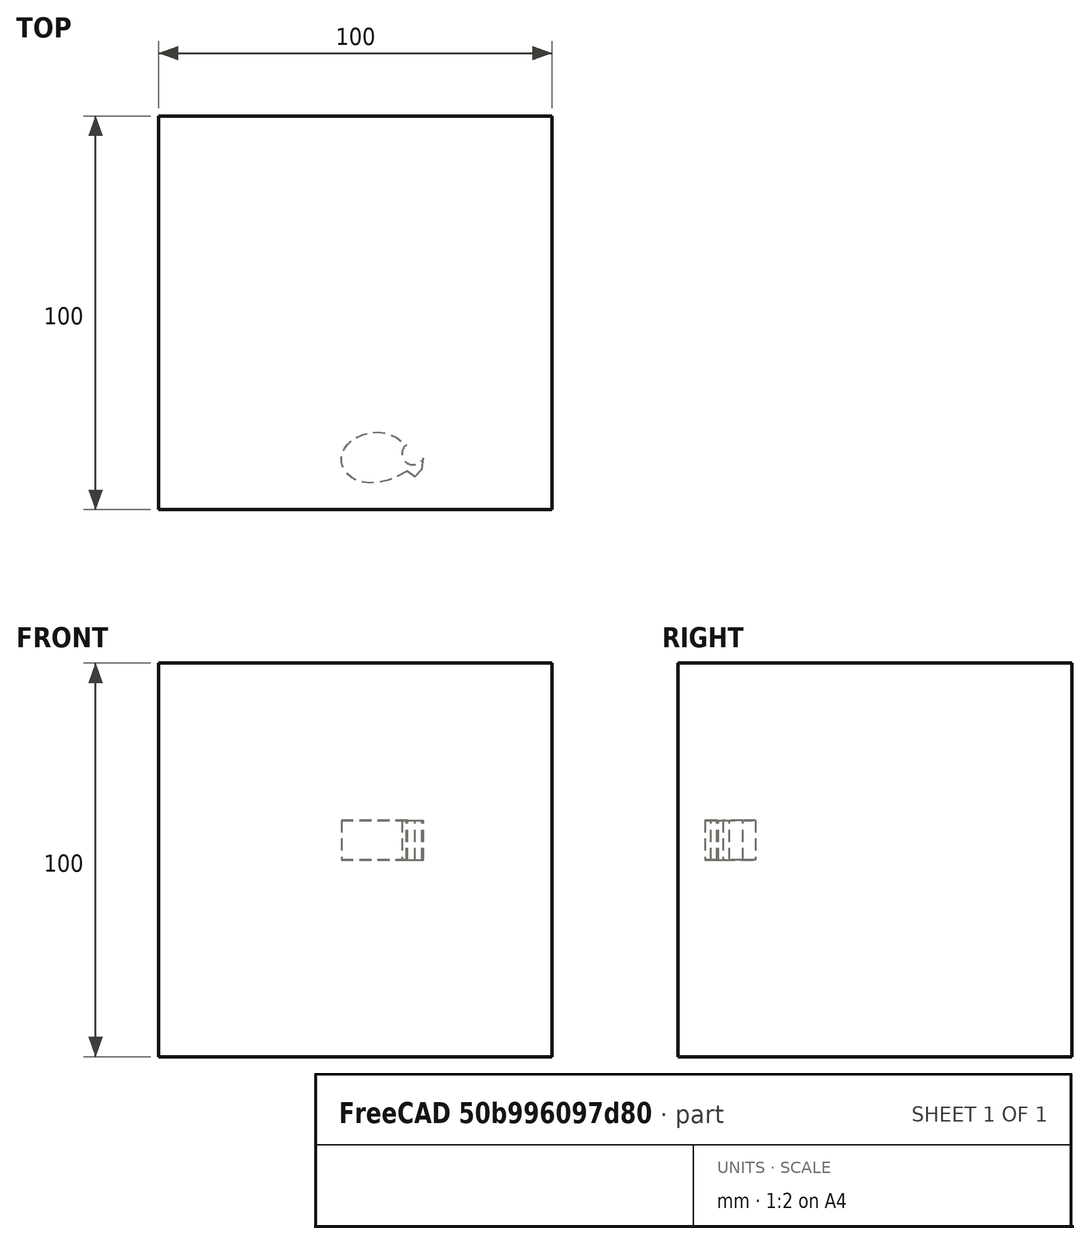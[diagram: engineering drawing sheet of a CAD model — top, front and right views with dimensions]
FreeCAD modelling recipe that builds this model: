
FCSTD DOCUMENT  (FreeCAD 1.0R39109 (Git))
Label: mirrorTest-3b
License: All rights reserved
LicenseURL: http://en.wikipedia.org/wiki/All_rights_reserved
objects: App::DocumentObjectGroupPython×1248, Part::Mirroring×2, App::Part×2, Part::FeaturePython×1, Sketcher::SketchObject×1, Part::Extrusion×1
note: 6 computed .brp shape members not serialized (recipe doc carries the construction recipe); baked Part::Feature solids carry a one-line shape summary decoded from their .brp

FEATURE [App::DocumentObjectGroupPython] HALFPI  # scripted group (container) (typed FeaturePython)
  name = HALFPI
  value = pi/2.
FEATURE [App::DocumentObjectGroupPython] PI  # scripted group (container) (typed FeaturePython)
  name = PI
  value = 1.*pi
FEATURE [App::DocumentObjectGroupPython] TWOPI  # scripted group (container) (typed FeaturePython)
  name = TWOPI
  value = 2.*pi
FEATURE [App::DocumentObjectGroupPython] Constants  # scripted group (container) (typed FeaturePython)
  Group = -> [HALFPI,PI,TWOPI]
FEATURE [App::DocumentObjectGroupPython] Variables  # scripted group (container) (typed FeaturePython)
FEATURE [App::DocumentObjectGroupPython] Quantities  # scripted group (container) (typed FeaturePython)
FEATURE [App::DocumentObjectGroupPython] Isotopes  # scripted group (container) (typed FeaturePython)
FEATURE [App::DocumentObjectGroupPython] Elements  # scripted group (container) (typed FeaturePython)
FEATURE [App::DocumentObjectGroupPython] G4Isotopes  # scripted group (container) (typed FeaturePython)
FEATURE [App::DocumentObjectGroupPython] H_element  # scripted group (container) (typed FeaturePython)
  Z = 1
  atom_value = 1.008
  formula = H
  name = H_element
FEATURE [App::DocumentObjectGroupPython] He_element  # scripted group (container) (typed FeaturePython)
  Z = 2
  atom_value = 4.0026
  formula = He
  name = He_element
FEATURE [App::DocumentObjectGroupPython] Li_element  # scripted group (container) (typed FeaturePython)
  Z = 3
  atom_value = 6.94
  formula = Li
  name = Li_element
FEATURE [App::DocumentObjectGroupPython] Be_element  # scripted group (container) (typed FeaturePython)
  Z = 4
  atom_value = 9.01218
  formula = Be
  name = Be_element
FEATURE [App::DocumentObjectGroupPython] B_element  # scripted group (container) (typed FeaturePython)
  Z = 5
  atom_value = 10.81
  formula = B
  name = B_element
FEATURE [App::DocumentObjectGroupPython] C_element  # scripted group (container) (typed FeaturePython)
  Z = 6
  atom_value = 12.011
  formula = C
  name = C_element
FEATURE [App::DocumentObjectGroupPython] N_element  # scripted group (container) (typed FeaturePython)
  Z = 7
  atom_value = 14.007
  formula = N
  name = N_element
FEATURE [App::DocumentObjectGroupPython] O_element  # scripted group (container) (typed FeaturePython)
  Z = 8
  atom_value = 15.999
  formula = O
  name = O_element
FEATURE [App::DocumentObjectGroupPython] F_element  # scripted group (container) (typed FeaturePython)
  Z = 9
  atom_value = 18.9984
  formula = F
  name = F_element
FEATURE [App::DocumentObjectGroupPython] Ne_element  # scripted group (container) (typed FeaturePython)
  Z = 10
  atom_value = 20.1797
  formula = Ne
  name = Ne_element
FEATURE [App::DocumentObjectGroupPython] Na_element  # scripted group (container) (typed FeaturePython)
  Z = 11
  atom_value = 22.9898
  formula = Na
  name = Na_element
FEATURE [App::DocumentObjectGroupPython] Mg_element  # scripted group (container) (typed FeaturePython)
  Z = 12
  atom_value = 24.305
  formula = Mg
  name = Mg_element
FEATURE [App::DocumentObjectGroupPython] Al_element  # scripted group (container) (typed FeaturePython)
  Z = 13
  atom_value = 26.9815
  formula = Al
  name = Al_element
FEATURE [App::DocumentObjectGroupPython] Si_element  # scripted group (container) (typed FeaturePython)
  Z = 14
  atom_value = 28.085
  formula = Si
  name = Si_element
FEATURE [App::DocumentObjectGroupPython] P_element  # scripted group (container) (typed FeaturePython)
  Z = 15
  atom_value = 30.9738
  formula = P
  name = P_element
FEATURE [App::DocumentObjectGroupPython] S_element  # scripted group (container) (typed FeaturePython)
  Z = 16
  atom_value = 32.06
  formula = S
  name = S_element
FEATURE [App::DocumentObjectGroupPython] Cl_element  # scripted group (container) (typed FeaturePython)
  Z = 17
  atom_value = 35.45
  formula = Cl
  name = Cl_element
FEATURE [App::DocumentObjectGroupPython] Ar_element  # scripted group (container) (typed FeaturePython)
  Z = 18
  atom_value = 39.95
  formula = Ar
  name = Ar_element
FEATURE [App::DocumentObjectGroupPython] K_element  # scripted group (container) (typed FeaturePython)
  Z = 19
  atom_value = 39.0983
  formula = K
  name = K_element
FEATURE [App::DocumentObjectGroupPython] Ca_element  # scripted group (container) (typed FeaturePython)
  Z = 20
  atom_value = 40.078
  formula = Ca
  name = Ca_element
FEATURE [App::DocumentObjectGroupPython] Sc_element  # scripted group (container) (typed FeaturePython)
  Z = 21
  atom_value = 44.9559
  formula = Sc
  name = Sc_element
FEATURE [App::DocumentObjectGroupPython] Ti_element  # scripted group (container) (typed FeaturePython)
  Z = 22
  atom_value = 47.867
  formula = Ti
  name = Ti_element
FEATURE [App::DocumentObjectGroupPython] V_element  # scripted group (container) (typed FeaturePython)
  Z = 23
  atom_value = 50.9415
  formula = V
  name = V_element
FEATURE [App::DocumentObjectGroupPython] Cr_element  # scripted group (container) (typed FeaturePython)
  Z = 24
  atom_value = 51.9961
  formula = Cr
  name = Cr_element
FEATURE [App::DocumentObjectGroupPython] Mn_element  # scripted group (container) (typed FeaturePython)
  Z = 25
  atom_value = 54.938
  formula = Mn
  name = Mn_element
FEATURE [App::DocumentObjectGroupPython] Fe_element  # scripted group (container) (typed FeaturePython)
  Z = 26
  atom_value = 55.845
  formula = Fe
  name = Fe_element
FEATURE [App::DocumentObjectGroupPython] Co_element  # scripted group (container) (typed FeaturePython)
  Z = 27
  atom_value = 58.9332
  formula = Co
  name = Co_element
FEATURE [App::DocumentObjectGroupPython] Ni_element  # scripted group (container) (typed FeaturePython)
  Z = 28
  atom_value = 58.6934
  formula = Ni
  name = Ni_element
FEATURE [App::DocumentObjectGroupPython] Cu_element  # scripted group (container) (typed FeaturePython)
  Z = 29
  atom_value = 63.546
  formula = Cu
  name = Cu_element
FEATURE [App::DocumentObjectGroupPython] Zn_element  # scripted group (container) (typed FeaturePython)
  Z = 30
  atom_value = 65.38
  formula = Zn
  name = Zn_element
FEATURE [App::DocumentObjectGroupPython] Ga_element  # scripted group (container) (typed FeaturePython)
  Z = 31
  atom_value = 69.723
  formula = Ga
  name = Ga_element
FEATURE [App::DocumentObjectGroupPython] Ge_element  # scripted group (container) (typed FeaturePython)
  Z = 32
  atom_value = 72.63
  formula = Ge
  name = Ge_element
FEATURE [App::DocumentObjectGroupPython] As_element  # scripted group (container) (typed FeaturePython)
  Z = 33
  atom_value = 74.9216
  formula = As
  name = As_element
FEATURE [App::DocumentObjectGroupPython] Se_element  # scripted group (container) (typed FeaturePython)
  Z = 34
  atom_value = 78.971
  formula = Se
  name = Se_element
FEATURE [App::DocumentObjectGroupPython] Br_element  # scripted group (container) (typed FeaturePython)
  Z = 35
  atom_value = 79.904
  formula = Br
  name = Br_element
FEATURE [App::DocumentObjectGroupPython] Kr_element  # scripted group (container) (typed FeaturePython)
  Z = 36
  atom_value = 83.798
  formula = Kr
  name = Kr_element
FEATURE [App::DocumentObjectGroupPython] Rb_element  # scripted group (container) (typed FeaturePython)
  Z = 37
  atom_value = 85.4678
  formula = Rb
  name = Rb_element
FEATURE [App::DocumentObjectGroupPython] Sr_element  # scripted group (container) (typed FeaturePython)
  Z = 38
  atom_value = 87.62
  formula = Sr
  name = Sr_element
FEATURE [App::DocumentObjectGroupPython] Y_element  # scripted group (container) (typed FeaturePython)
  Z = 39
  atom_value = 88.9058
  formula = Y
  name = Y_element
FEATURE [App::DocumentObjectGroupPython] Zr_element  # scripted group (container) (typed FeaturePython)
  Z = 40
  atom_value = 91.224
  formula = Zr
  name = Zr_element
FEATURE [App::DocumentObjectGroupPython] Nb_element  # scripted group (container) (typed FeaturePython)
  Z = 41
  atom_value = 92.9064
  formula = Nb
  name = Nb_element
FEATURE [App::DocumentObjectGroupPython] Mo_element  # scripted group (container) (typed FeaturePython)
  Z = 42
  atom_value = 95.95
  formula = Mo
  name = Mo_element
FEATURE [App::DocumentObjectGroupPython] Tc_element  # scripted group (container) (typed FeaturePython)
  Z = 43
  atom_value = 97
  formula = Tc
  name = Tc_element
FEATURE [App::DocumentObjectGroupPython] Ru_element  # scripted group (container) (typed FeaturePython)
  Z = 44
  atom_value = 101.07
  formula = Ru
  name = Ru_element
FEATURE [App::DocumentObjectGroupPython] Rh_element  # scripted group (container) (typed FeaturePython)
  Z = 45
  atom_value = 102.905
  formula = Rh
  name = Rh_element
FEATURE [App::DocumentObjectGroupPython] Pd_element  # scripted group (container) (typed FeaturePython)
  Z = 46
  atom_value = 106.42
  formula = Pd
  name = Pd_element
FEATURE [App::DocumentObjectGroupPython] Ag_element  # scripted group (container) (typed FeaturePython)
  Z = 47
  atom_value = 107.868
  formula = Ag
  name = Ag_element
FEATURE [App::DocumentObjectGroupPython] Cd_element  # scripted group (container) (typed FeaturePython)
  Z = 48
  atom_value = 112.414
  formula = Cd
  name = Cd_element
FEATURE [App::DocumentObjectGroupPython] In_element  # scripted group (container) (typed FeaturePython)
  Z = 49
  atom_value = 114.818
  formula = In
  name = In_element
FEATURE [App::DocumentObjectGroupPython] Sn_element  # scripted group (container) (typed FeaturePython)
  Z = 50
  atom_value = 118.71
  formula = Sn
  name = Sn_element
FEATURE [App::DocumentObjectGroupPython] Sb_element  # scripted group (container) (typed FeaturePython)
  Z = 51
  atom_value = 121.76
  formula = Sb
  name = Sb_element
FEATURE [App::DocumentObjectGroupPython] Te_element  # scripted group (container) (typed FeaturePython)
  Z = 52
  atom_value = 127.6
  formula = Te
  name = Te_element
FEATURE [App::DocumentObjectGroupPython] I_element  # scripted group (container) (typed FeaturePython)
  Z = 53
  atom_value = 126.904
  formula = I
  name = I_element
FEATURE [App::DocumentObjectGroupPython] Xe_element  # scripted group (container) (typed FeaturePython)
  Z = 54
  atom_value = 131.293
  formula = Xe
  name = Xe_element
FEATURE [App::DocumentObjectGroupPython] Cs_element  # scripted group (container) (typed FeaturePython)
  Z = 55
  atom_value = 132.905
  formula = Cs
  name = Cs_element
FEATURE [App::DocumentObjectGroupPython] Ba_element  # scripted group (container) (typed FeaturePython)
  Z = 56
  atom_value = 137.327
  formula = Ba
  name = Ba_element
FEATURE [App::DocumentObjectGroupPython] La_element  # scripted group (container) (typed FeaturePython)
  Z = 57
  atom_value = 138.905
  formula = La
  name = La_element
FEATURE [App::DocumentObjectGroupPython] Ce_element  # scripted group (container) (typed FeaturePython)
  Z = 58
  atom_value = 140.116
  formula = Ce
  name = Ce_element
FEATURE [App::DocumentObjectGroupPython] Pr_element  # scripted group (container) (typed FeaturePython)
  Z = 59
  atom_value = 140.908
  formula = Pr
  name = Pr_element
FEATURE [App::DocumentObjectGroupPython] Nd_element  # scripted group (container) (typed FeaturePython)
  Z = 60
  atom_value = 144.242
  formula = Nd
  name = Nd_element
FEATURE [App::DocumentObjectGroupPython] Pm_element  # scripted group (container) (typed FeaturePython)
  Z = 61
  atom_value = 145
  formula = Pm
  name = Pm_element
FEATURE [App::DocumentObjectGroupPython] Sm_element  # scripted group (container) (typed FeaturePython)
  Z = 62
  atom_value = 150.36
  formula = Sm
  name = Sm_element
FEATURE [App::DocumentObjectGroupPython] Eu_element  # scripted group (container) (typed FeaturePython)
  Z = 63
  atom_value = 151.964
  formula = Eu
  name = Eu_element
FEATURE [App::DocumentObjectGroupPython] Gd_element  # scripted group (container) (typed FeaturePython)
  Z = 64
  atom_value = 157.25
  formula = Gd
  name = Gd_element
FEATURE [App::DocumentObjectGroupPython] Tb_element  # scripted group (container) (typed FeaturePython)
  Z = 65
  atom_value = 158.925
  formula = Tb
  name = Tb_element
FEATURE [App::DocumentObjectGroupPython] Dy_element  # scripted group (container) (typed FeaturePython)
  Z = 66
  atom_value = 162.5
  formula = Dy
  name = Dy_element
FEATURE [App::DocumentObjectGroupPython] Ho_element  # scripted group (container) (typed FeaturePython)
  Z = 67
  atom_value = 164.93
  formula = Ho
  name = Ho_element
FEATURE [App::DocumentObjectGroupPython] Er_element  # scripted group (container) (typed FeaturePython)
  Z = 68
  atom_value = 167.259
  formula = Er
  name = Er_element
FEATURE [App::DocumentObjectGroupPython] Tm_element  # scripted group (container) (typed FeaturePython)
  Z = 69
  atom_value = 168.934
  formula = Tm
  name = Tm_element
FEATURE [App::DocumentObjectGroupPython] Yb_element  # scripted group (container) (typed FeaturePython)
  Z = 70
  atom_value = 173.045
  formula = Yb
  name = Yb_element
FEATURE [App::DocumentObjectGroupPython] Lu_element  # scripted group (container) (typed FeaturePython)
  Z = 71
  atom_value = 174.967
  formula = Lu
  name = Lu_element
FEATURE [App::DocumentObjectGroupPython] Hf_element  # scripted group (container) (typed FeaturePython)
  Z = 72
  atom_value = 178.49
  formula = Hf
  name = Hf_element
FEATURE [App::DocumentObjectGroupPython] Ta_element  # scripted group (container) (typed FeaturePython)
  Z = 73
  atom_value = 180.948
  formula = Ta
  name = Ta_element
FEATURE [App::DocumentObjectGroupPython] W_element  # scripted group (container) (typed FeaturePython)
  Z = 74
  atom_value = 183.84
  formula = W
  name = W_element
FEATURE [App::DocumentObjectGroupPython] Re_element  # scripted group (container) (typed FeaturePython)
  Z = 75
  atom_value = 186.207
  formula = Re
  name = Re_element
FEATURE [App::DocumentObjectGroupPython] Os_element  # scripted group (container) (typed FeaturePython)
  Z = 76
  atom_value = 190.23
  formula = Os
  name = Os_element
FEATURE [App::DocumentObjectGroupPython] Ir_element  # scripted group (container) (typed FeaturePython)
  Z = 77
  atom_value = 192.217
  formula = Ir
  name = Ir_element
FEATURE [App::DocumentObjectGroupPython] Pt_element  # scripted group (container) (typed FeaturePython)
  Z = 78
  atom_value = 195.084
  formula = Pt
  name = Pt_element
FEATURE [App::DocumentObjectGroupPython] Au_element  # scripted group (container) (typed FeaturePython)
  Z = 79
  atom_value = 196.967
  formula = Au
  name = Au_element
FEATURE [App::DocumentObjectGroupPython] Hg_element  # scripted group (container) (typed FeaturePython)
  Z = 80
  atom_value = 200.592
  formula = Hg
  name = Hg_element
FEATURE [App::DocumentObjectGroupPython] Tl_element  # scripted group (container) (typed FeaturePython)
  Z = 81
  atom_value = 204.38
  formula = Tl
  name = Tl_element
FEATURE [App::DocumentObjectGroupPython] Pb_element  # scripted group (container) (typed FeaturePython)
  Z = 82
  atom_value = 207.2
  formula = Pb
  name = Pb_element
FEATURE [App::DocumentObjectGroupPython] Bi_element  # scripted group (container) (typed FeaturePython)
  Z = 83
  atom_value = 208.98
  formula = Bi
  name = Bi_element
FEATURE [App::DocumentObjectGroupPython] Po_element  # scripted group (container) (typed FeaturePython)
  Z = 84
  atom_value = 209
  formula = Po
  name = Po_element
FEATURE [App::DocumentObjectGroupPython] At_element  # scripted group (container) (typed FeaturePython)
  Z = 85
  atom_value = 210
  formula = At
  name = At_element
FEATURE [App::DocumentObjectGroupPython] Rn_element  # scripted group (container) (typed FeaturePython)
  Z = 86
  atom_value = 222
  formula = Rn
  name = Rn_element
FEATURE [App::DocumentObjectGroupPython] Fr_element  # scripted group (container) (typed FeaturePython)
  Z = 87
  atom_value = 223
  formula = Fr
  name = Fr_element
FEATURE [App::DocumentObjectGroupPython] Ra_element  # scripted group (container) (typed FeaturePython)
  Z = 88
  atom_value = 226
  formula = Ra
  name = Ra_element
FEATURE [App::DocumentObjectGroupPython] Ac_element  # scripted group (container) (typed FeaturePython)
  Z = 89
  atom_value = 227
  formula = Ac
  name = Ac_element
FEATURE [App::DocumentObjectGroupPython] Th_element  # scripted group (container) (typed FeaturePython)
  Z = 90
  atom_value = 232.038
  formula = Th
  name = Th_element
FEATURE [App::DocumentObjectGroupPython] Pa_element  # scripted group (container) (typed FeaturePython)
  Z = 91
  atom_value = 231.036
  formula = Pa
  name = Pa_element
FEATURE [App::DocumentObjectGroupPython] U_element  # scripted group (container) (typed FeaturePython)
  Z = 92
  atom_value = 238.029
  formula = U
  name = U_element
FEATURE [App::DocumentObjectGroupPython] Np_element  # scripted group (container) (typed FeaturePython)
  Z = 93
  atom_value = 237
  formula = Np
  name = Np_element
FEATURE [App::DocumentObjectGroupPython] Pu_element  # scripted group (container) (typed FeaturePython)
  Z = 94
  atom_value = 244
  formula = Pu
  name = Pu_element
FEATURE [App::DocumentObjectGroupPython] Am_element  # scripted group (container) (typed FeaturePython)
  Z = 95
  atom_value = 243
  formula = Am
  name = Am_element
FEATURE [App::DocumentObjectGroupPython] Cm_element  # scripted group (container) (typed FeaturePython)
  Z = 96
  atom_value = 247
  formula = Cm
  name = Cm_element
FEATURE [App::DocumentObjectGroupPython] Bk_element  # scripted group (container) (typed FeaturePython)
  Z = 97
  atom_value = 247
  formula = Bk
  name = Bk_element
FEATURE [App::DocumentObjectGroupPython] Cf_element  # scripted group (container) (typed FeaturePython)
  Z = 98
  atom_value = 251
  formula = Cf
  name = Cf_element
FEATURE [App::DocumentObjectGroupPython] G4Elements  # scripted group (container) (typed FeaturePython)
  Group = -> [H_element,He_element,Li_element,Be_element,B_element,C_element,N_element,O_element,F_element,Ne_element,Na_element,Mg_element,Al_element,Si_element,P_element,S_element,Cl_element,Ar_element,K_element,Ca_element,Sc_element,Ti_element,V_element,Cr_element,Mn_element,Fe_element,Co_element,Ni_element,Cu_element,Zn_element,Ga_element,Ge_element,As_element,Se_element,Br_element,Kr_element,Rb_element,+61 more]
FEATURE [App::DocumentObjectGroupPython] H_element001  label="H_element : 0.101"  # scripted group (container) (typed FeaturePython)
  n = 0.101327
FEATURE [App::DocumentObjectGroupPython] C_element001  label="C_element : 0.775"  # scripted group (container) (typed FeaturePython)
  n = 0.7755
FEATURE [App::DocumentObjectGroupPython] N_element001  label="N_element : 0.035"  # scripted group (container) (typed FeaturePython)
  n = 0.035057
FEATURE [App::DocumentObjectGroupPython] O_element001  label="O_element : 0.052"  # scripted group (container) (typed FeaturePython)
  n = 0.0523159
FEATURE [App::DocumentObjectGroupPython] F_element001  label="F_element : 0.017"  # scripted group (container) (typed FeaturePython)
  n = 0.017422
FEATURE [App::DocumentObjectGroupPython] Ca_element001  label="Ca_element : 0.018"  # scripted group (container) (typed FeaturePython)
  n = 0.018378
FEATURE [App::DocumentObjectGroupPython] G4_A_150_TISSUE  label="G4_A-150_TISSUE"  # scripted group (container) (typed FeaturePython)
  Dunit = g/cm3
  Dvalue = 1.127
  Group = -> [H_element001,C_element001,N_element001,O_element001,F_element001,Ca_element001]
  conduct = 2
  density = 1
  expand = 3
  formula = G4_A-150_TISSUE
  name = G4_A-150_TISSUE
  specific = 4
FEATURE [App::DocumentObjectGroupPython] C_element002  label="C_element : 3"  # scripted group (container) (typed FeaturePython)
  n = 3
  ref = C_element
FEATURE [App::DocumentObjectGroupPython] H_element002  label="H_element : 6"  # scripted group (container) (typed FeaturePython)
  n = 6
  ref = H_element
FEATURE [App::DocumentObjectGroupPython] O_element002  label="O_element : 1"  # scripted group (container) (typed FeaturePython)
  n = 1
  ref = O_element
FEATURE [App::DocumentObjectGroupPython] G4_ACETONE  # scripted group (container) (typed FeaturePython)
  Dunit = g/cm3
  Dvalue = 0.7899
  Group = -> [C_element002,H_element002,O_element002]
  conduct = 2
  density = 1
  expand = 3
  formula = G4_ACETONE
  name = G4_ACETONE
  specific = 4
FEATURE [App::DocumentObjectGroupPython] C_element003  label="C_element : 2"  # scripted group (container) (typed FeaturePython)
  n = 2
  ref = C_element
FEATURE [App::DocumentObjectGroupPython] H_element003  label="H_element : 2"  # scripted group (container) (typed FeaturePython)
  n = 2
  ref = H_element
FEATURE [App::DocumentObjectGroupPython] G4_ACETYLENE  # scripted group (container) (typed FeaturePython)
  Dunit = g/cm3
  Dvalue = 0.0010967
  Group = -> [C_element003,H_element003]
  conduct = 2
  density = 1
  expand = 3
  formula = G4_ACETYLENE
  name = G4_ACETYLENE
  specific = 4
FEATURE [App::DocumentObjectGroupPython] C_element004  label="C_element : 5"  # scripted group (container) (typed FeaturePython)
  n = 5
  ref = C_element
FEATURE [App::DocumentObjectGroupPython] H_element004  label="H_element : 5"  # scripted group (container) (typed FeaturePython)
  n = 5
  ref = H_element
FEATURE [App::DocumentObjectGroupPython] N_element002  label="N_element : 5"  # scripted group (container) (typed FeaturePython)
  n = 5
  ref = N_element
FEATURE [App::DocumentObjectGroupPython] G4_ADENINE  # scripted group (container) (typed FeaturePython)
  Dunit = g/cm3
  Dvalue = 1.6
  Group = -> [C_element004,H_element004,N_element002]
  conduct = 2
  density = 1
  expand = 3
  formula = G4_ADENINE
  name = G4_ADENINE
  specific = 4
FEATURE [App::DocumentObjectGroupPython] H_element005  label="H_element : 0.114"  # scripted group (container) (typed FeaturePython)
  n = 0.114
FEATURE [App::DocumentObjectGroupPython] C_element005  label="C_element : 0.598"  # scripted group (container) (typed FeaturePython)
  n = 0.598
FEATURE [App::DocumentObjectGroupPython] N_element003  label="N_element : 0.007"  # scripted group (container) (typed FeaturePython)
  n = 0.007
FEATURE [App::DocumentObjectGroupPython] O_element003  label="O_element : 0.278"  # scripted group (container) (typed FeaturePython)
  n = 0.278
FEATURE [App::DocumentObjectGroupPython] Na_element001  label="Na_element : 0.001"  # scripted group (container) (typed FeaturePython)
  n = 0.001
FEATURE [App::DocumentObjectGroupPython] S_element001  label="S_element : 0.001"  # scripted group (container) (typed FeaturePython)
  n = 0.001
FEATURE [App::DocumentObjectGroupPython] Cl_element001  label="Cl_element : 0.001"  # scripted group (container) (typed FeaturePython)
  n = 0.001
FEATURE [App::DocumentObjectGroupPython] G4_ADIPOSE_TISSUE_ICRP  # scripted group (container) (typed FeaturePython)
  Dunit = g/cm3
  Dvalue = 0.95
  Group = -> [H_element005,C_element005,N_element003,O_element003,Na_element001,S_element001,Cl_element001]
  conduct = 2
  density = 1
  expand = 3
  formula = G4_ADIPOSE_TISSUE_ICRP
  name = G4_ADIPOSE_TISSUE_ICRP
  specific = 4
FEATURE [App::DocumentObjectGroupPython] C_element006  label="C_element : 0.000"  # scripted group (container) (typed FeaturePython)
  n = 0.000124
FEATURE [App::DocumentObjectGroupPython] N_element004  label="N_element : 0.755"  # scripted group (container) (typed FeaturePython)
  n = 0.755268
FEATURE [App::DocumentObjectGroupPython] O_element004  label="O_element : 0.232"  # scripted group (container) (typed FeaturePython)
  n = 0.231781
FEATURE [App::DocumentObjectGroupPython] Ar_element001  label="Ar_element : 0.013"  # scripted group (container) (typed FeaturePython)
  n = 0.012827
FEATURE [App::DocumentObjectGroupPython] G4_AIR  # scripted group (container) (typed FeaturePython)
  Dunit = g/cm3
  Dvalue = 0.00120479
  Group = -> [C_element006,N_element004,O_element004,Ar_element001]
  conduct = 2
  density = 1
  expand = 3
  formula = G4_AIR
  name = G4_AIR
  specific = 4
FEATURE [App::DocumentObjectGroupPython] C_element007  label="C_element : 006"  # scripted group (container) (typed FeaturePython)
  n = 3
  ref = C_element
FEATURE [App::DocumentObjectGroupPython] H_element006  label="H_element : 7"  # scripted group (container) (typed FeaturePython)
  n = 7
  ref = H_element
FEATURE [App::DocumentObjectGroupPython] N_element005  label="N_element : 1"  # scripted group (container) (typed FeaturePython)
  n = 1
  ref = N_element
FEATURE [App::DocumentObjectGroupPython] O_element005  label="O_element : 2"  # scripted group (container) (typed FeaturePython)
  n = 2
  ref = O_element
FEATURE [App::DocumentObjectGroupPython] G4_ALANINE  # scripted group (container) (typed FeaturePython)
  Dunit = g/cm3
  Dvalue = 1.42
  Group = -> [C_element007,H_element006,N_element005,O_element005]
  conduct = 2
  density = 1
  expand = 3
  formula = G4_ALANINE
  name = G4_ALANINE
  specific = 4
FEATURE [App::DocumentObjectGroupPython] Al_element001  label="Al_element : 2"  # scripted group (container) (typed FeaturePython)
  n = 2
  ref = Al_element
FEATURE [App::DocumentObjectGroupPython] O_element006  label="O_element : 3"  # scripted group (container) (typed FeaturePython)
  n = 3
  ref = O_element
FEATURE [App::DocumentObjectGroupPython] G4_ALUMINUM_OXIDE  # scripted group (container) (typed FeaturePython)
  Dunit = g/cm3
  Dvalue = 3.97
  Group = -> [Al_element001,O_element006]
  conduct = 2
  density = 1
  expand = 3
  formula = G4_ALUMINUM_OXIDE
  name = G4_ALUMINUM_OXIDE
  specific = 4
FEATURE [App::DocumentObjectGroupPython] H_element007  label="H_element : 0.106"  # scripted group (container) (typed FeaturePython)
  n = 0.10593
FEATURE [App::DocumentObjectGroupPython] C_element008  label="C_element : 0.789"  # scripted group (container) (typed FeaturePython)
  n = 0.788974
FEATURE [App::DocumentObjectGroupPython] O_element007  label="O_element : 0.105"  # scripted group (container) (typed FeaturePython)
  n = 0.105096
FEATURE [App::DocumentObjectGroupPython] G4_AMBER  # scripted group (container) (typed FeaturePython)
  Dunit = g/cm3
  Dvalue = 1.1
  Group = -> [H_element007,C_element008,O_element007]
  conduct = 2
  density = 1
  expand = 3
  formula = G4_AMBER
  name = G4_AMBER
  specific = 4
FEATURE [App::DocumentObjectGroupPython] N_element006  label="N_element : 006"  # scripted group (container) (typed FeaturePython)
  n = 1
  ref = N_element
FEATURE [App::DocumentObjectGroupPython] H_element008  label="H_element : 3"  # scripted group (container) (typed FeaturePython)
  n = 3
  ref = H_element
FEATURE [App::DocumentObjectGroupPython] G4_AMMONIA  # scripted group (container) (typed FeaturePython)
  Dunit = g/cm3
  Dvalue = 0.000826019
  Group = -> [N_element006,H_element008]
  conduct = 2
  density = 1
  expand = 3
  formula = G4_AMMONIA
  name = G4_AMMONIA
  specific = 4
FEATURE [App::DocumentObjectGroupPython] C_element009  label="C_element : 6"  # scripted group (container) (typed FeaturePython)
  n = 6
  ref = C_element
FEATURE [App::DocumentObjectGroupPython] H_element009  label="H_element : 008"  # scripted group (container) (typed FeaturePython)
  n = 7
  ref = H_element
FEATURE [App::DocumentObjectGroupPython] N_element007  label="N_element : 007"  # scripted group (container) (typed FeaturePython)
  n = 1
  ref = N_element
FEATURE [App::DocumentObjectGroupPython] G4_ANILINE  # scripted group (container) (typed FeaturePython)
  Dunit = g/cm3
  Dvalue = 1.0235
  Group = -> [C_element009,H_element009,N_element007]
  conduct = 2
  density = 1
  expand = 3
  formula = G4_ANILINE
  name = G4_ANILINE
  specific = 4
FEATURE [App::DocumentObjectGroupPython] C_element010  label="C_element : 14"  # scripted group (container) (typed FeaturePython)
  n = 14
  ref = C_element
FEATURE [App::DocumentObjectGroupPython] H_element010  label="H_element : 10"  # scripted group (container) (typed FeaturePython)
  n = 10
  ref = H_element
FEATURE [App::DocumentObjectGroupPython] G4_ANTHRACENE  # scripted group (container) (typed FeaturePython)
  Dunit = g/cm3
  Dvalue = 1.283
  Group = -> [C_element010,H_element010]
  conduct = 2
  density = 1
  expand = 3
  formula = G4_ANTHRACENE
  name = G4_ANTHRACENE
  specific = 4
FEATURE [App::DocumentObjectGroupPython] H_element011  label="H_element : 0.065"  # scripted group (container) (typed FeaturePython)
  n = 0.0654709
FEATURE [App::DocumentObjectGroupPython] C_element011  label="C_element : 0.537"  # scripted group (container) (typed FeaturePython)
  n = 0.536944
FEATURE [App::DocumentObjectGroupPython] N_element008  label="N_element : 0.021"  # scripted group (container) (typed FeaturePython)
  n = 0.0215
FEATURE [App::DocumentObjectGroupPython] O_element008  label="O_element : 0.032"  # scripted group (container) (typed FeaturePython)
  n = 0.032085
FEATURE [App::DocumentObjectGroupPython] F_element002  label="F_element : 0.167"  # scripted group (container) (typed FeaturePython)
  n = 0.167411
FEATURE [App::DocumentObjectGroupPython] Ca_element002  label="Ca_element : 0.177"  # scripted group (container) (typed FeaturePython)
  n = 0.176589
FEATURE [App::DocumentObjectGroupPython] G4_B_100_BONE  label="G4_B-100_BONE"  # scripted group (container) (typed FeaturePython)
  Dunit = g/cm3
  Dvalue = 1.45
  Group = -> [H_element011,C_element011,N_element008,O_element008,F_element002,Ca_element002]
  conduct = 2
  density = 1
  expand = 3
  formula = G4_B-100_BONE
  name = G4_B-100_BONE
  specific = 4
FEATURE [App::DocumentObjectGroupPython] H_element012  label="H_element : 0.057"  # scripted group (container) (typed FeaturePython)
  n = 0.057441
FEATURE [App::DocumentObjectGroupPython] C_element012  label="C_element : 0.790"  # scripted group (container) (typed FeaturePython)
  n = 0.774591
FEATURE [App::DocumentObjectGroupPython] O_element009  label="O_element : 0.168"  # scripted group (container) (typed FeaturePython)
  n = 0.167968
FEATURE [App::DocumentObjectGroupPython] G4_BAKELITE  # scripted group (container) (typed FeaturePython)
  Dunit = g/cm3
  Dvalue = 1.25
  Group = -> [H_element012,C_element012,O_element009]
  conduct = 2
  density = 1
  expand = 3
  formula = G4_BAKELITE
  name = G4_BAKELITE
  specific = 4
FEATURE [App::DocumentObjectGroupPython] Ba_element001  label="Ba_element : 1"  # scripted group (container) (typed FeaturePython)
  n = 1
  ref = Ba_element
FEATURE [App::DocumentObjectGroupPython] F_element003  label="F_element : 2"  # scripted group (container) (typed FeaturePython)
  n = 2
  ref = F_element
FEATURE [App::DocumentObjectGroupPython] G4_BARIUM_FLUORIDE  # scripted group (container) (typed FeaturePython)
  Dunit = g/cm3
  Dvalue = 4.89
  Group = -> [Ba_element001,F_element003]
  conduct = 2
  density = 1
  expand = 3
  formula = G4_BARIUM_FLUORIDE
  name = G4_BARIUM_FLUORIDE
  specific = 4
FEATURE [App::DocumentObjectGroupPython] Ba_element002  label="Ba_element : 002"  # scripted group (container) (typed FeaturePython)
  n = 1
  ref = Ba_element
FEATURE [App::DocumentObjectGroupPython] S_element002  label="S_element : 1"  # scripted group (container) (typed FeaturePython)
  n = 1
  ref = S_element
FEATURE [App::DocumentObjectGroupPython] O_element010  label="O_element : 4"  # scripted group (container) (typed FeaturePython)
  n = 4
  ref = O_element
FEATURE [App::DocumentObjectGroupPython] G4_BARIUM_SULFATE  # scripted group (container) (typed FeaturePython)
  Dunit = g/cm3
  Dvalue = 4.5
  Group = -> [Ba_element002,S_element002,O_element010]
  conduct = 2
  density = 1
  expand = 3
  formula = G4_BARIUM_SULFATE
  name = G4_BARIUM_SULFATE
  specific = 4
FEATURE [App::DocumentObjectGroupPython] C_element013  label="C_element : 007"  # scripted group (container) (typed FeaturePython)
  n = 6
  ref = C_element
FEATURE [App::DocumentObjectGroupPython] H_element013  label="H_element : 009"  # scripted group (container) (typed FeaturePython)
  n = 6
  ref = H_element
FEATURE [App::DocumentObjectGroupPython] G4_BENZENE  # scripted group (container) (typed FeaturePython)
  Dunit = g/cm3
  Dvalue = 0.87865
  Group = -> [C_element013,H_element013]
  conduct = 2
  density = 1
  expand = 3
  formula = G4_BENZENE
  name = G4_BENZENE
  specific = 4
FEATURE [App::DocumentObjectGroupPython] Be_element001  label="Be_element : 1"  # scripted group (container) (typed FeaturePython)
  n = 1
  ref = Be_element
FEATURE [App::DocumentObjectGroupPython] O_element011  label="O_element : 005"  # scripted group (container) (typed FeaturePython)
  n = 1
  ref = O_element
FEATURE [App::DocumentObjectGroupPython] G4_BERYLLIUM_OXIDE  # scripted group (container) (typed FeaturePython)
  Dunit = g/cm3
  Dvalue = 3.01
  Group = -> [Be_element001,O_element011]
  conduct = 2
  density = 1
  expand = 3
  formula = G4_BERYLLIUM_OXIDE
  name = G4_BERYLLIUM_OXIDE
  specific = 4
FEATURE [App::DocumentObjectGroupPython] Bi_element001  label="Bi_element : 4"  # scripted group (container) (typed FeaturePython)
  n = 4
  ref = Bi_element
FEATURE [App::DocumentObjectGroupPython] Ge_element001  label="Ge_element : 3"  # scripted group (container) (typed FeaturePython)
  n = 3
  ref = Ge_element
FEATURE [App::DocumentObjectGroupPython] O_element012  label="O_element : 12"  # scripted group (container) (typed FeaturePython)
  n = 12
  ref = O_element
FEATURE [App::DocumentObjectGroupPython] G4_BGO  # scripted group (container) (typed FeaturePython)
  Dunit = g/cm3
  Dvalue = 7.13
  Group = -> [Bi_element001,Ge_element001,O_element012]
  conduct = 2
  density = 1
  expand = 3
  formula = G4_BGO
  name = G4_BGO
  specific = 4
FEATURE [App::DocumentObjectGroupPython] H_element014  label="H_element : 0.102"  # scripted group (container) (typed FeaturePython)
  n = 0.102
FEATURE [App::DocumentObjectGroupPython] C_element014  label="C_element : 0.110"  # scripted group (container) (typed FeaturePython)
  n = 0.11
FEATURE [App::DocumentObjectGroupPython] N_element009  label="N_element : 0.033"  # scripted group (container) (typed FeaturePython)
  n = 0.033
FEATURE [App::DocumentObjectGroupPython] O_element013  label="O_element : 0.745"  # scripted group (container) (typed FeaturePython)
  n = 0.745
FEATURE [App::DocumentObjectGroupPython] Na_element002  label="Na_element : 0.002"  # scripted group (container) (typed FeaturePython)
  n = 0.001
FEATURE [App::DocumentObjectGroupPython] P_element001  label="P_element : 0.001"  # scripted group (container) (typed FeaturePython)
  n = 0.001
FEATURE [App::DocumentObjectGroupPython] S_element003  label="S_element : 0.002"  # scripted group (container) (typed FeaturePython)
  n = 0.002
FEATURE [App::DocumentObjectGroupPython] Cl_element002  label="Cl_element : 0.003"  # scripted group (container) (typed FeaturePython)
  n = 0.003
FEATURE [App::DocumentObjectGroupPython] K_element001  label="K_element : 0.002"  # scripted group (container) (typed FeaturePython)
  n = 0.002
FEATURE [App::DocumentObjectGroupPython] Fe_element001  label="Fe_element : 0.001"  # scripted group (container) (typed FeaturePython)
  n = 0.001
FEATURE [App::DocumentObjectGroupPython] G4_BLOOD_ICRP  # scripted group (container) (typed FeaturePython)
  Dunit = g/cm3
  Dvalue = 1.06
  Group = -> [H_element014,C_element014,N_element009,O_element013,Na_element002,P_element001,S_element003,Cl_element002,K_element001,Fe_element001]
  conduct = 2
  density = 1
  expand = 3
  formula = G4_BLOOD_ICRP
  name = G4_BLOOD_ICRP
  specific = 4
FEATURE [App::DocumentObjectGroupPython] H_element015  label="H_element : 0.064"  # scripted group (container) (typed FeaturePython)
  n = 0.064
FEATURE [App::DocumentObjectGroupPython] C_element015  label="C_element : 0.278"  # scripted group (container) (typed FeaturePython)
  n = 0.278
FEATURE [App::DocumentObjectGroupPython] N_element010  label="N_element : 0.027"  # scripted group (container) (typed FeaturePython)
  n = 0.027
FEATURE [App::DocumentObjectGroupPython] O_element014  label="O_element : 0.410"  # scripted group (container) (typed FeaturePython)
  n = 0.41
FEATURE [App::DocumentObjectGroupPython] Mg_element001  label="Mg_element : 0.002"  # scripted group (container) (typed FeaturePython)
  n = 0.002
FEATURE [App::DocumentObjectGroupPython] P_element002  label="P_element : 0.070"  # scripted group (container) (typed FeaturePython)
  n = 0.07
FEATURE [App::DocumentObjectGroupPython] S_element004  label="S_element : 0.003"  # scripted group (container) (typed FeaturePython)
  n = 0.002
FEATURE [App::DocumentObjectGroupPython] Ca_element003  label="Ca_element : 0.147"  # scripted group (container) (typed FeaturePython)
  n = 0.147
FEATURE [App::DocumentObjectGroupPython] G4_BONE_COMPACT_ICRU  # scripted group (container) (typed FeaturePython)
  Dunit = g/cm3
  Dvalue = 1.85
  Group = -> [H_element015,C_element015,N_element010,O_element014,Mg_element001,P_element002,S_element004,Ca_element003]
  conduct = 2
  density = 1
  expand = 3
  formula = G4_BONE_COMPACT_ICRU
  name = G4_BONE_COMPACT_ICRU
  specific = 4
FEATURE [App::DocumentObjectGroupPython] H_element016  label="H_element : 0.034"  # scripted group (container) (typed FeaturePython)
  n = 0.034
FEATURE [App::DocumentObjectGroupPython] C_element016  label="C_element : 0.155"  # scripted group (container) (typed FeaturePython)
  n = 0.155
FEATURE [App::DocumentObjectGroupPython] N_element011  label="N_element : 0.042"  # scripted group (container) (typed FeaturePython)
  n = 0.042
FEATURE [App::DocumentObjectGroupPython] O_element015  label="O_element : 0.435"  # scripted group (container) (typed FeaturePython)
  n = 0.435
FEATURE [App::DocumentObjectGroupPython] Na_element003  label="Na_element : 0.003"  # scripted group (container) (typed FeaturePython)
  n = 0.001
FEATURE [App::DocumentObjectGroupPython] Mg_element002  label="Mg_element : 0.003"  # scripted group (container) (typed FeaturePython)
  n = 0.002
FEATURE [App::DocumentObjectGroupPython] P_element003  label="P_element : 0.103"  # scripted group (container) (typed FeaturePython)
  n = 0.103
FEATURE [App::DocumentObjectGroupPython] S_element005  label="S_element : 0.004"  # scripted group (container) (typed FeaturePython)
  n = 0.003
FEATURE [App::DocumentObjectGroupPython] Ca_element004  label="Ca_element : 0.225"  # scripted group (container) (typed FeaturePython)
  n = 0.225
FEATURE [App::DocumentObjectGroupPython] G4_BONE_CORTICAL_ICRP  # scripted group (container) (typed FeaturePython)
  Dunit = g/cm3
  Dvalue = 1.92
  Group = -> [H_element016,C_element016,N_element011,O_element015,Na_element003,Mg_element002,P_element003,S_element005,Ca_element004]
  conduct = 2
  density = 1
  expand = 3
  formula = G4_BONE_CORTICAL_ICRP
  name = G4_BONE_CORTICAL_ICRP
  specific = 4
FEATURE [App::DocumentObjectGroupPython] B_element001  label="B_element : 4"  # scripted group (container) (typed FeaturePython)
  n = 4
  ref = B_element
FEATURE [App::DocumentObjectGroupPython] C_element017  label="C_element : 1"  # scripted group (container) (typed FeaturePython)
  n = 1
  ref = C_element
FEATURE [App::DocumentObjectGroupPython] G4_BORON_CARBIDE  # scripted group (container) (typed FeaturePython)
  Dunit = g/cm3
  Dvalue = 2.52
  Group = -> [B_element001,C_element017]
  conduct = 2
  density = 1
  expand = 3
  formula = G4_BORON_CARBIDE
  name = G4_BORON_CARBIDE
  specific = 4
FEATURE [App::DocumentObjectGroupPython] B_element002  label="B_element : 2"  # scripted group (container) (typed FeaturePython)
  n = 2
  ref = B_element
FEATURE [App::DocumentObjectGroupPython] O_element016  label="O_element : 006"  # scripted group (container) (typed FeaturePython)
  n = 3
  ref = O_element
FEATURE [App::DocumentObjectGroupPython] G4_BORON_OXIDE  # scripted group (container) (typed FeaturePython)
  Dunit = g/cm3
  Dvalue = 1.812
  Group = -> [B_element002,O_element016]
  conduct = 2
  density = 1
  expand = 3
  formula = G4_BORON_OXIDE
  name = G4_BORON_OXIDE
  specific = 4
FEATURE [App::DocumentObjectGroupPython] H_element017  label="H_element : 0.107"  # scripted group (container) (typed FeaturePython)
  n = 0.107
FEATURE [App::DocumentObjectGroupPython] C_element018  label="C_element : 0.145"  # scripted group (container) (typed FeaturePython)
  n = 0.145
FEATURE [App::DocumentObjectGroupPython] N_element012  label="N_element : 0.022"  # scripted group (container) (typed FeaturePython)
  n = 0.022
FEATURE [App::DocumentObjectGroupPython] O_element017  label="O_element : 0.712"  # scripted group (container) (typed FeaturePython)
  n = 0.712
FEATURE [App::DocumentObjectGroupPython] Na_element004  label="Na_element : 0.004"  # scripted group (container) (typed FeaturePython)
  n = 0.002
FEATURE [App::DocumentObjectGroupPython] P_element004  label="P_element : 0.004"  # scripted group (container) (typed FeaturePython)
  n = 0.004
FEATURE [App::DocumentObjectGroupPython] S_element006  label="S_element : 0.005"  # scripted group (container) (typed FeaturePython)
  n = 0.002
FEATURE [App::DocumentObjectGroupPython] Cl_element003  label="Cl_element : 0.004"  # scripted group (container) (typed FeaturePython)
  n = 0.003
FEATURE [App::DocumentObjectGroupPython] K_element002  label="K_element : 0.003"  # scripted group (container) (typed FeaturePython)
  n = 0.003
FEATURE [App::DocumentObjectGroupPython] G4_BRAIN_ICRP  # scripted group (container) (typed FeaturePython)
  Dunit = g/cm3
  Dvalue = 1.04
  Group = -> [H_element017,C_element018,N_element012,O_element017,Na_element004,P_element004,S_element006,Cl_element003,K_element002]
  conduct = 2
  density = 1
  expand = 3
  formula = G4_BRAIN_ICRP
  name = G4_BRAIN_ICRP
  specific = 4
FEATURE [App::DocumentObjectGroupPython] C_element019  label="C_element : 4"  # scripted group (container) (typed FeaturePython)
  n = 4
  ref = C_element
FEATURE [App::DocumentObjectGroupPython] H_element018  label="H_element : 010"  # scripted group (container) (typed FeaturePython)
  n = 10
  ref = H_element
FEATURE [App::DocumentObjectGroupPython] G4_BUTANE  # scripted group (container) (typed FeaturePython)
  Dunit = g/cm3
  Dvalue = 0.00249343
  Group = -> [C_element019,H_element018]
  conduct = 2
  density = 1
  expand = 3
  formula = G4_BUTANE
  name = G4_BUTANE
  specific = 4
FEATURE [App::DocumentObjectGroupPython] C_element020  label="C_element : 008"  # scripted group (container) (typed FeaturePython)
  n = 4
  ref = C_element
FEATURE [App::DocumentObjectGroupPython] H_element019  label="H_element : 011"  # scripted group (container) (typed FeaturePython)
  n = 10
  ref = H_element
FEATURE [App::DocumentObjectGroupPython] O_element018  label="O_element : 007"  # scripted group (container) (typed FeaturePython)
  n = 1
  ref = O_element
FEATURE [App::DocumentObjectGroupPython] G4_N_BUTYL_ALCOHOL  label="G4_N-BUTYL_ALCOHOL"  # scripted group (container) (typed FeaturePython)
  Dunit = g/cm3
  Dvalue = 0.8098
  Group = -> [C_element020,H_element019,O_element018]
  conduct = 2
  density = 1
  expand = 3
  formula = G4_N-BUTYL_ALCOHOL
  name = G4_N-BUTYL_ALCOHOL
  specific = 4
FEATURE [App::DocumentObjectGroupPython] H_element020  label="H_element : 0.025"  # scripted group (container) (typed FeaturePython)
  n = 0.02468
FEATURE [App::DocumentObjectGroupPython] C_element021  label="C_element : 0.502"  # scripted group (container) (typed FeaturePython)
  n = 0.501611
FEATURE [App::DocumentObjectGroupPython] O_element019  label="O_element : 0.005"  # scripted group (container) (typed FeaturePython)
  n = 0.004527
FEATURE [App::DocumentObjectGroupPython] F_element004  label="F_element : 0.465"  # scripted group (container) (typed FeaturePython)
  n = 0.465209
FEATURE [App::DocumentObjectGroupPython] Si_element001  label="Si_element : 0.004"  # scripted group (container) (typed FeaturePython)
  n = 0.003973
FEATURE [App::DocumentObjectGroupPython] G4_C_552  label="G4_C-552"  # scripted group (container) (typed FeaturePython)
  Dunit = g/cm3
  Dvalue = 1.76
  Group = -> [H_element020,C_element021,O_element019,F_element004,Si_element001]
  conduct = 2
  density = 1
  expand = 3
  formula = G4_C-552
  name = G4_C-552
  specific = 4
FEATURE [App::DocumentObjectGroupPython] Cd_element001  label="Cd_element : 1"  # scripted group (container) (typed FeaturePython)
  n = 1
  ref = Cd_element
FEATURE [App::DocumentObjectGroupPython] Te_element001  label="Te_element : 1"  # scripted group (container) (typed FeaturePython)
  n = 1
  ref = Te_element
FEATURE [App::DocumentObjectGroupPython] G4_CADMIUM_TELLURIDE  # scripted group (container) (typed FeaturePython)
  Dunit = g/cm3
  Dvalue = 6.2
  Group = -> [Cd_element001,Te_element001]
  conduct = 2
  density = 1
  expand = 3
  formula = G4_CADMIUM_TELLURIDE
  name = G4_CADMIUM_TELLURIDE
  specific = 4
FEATURE [App::DocumentObjectGroupPython] Cd_element002  label="Cd_element : 002"  # scripted group (container) (typed FeaturePython)
  n = 1
  ref = Cd_element
FEATURE [App::DocumentObjectGroupPython] W_element001  label="W_element : 1"  # scripted group (container) (typed FeaturePython)
  n = 1
  ref = W_element
FEATURE [App::DocumentObjectGroupPython] O_element020  label="O_element : 008"  # scripted group (container) (typed FeaturePython)
  n = 4
  ref = O_element
FEATURE [App::DocumentObjectGroupPython] G4_CADMIUM_TUNGSTATE  # scripted group (container) (typed FeaturePython)
  Dunit = g/cm3
  Dvalue = 7.9
  Group = -> [Cd_element002,W_element001,O_element020]
  conduct = 2
  density = 1
  expand = 3
  formula = G4_CADMIUM_TUNGSTATE
  name = G4_CADMIUM_TUNGSTATE
  specific = 4
FEATURE [App::DocumentObjectGroupPython] Ca_element005  label="Ca_element : 1"  # scripted group (container) (typed FeaturePython)
  n = 1
  ref = Ca_element
FEATURE [App::DocumentObjectGroupPython] C_element022  label="C_element : 009"  # scripted group (container) (typed FeaturePython)
  n = 1
  ref = C_element
FEATURE [App::DocumentObjectGroupPython] O_element021  label="O_element : 009"  # scripted group (container) (typed FeaturePython)
  n = 3
  ref = O_element
FEATURE [App::DocumentObjectGroupPython] G4_CALCIUM_CARBONATE  # scripted group (container) (typed FeaturePython)
  Dunit = g/cm3
  Dvalue = 2.8
  Group = -> [Ca_element005,C_element022,O_element021]
  conduct = 2
  density = 1
  expand = 3
  formula = G4_CALCIUM_CARBONATE
  name = G4_CALCIUM_CARBONATE
  specific = 4
FEATURE [App::DocumentObjectGroupPython] Ca_element006  label="Ca_element : 002"  # scripted group (container) (typed FeaturePython)
  n = 1
  ref = Ca_element
FEATURE [App::DocumentObjectGroupPython] F_element005  label="F_element : 003"  # scripted group (container) (typed FeaturePython)
  n = 2
  ref = F_element
FEATURE [App::DocumentObjectGroupPython] G4_CALCIUM_FLUORIDE  # scripted group (container) (typed FeaturePython)
  Dunit = g/cm3
  Dvalue = 3.18
  Group = -> [Ca_element006,F_element005]
  conduct = 2
  density = 1
  expand = 3
  formula = G4_CALCIUM_FLUORIDE
  name = G4_CALCIUM_FLUORIDE
  specific = 4
FEATURE [App::DocumentObjectGroupPython] Ca_element007  label="Ca_element : 003"  # scripted group (container) (typed FeaturePython)
  n = 1
  ref = Ca_element
FEATURE [App::DocumentObjectGroupPython] O_element022  label="O_element : 010"  # scripted group (container) (typed FeaturePython)
  n = 1
  ref = O_element
FEATURE [App::DocumentObjectGroupPython] G4_CALCIUM_OXIDE  # scripted group (container) (typed FeaturePython)
  Dunit = g/cm3
  Dvalue = 3.3
  Group = -> [Ca_element007,O_element022]
  conduct = 2
  density = 1
  expand = 3
  formula = G4_CALCIUM_OXIDE
  name = G4_CALCIUM_OXIDE
  specific = 4
FEATURE [App::DocumentObjectGroupPython] Ca_element008  label="Ca_element : 004"  # scripted group (container) (typed FeaturePython)
  n = 1
  ref = Ca_element
FEATURE [App::DocumentObjectGroupPython] S_element007  label="S_element : 002"  # scripted group (container) (typed FeaturePython)
  n = 1
  ref = S_element
FEATURE [App::DocumentObjectGroupPython] O_element023  label="O_element : 011"  # scripted group (container) (typed FeaturePython)
  n = 4
  ref = O_element
FEATURE [App::DocumentObjectGroupPython] G4_CALCIUM_SULFATE  # scripted group (container) (typed FeaturePython)
  Dunit = g/cm3
  Dvalue = 2.96
  Group = -> [Ca_element008,S_element007,O_element023]
  conduct = 2
  density = 1
  expand = 3
  formula = G4_CALCIUM_SULFATE
  name = G4_CALCIUM_SULFATE
  specific = 4
FEATURE [App::DocumentObjectGroupPython] Ca_element009  label="Ca_element : 005"  # scripted group (container) (typed FeaturePython)
  n = 1
  ref = Ca_element
FEATURE [App::DocumentObjectGroupPython] W_element002  label="W_element : 002"  # scripted group (container) (typed FeaturePython)
  n = 1
  ref = W_element
FEATURE [App::DocumentObjectGroupPython] O_element024  label="O_element : 012"  # scripted group (container) (typed FeaturePython)
  n = 4
  ref = O_element
FEATURE [App::DocumentObjectGroupPython] G4_CALCIUM_TUNGSTATE  # scripted group (container) (typed FeaturePython)
  Dunit = g/cm3
  Dvalue = 6.062
  Group = -> [Ca_element009,W_element002,O_element024]
  conduct = 2
  density = 1
  expand = 3
  formula = G4_CALCIUM_TUNGSTATE
  name = G4_CALCIUM_TUNGSTATE
  specific = 4
FEATURE [App::DocumentObjectGroupPython] C_element023  label="C_element : 010"  # scripted group (container) (typed FeaturePython)
  n = 1
  ref = C_element
FEATURE [App::DocumentObjectGroupPython] O_element025  label="O_element : 013"  # scripted group (container) (typed FeaturePython)
  n = 2
  ref = O_element
FEATURE [App::DocumentObjectGroupPython] G4_CARBON_DIOXIDE  # scripted group (container) (typed FeaturePython)
  Dunit = g/cm3
  Dvalue = 0.00184212
  Group = -> [C_element023,O_element025]
  conduct = 2
  density = 1
  expand = 3
  formula = G4_CARBON_DIOXIDE
  name = G4_CARBON_DIOXIDE
  specific = 4
FEATURE [App::DocumentObjectGroupPython] C_element024  label="C_element : 011"  # scripted group (container) (typed FeaturePython)
  n = 1
  ref = C_element
FEATURE [App::DocumentObjectGroupPython] Cl_element004  label="Cl_element : 4"  # scripted group (container) (typed FeaturePython)
  n = 4
  ref = Cl_element
FEATURE [App::DocumentObjectGroupPython] G4_CARBON_TETRACHLORIDE  # scripted group (container) (typed FeaturePython)
  Dunit = g/cm3
  Dvalue = 1.594
  Group = -> [C_element024,Cl_element004]
  conduct = 2
  density = 1
  expand = 3
  formula = G4_CARBON_TETRACHLORIDE
  name = G4_CARBON_TETRACHLORIDE
  specific = 4
FEATURE [App::DocumentObjectGroupPython] C_element025  label="C_element : 012"  # scripted group (container) (typed FeaturePython)
  n = 6
  ref = C_element
FEATURE [App::DocumentObjectGroupPython] H_element021  label="H_element : 012"  # scripted group (container) (typed FeaturePython)
  n = 10
  ref = H_element
FEATURE [App::DocumentObjectGroupPython] O_element026  label="O_element : 5"  # scripted group (container) (typed FeaturePython)
  n = 5
  ref = O_element
FEATURE [App::DocumentObjectGroupPython] G4_CELLULOSE_CELLOPHANE  # scripted group (container) (typed FeaturePython)
  Dunit = g/cm3
  Dvalue = 1.42
  Group = -> [C_element025,H_element021,O_element026]
  conduct = 2
  density = 1
  expand = 3
  formula = G4_CELLULOSE_CELLOPHANE
  name = G4_CELLULOSE_CELLOPHANE
  specific = 4
FEATURE [App::DocumentObjectGroupPython] H_element022  label="H_element : 0.067"  # scripted group (container) (typed FeaturePython)
  n = 0.067125
FEATURE [App::DocumentObjectGroupPython] C_element026  label="C_element : 0.545"  # scripted group (container) (typed FeaturePython)
  n = 0.545403
FEATURE [App::DocumentObjectGroupPython] O_element027  label="O_element : 0.387"  # scripted group (container) (typed FeaturePython)
  n = 0.387472
FEATURE [App::DocumentObjectGroupPython] G4_CELLULOSE_BUTYRATE  # scripted group (container) (typed FeaturePython)
  Dunit = g/cm3
  Dvalue = 1.2
  Group = -> [H_element022,C_element026,O_element027]
  conduct = 2
  density = 1
  expand = 3
  formula = G4_CELLULOSE_BUTYRATE
  name = G4_CELLULOSE_BUTYRATE
  specific = 4
FEATURE [App::DocumentObjectGroupPython] H_element023  label="H_element : 0.029"  # scripted group (container) (typed FeaturePython)
  n = 0.029216
FEATURE [App::DocumentObjectGroupPython] C_element027  label="C_element : 0.271"  # scripted group (container) (typed FeaturePython)
  n = 0.271296
FEATURE [App::DocumentObjectGroupPython] N_element013  label="N_element : 0.121"  # scripted group (container) (typed FeaturePython)
  n = 0.121276
FEATURE [App::DocumentObjectGroupPython] O_element028  label="O_element : 0.578"  # scripted group (container) (typed FeaturePython)
  n = 0.578212
FEATURE [App::DocumentObjectGroupPython] G4_CELLULOSE_NITRATE  # scripted group (container) (typed FeaturePython)
  Dunit = g/cm3
  Dvalue = 1.49
  Group = -> [H_element023,C_element027,N_element013,O_element028]
  conduct = 2
  density = 1
  expand = 3
  formula = G4_CELLULOSE_NITRATE
  name = G4_CELLULOSE_NITRATE
  specific = 4
FEATURE [App::DocumentObjectGroupPython] H_element024  label="H_element : 0.108"  # scripted group (container) (typed FeaturePython)
  n = 0.107596
FEATURE [App::DocumentObjectGroupPython] N_element014  label="N_element : 0.001"  # scripted group (container) (typed FeaturePython)
  n = 0.0008
FEATURE [App::DocumentObjectGroupPython] O_element029  label="O_element : 0.875"  # scripted group (container) (typed FeaturePython)
  n = 0.874976
FEATURE [App::DocumentObjectGroupPython] S_element008  label="S_element : 0.015"  # scripted group (container) (typed FeaturePython)
  n = 0.014627
FEATURE [App::DocumentObjectGroupPython] Ce_element001  label="Ce_element : 0.002"  # scripted group (container) (typed FeaturePython)
  n = 0.002001
FEATURE [App::DocumentObjectGroupPython] G4_CERIC_SULFATE  # scripted group (container) (typed FeaturePython)
  Dunit = g/cm3
  Dvalue = 1.03
  Group = -> [H_element024,N_element014,O_element029,S_element008,Ce_element001]
  conduct = 2
  density = 1
  expand = 3
  formula = G4_CERIC_SULFATE
  name = G4_CERIC_SULFATE
  specific = 4
FEATURE [App::DocumentObjectGroupPython] Cs_element001  label="Cs_element : 1"  # scripted group (container) (typed FeaturePython)
  n = 1
  ref = Cs_element
FEATURE [App::DocumentObjectGroupPython] F_element006  label="F_element : 1"  # scripted group (container) (typed FeaturePython)
  n = 1
  ref = F_element
FEATURE [App::DocumentObjectGroupPython] G4_CESIUM_FLUORIDE  # scripted group (container) (typed FeaturePython)
  Dunit = g/cm3
  Dvalue = 4.115
  Group = -> [Cs_element001,F_element006]
  conduct = 2
  density = 1
  expand = 3
  formula = G4_CESIUM_FLUORIDE
  name = G4_CESIUM_FLUORIDE
  specific = 4
FEATURE [App::DocumentObjectGroupPython] Cs_element002  label="Cs_element : 002"  # scripted group (container) (typed FeaturePython)
  n = 1
  ref = Cs_element
FEATURE [App::DocumentObjectGroupPython] I_element001  label="I_element : 1"  # scripted group (container) (typed FeaturePython)
  n = 1
  ref = I_element
FEATURE [App::DocumentObjectGroupPython] G4_CESIUM_IODIDE  # scripted group (container) (typed FeaturePython)
  Dunit = g/cm3
  Dvalue = 4.51
  Group = -> [Cs_element002,I_element001]
  conduct = 2
  density = 1
  expand = 3
  formula = G4_CESIUM_IODIDE
  name = G4_CESIUM_IODIDE
  specific = 4
FEATURE [App::DocumentObjectGroupPython] C_element028  label="C_element : 013"  # scripted group (container) (typed FeaturePython)
  n = 6
  ref = C_element
FEATURE [App::DocumentObjectGroupPython] H_element025  label="H_element : 013"  # scripted group (container) (typed FeaturePython)
  n = 5
  ref = H_element
FEATURE [App::DocumentObjectGroupPython] Cl_element005  label="Cl_element : 1"  # scripted group (container) (typed FeaturePython)
  n = 1
  ref = Cl_element
FEATURE [App::DocumentObjectGroupPython] G4_CHLOROBENZENE  # scripted group (container) (typed FeaturePython)
  Dunit = g/cm3
  Dvalue = 1.1058
  Group = -> [C_element028,H_element025,Cl_element005]
  conduct = 2
  density = 1
  expand = 3
  formula = G4_CHLOROBENZENE
  name = G4_CHLOROBENZENE
  specific = 4
FEATURE [App::DocumentObjectGroupPython] C_element029  label="C_element : 014"  # scripted group (container) (typed FeaturePython)
  n = 1
  ref = C_element
FEATURE [App::DocumentObjectGroupPython] H_element026  label="H_element : 1"  # scripted group (container) (typed FeaturePython)
  n = 1
  ref = H_element
FEATURE [App::DocumentObjectGroupPython] Cl_element006  label="Cl_element : 3"  # scripted group (container) (typed FeaturePython)
  n = 3
  ref = Cl_element
FEATURE [App::DocumentObjectGroupPython] G4_CHLOROFORM  # scripted group (container) (typed FeaturePython)
  Dunit = g/cm3
  Dvalue = 1.4832
  Group = -> [C_element029,H_element026,Cl_element006]
  conduct = 2
  density = 1
  expand = 3
  formula = G4_CHLOROFORM
  name = G4_CHLOROFORM
  specific = 4
FEATURE [App::DocumentObjectGroupPython] H_element027  label="H_element : 0.010"  # scripted group (container) (typed FeaturePython)
  n = 0.01
FEATURE [App::DocumentObjectGroupPython] C_element030  label="C_element : 0.001"  # scripted group (container) (typed FeaturePython)
  n = 0.001
FEATURE [App::DocumentObjectGroupPython] O_element030  label="O_element : 0.529"  # scripted group (container) (typed FeaturePython)
  n = 0.529107
FEATURE [App::DocumentObjectGroupPython] Na_element005  label="Na_element : 0.016"  # scripted group (container) (typed FeaturePython)
  n = 0.016
FEATURE [App::DocumentObjectGroupPython] Mg_element003  label="Mg_element : 0.004"  # scripted group (container) (typed FeaturePython)
  n = 0.002
FEATURE [App::DocumentObjectGroupPython] Al_element002  label="Al_element : 0.034"  # scripted group (container) (typed FeaturePython)
  n = 0.033872
FEATURE [App::DocumentObjectGroupPython] Si_element002  label="Si_element : 0.337"  # scripted group (container) (typed FeaturePython)
  n = 0.337021
FEATURE [App::DocumentObjectGroupPython] K_element003  label="K_element : 0.013"  # scripted group (container) (typed FeaturePython)
  n = 0.013
FEATURE [App::DocumentObjectGroupPython] Ca_element010  label="Ca_element : 0.044"  # scripted group (container) (typed FeaturePython)
  n = 0.044
FEATURE [App::DocumentObjectGroupPython] Fe_element002  label="Fe_element : 0.014"  # scripted group (container) (typed FeaturePython)
  n = 0.014
FEATURE [App::DocumentObjectGroupPython] G4_CONCRETE  # scripted group (container) (typed FeaturePython)
  Dunit = g/cm3
  Dvalue = 2.3
  Group = -> [H_element027,C_element030,O_element030,Na_element005,Mg_element003,Al_element002,Si_element002,K_element003,Ca_element010,Fe_element002]
  conduct = 2
  density = 1
  expand = 3
  formula = G4_CONCRETE
  name = G4_CONCRETE
  specific = 4
FEATURE [App::DocumentObjectGroupPython] C_element031  label="C_element : 015"  # scripted group (container) (typed FeaturePython)
  n = 6
  ref = C_element
FEATURE [App::DocumentObjectGroupPython] H_element028  label="H_element : 12"  # scripted group (container) (typed FeaturePython)
  n = 12
  ref = H_element
FEATURE [App::DocumentObjectGroupPython] G4_CYCLOHEXANE  # scripted group (container) (typed FeaturePython)
  Dunit = g/cm3
  Dvalue = 0.779
  Group = -> [C_element031,H_element028]
  conduct = 2
  density = 1
  expand = 3
  formula = G4_CYCLOHEXANE
  name = G4_CYCLOHEXANE
  specific = 4
FEATURE [App::DocumentObjectGroupPython] C_element032  label="C_element : 016"  # scripted group (container) (typed FeaturePython)
  n = 6
  ref = C_element
FEATURE [App::DocumentObjectGroupPython] H_element029  label="H_element : 4"  # scripted group (container) (typed FeaturePython)
  n = 4
  ref = H_element
FEATURE [App::DocumentObjectGroupPython] Cl_element007  label="Cl_element : 2"  # scripted group (container) (typed FeaturePython)
  n = 2
  ref = Cl_element
FEATURE [App::DocumentObjectGroupPython] G4_1_2_DICHLOROBENZENE  label="G4_1.2-DICHLOROBENZENE"  # scripted group (container) (typed FeaturePython)
  Dunit = g/cm3
  Dvalue = 1.3048
  Group = -> [C_element032,H_element029,Cl_element007]
  conduct = 2
  density = 1
  expand = 3
  formula = G4_1.2-DICHLOROBENZENE
  name = G4_1.2-DICHLOROBENZENE
  specific = 4
FEATURE [App::DocumentObjectGroupPython] C_element033  label="C_element : 017"  # scripted group (container) (typed FeaturePython)
  n = 4
  ref = C_element
FEATURE [App::DocumentObjectGroupPython] H_element030  label="H_element : 8"  # scripted group (container) (typed FeaturePython)
  n = 8
  ref = H_element
FEATURE [App::DocumentObjectGroupPython] O_element031  label="O_element : 014"  # scripted group (container) (typed FeaturePython)
  n = 1
  ref = O_element
FEATURE [App::DocumentObjectGroupPython] Cl_element008  label="Cl_element : 005"  # scripted group (container) (typed FeaturePython)
  n = 2
  ref = Cl_element
FEATURE [App::DocumentObjectGroupPython] G4_DICHLORODIETHYL_ETHER  # scripted group (container) (typed FeaturePython)
  Dunit = g/cm3
  Dvalue = 1.2199
  Group = -> [C_element033,H_element030,O_element031,Cl_element008]
  conduct = 2
  density = 1
  expand = 3
  formula = G4_DICHLORODIETHYL_ETHER
  name = G4_DICHLORODIETHYL_ETHER
  specific = 4
FEATURE [App::DocumentObjectGroupPython] C_element034  label="C_element : 018"  # scripted group (container) (typed FeaturePython)
  n = 2
  ref = C_element
FEATURE [App::DocumentObjectGroupPython] H_element031  label="H_element : 014"  # scripted group (container) (typed FeaturePython)
  n = 4
  ref = H_element
FEATURE [App::DocumentObjectGroupPython] Cl_element009  label="Cl_element : 006"  # scripted group (container) (typed FeaturePython)
  n = 2
  ref = Cl_element
FEATURE [App::DocumentObjectGroupPython] G4_1_2_DICHLOROETHANE  label="G4_1.2-DICHLOROETHANE"  # scripted group (container) (typed FeaturePython)
  Dunit = g/cm3
  Dvalue = 1.2351
  Group = -> [C_element034,H_element031,Cl_element009]
  conduct = 2
  density = 1
  expand = 3
  formula = G4_1.2-DICHLOROETHANE
  name = G4_1.2-DICHLOROETHANE
  specific = 4
FEATURE [App::DocumentObjectGroupPython] C_element035  label="C_element : 019"  # scripted group (container) (typed FeaturePython)
  n = 4
  ref = C_element
FEATURE [App::DocumentObjectGroupPython] H_element032  label="H_element : 015"  # scripted group (container) (typed FeaturePython)
  n = 10
  ref = H_element
FEATURE [App::DocumentObjectGroupPython] O_element032  label="O_element : 015"  # scripted group (container) (typed FeaturePython)
  n = 1
  ref = O_element
FEATURE [App::DocumentObjectGroupPython] G4_DIETHYL_ETHER  # scripted group (container) (typed FeaturePython)
  Dunit = g/cm3
  Dvalue = 0.71378
  Group = -> [C_element035,H_element032,O_element032]
  conduct = 2
  density = 1
  expand = 3
  formula = G4_DIETHYL_ETHER
  name = G4_DIETHYL_ETHER
  specific = 4
FEATURE [App::DocumentObjectGroupPython] C_element036  label="C_element : 020"  # scripted group (container) (typed FeaturePython)
  n = 3
  ref = C_element
FEATURE [App::DocumentObjectGroupPython] H_element033  label="H_element : 016"  # scripted group (container) (typed FeaturePython)
  n = 7
  ref = H_element
FEATURE [App::DocumentObjectGroupPython] N_element015  label="N_element : 008"  # scripted group (container) (typed FeaturePython)
  n = 1
  ref = N_element
FEATURE [App::DocumentObjectGroupPython] O_element033  label="O_element : 016"  # scripted group (container) (typed FeaturePython)
  n = 1
  ref = O_element
FEATURE [App::DocumentObjectGroupPython] G4_N_N_DIMETHYL_FORMAMIDE  label="G4_N.N-DIMETHYL_FORMAMIDE"  # scripted group (container) (typed FeaturePython)
  Dunit = g/cm3
  Dvalue = 0.9487
  Group = -> [C_element036,H_element033,N_element015,O_element033]
  conduct = 2
  density = 1
  expand = 3
  formula = G4_N.N-DIMETHYL_FORMAMIDE
  name = G4_N.N-DIMETHYL_FORMAMIDE
  specific = 4
FEATURE [App::DocumentObjectGroupPython] C_element037  label="C_element : 021"  # scripted group (container) (typed FeaturePython)
  n = 2
  ref = C_element
FEATURE [App::DocumentObjectGroupPython] H_element034  label="H_element : 017"  # scripted group (container) (typed FeaturePython)
  n = 6
  ref = H_element
FEATURE [App::DocumentObjectGroupPython] O_element034  label="O_element : 017"  # scripted group (container) (typed FeaturePython)
  n = 1
  ref = O_element
FEATURE [App::DocumentObjectGroupPython] S_element009  label="S_element : 003"  # scripted group (container) (typed FeaturePython)
  n = 1
  ref = S_element
FEATURE [App::DocumentObjectGroupPython] G4_DIMETHYL_SULFOXIDE  # scripted group (container) (typed FeaturePython)
  Dunit = g/cm3
  Dvalue = 1.1014
  Group = -> [C_element037,H_element034,O_element034,S_element009]
  conduct = 2
  density = 1
  expand = 3
  formula = G4_DIMETHYL_SULFOXIDE
  name = G4_DIMETHYL_SULFOXIDE
  specific = 4
FEATURE [App::DocumentObjectGroupPython] C_element038  label="C_element : 022"  # scripted group (container) (typed FeaturePython)
  n = 2
  ref = C_element
FEATURE [App::DocumentObjectGroupPython] H_element035  label="H_element : 018"  # scripted group (container) (typed FeaturePython)
  n = 6
  ref = H_element
FEATURE [App::DocumentObjectGroupPython] G4_ETHANE  # scripted group (container) (typed FeaturePython)
  Dunit = g/cm3
  Dvalue = 0.00125324
  Group = -> [C_element038,H_element035]
  conduct = 2
  density = 1
  expand = 3
  formula = G4_ETHANE
  name = G4_ETHANE
  specific = 4
FEATURE [App::DocumentObjectGroupPython] C_element039  label="C_element : 023"  # scripted group (container) (typed FeaturePython)
  n = 2
  ref = C_element
FEATURE [App::DocumentObjectGroupPython] H_element036  label="H_element : 019"  # scripted group (container) (typed FeaturePython)
  n = 6
  ref = H_element
FEATURE [App::DocumentObjectGroupPython] O_element035  label="O_element : 018"  # scripted group (container) (typed FeaturePython)
  n = 1
  ref = O_element
FEATURE [App::DocumentObjectGroupPython] G4_ETHYL_ALCOHOL  # scripted group (container) (typed FeaturePython)
  Dunit = g/cm3
  Dvalue = 0.7893
  Group = -> [C_element039,H_element036,O_element035]
  conduct = 2
  density = 1
  expand = 3
  formula = G4_ETHYL_ALCOHOL
  name = G4_ETHYL_ALCOHOL
  specific = 4
FEATURE [App::DocumentObjectGroupPython] H_element037  label="H_element : 0.090"  # scripted group (container) (typed FeaturePython)
  n = 0.090027
FEATURE [App::DocumentObjectGroupPython] C_element040  label="C_element : 0.585"  # scripted group (container) (typed FeaturePython)
  n = 0.585182
FEATURE [App::DocumentObjectGroupPython] O_element036  label="O_element : 0.325"  # scripted group (container) (typed FeaturePython)
  n = 0.324791
FEATURE [App::DocumentObjectGroupPython] G4_ETHYL_CELLULOSE  # scripted group (container) (typed FeaturePython)
  Dunit = g/cm3
  Dvalue = 1.13
  Group = -> [H_element037,C_element040,O_element036]
  conduct = 2
  density = 1
  expand = 3
  formula = G4_ETHYL_CELLULOSE
  name = G4_ETHYL_CELLULOSE
  specific = 4
FEATURE [App::DocumentObjectGroupPython] C_element041  label="C_element : 024"  # scripted group (container) (typed FeaturePython)
  n = 2
  ref = C_element
FEATURE [App::DocumentObjectGroupPython] H_element038  label="H_element : 020"  # scripted group (container) (typed FeaturePython)
  n = 4
  ref = H_element
FEATURE [App::DocumentObjectGroupPython] G4_ETHYLENE  # scripted group (container) (typed FeaturePython)
  Dunit = g/cm3
  Dvalue = 0.00117497
  Group = -> [C_element041,H_element038]
  conduct = 2
  density = 1
  expand = 3
  formula = G4_ETHYLENE
  name = G4_ETHYLENE
  specific = 4
FEATURE [App::DocumentObjectGroupPython] H_element039  label="H_element : 0.096"  # scripted group (container) (typed FeaturePython)
  n = 0.096
FEATURE [App::DocumentObjectGroupPython] C_element042  label="C_element : 0.195"  # scripted group (container) (typed FeaturePython)
  n = 0.195
FEATURE [App::DocumentObjectGroupPython] N_element016  label="N_element : 0.057"  # scripted group (container) (typed FeaturePython)
  n = 0.057
FEATURE [App::DocumentObjectGroupPython] O_element037  label="O_element : 0.646"  # scripted group (container) (typed FeaturePython)
  n = 0.646
FEATURE [App::DocumentObjectGroupPython] Na_element006  label="Na_element : 0.017"  # scripted group (container) (typed FeaturePython)
  n = 0.001
FEATURE [App::DocumentObjectGroupPython] P_element005  label="P_element : 0.104"  # scripted group (container) (typed FeaturePython)
  n = 0.001
FEATURE [App::DocumentObjectGroupPython] S_element010  label="S_element : 0.016"  # scripted group (container) (typed FeaturePython)
  n = 0.003
FEATURE [App::DocumentObjectGroupPython] Cl_element010  label="Cl_element : 0.005"  # scripted group (container) (typed FeaturePython)
  n = 0.001
FEATURE [App::DocumentObjectGroupPython] G4_EYE_LENS_ICRP  # scripted group (container) (typed FeaturePython)
  Dunit = g/cm3
  Dvalue = 1.07
  Group = -> [H_element039,C_element042,N_element016,O_element037,Na_element006,P_element005,S_element010,Cl_element010]
  conduct = 2
  density = 1
  expand = 3
  formula = G4_EYE_LENS_ICRP
  name = G4_EYE_LENS_ICRP
  specific = 4
FEATURE [App::DocumentObjectGroupPython] Fe_element003  label="Fe_element : 2"  # scripted group (container) (typed FeaturePython)
  n = 2
  ref = Fe_element
FEATURE [App::DocumentObjectGroupPython] O_element038  label="O_element : 019"  # scripted group (container) (typed FeaturePython)
  n = 3
  ref = O_element
FEATURE [App::DocumentObjectGroupPython] G4_FERRIC_OXIDE  # scripted group (container) (typed FeaturePython)
  Dunit = g/cm3
  Dvalue = 5.2
  Group = -> [Fe_element003,O_element038]
  conduct = 2
  density = 1
  expand = 3
  formula = G4_FERRIC_OXIDE
  name = G4_FERRIC_OXIDE
  specific = 4
FEATURE [App::DocumentObjectGroupPython] Fe_element004  label="Fe_element : 1"  # scripted group (container) (typed FeaturePython)
  n = 1
  ref = Fe_element
FEATURE [App::DocumentObjectGroupPython] B_element003  label="B_element : 1"  # scripted group (container) (typed FeaturePython)
  n = 1
  ref = B_element
FEATURE [App::DocumentObjectGroupPython] G4_FERROBORIDE  # scripted group (container) (typed FeaturePython)
  Dunit = g/cm3
  Dvalue = 7.15
  Group = -> [Fe_element004,B_element003]
  conduct = 2
  density = 1
  expand = 3
  formula = G4_FERROBORIDE
  name = G4_FERROBORIDE
  specific = 4
FEATURE [App::DocumentObjectGroupPython] Fe_element005  label="Fe_element : 003"  # scripted group (container) (typed FeaturePython)
  n = 1
  ref = Fe_element
FEATURE [App::DocumentObjectGroupPython] O_element039  label="O_element : 020"  # scripted group (container) (typed FeaturePython)
  n = 1
  ref = O_element
FEATURE [App::DocumentObjectGroupPython] G4_FERROUS_OXIDE  # scripted group (container) (typed FeaturePython)
  Dunit = g/cm3
  Dvalue = 5.7
  Group = -> [Fe_element005,O_element039]
  conduct = 2
  density = 1
  expand = 3
  formula = G4_FERROUS_OXIDE
  name = G4_FERROUS_OXIDE
  specific = 4
FEATURE [App::DocumentObjectGroupPython] H_element040  label="H_element : 0.115"  # scripted group (container) (typed FeaturePython)
  n = 0.108259
FEATURE [App::DocumentObjectGroupPython] N_element017  label="N_element : 0.000"  # scripted group (container) (typed FeaturePython)
  n = 2.7e-05
FEATURE [App::DocumentObjectGroupPython] O_element040  label="O_element : 0.879"  # scripted group (container) (typed FeaturePython)
  n = 0.878636
FEATURE [App::DocumentObjectGroupPython] Na_element007  label="Na_element : 0.000"  # scripted group (container) (typed FeaturePython)
  n = 2.2e-05
FEATURE [App::DocumentObjectGroupPython] S_element011  label="S_element : 0.013"  # scripted group (container) (typed FeaturePython)
  n = 0.012968
FEATURE [App::DocumentObjectGroupPython] Cl_element011  label="Cl_element : 0.000"  # scripted group (container) (typed FeaturePython)
  n = 3.4e-05
FEATURE [App::DocumentObjectGroupPython] Fe_element006  label="Fe_element : 0.000"  # scripted group (container) (typed FeaturePython)
  n = 5.4e-05
FEATURE [App::DocumentObjectGroupPython] G4_FERROUS_SULFATE  # scripted group (container) (typed FeaturePython)
  Dunit = g/cm3
  Dvalue = 1.024
  Group = -> [H_element040,N_element017,O_element040,Na_element007,S_element011,Cl_element011,Fe_element006]
  conduct = 2
  density = 1
  expand = 3
  formula = G4_FERROUS_SULFATE
  name = G4_FERROUS_SULFATE
  specific = 4
FEATURE [App::DocumentObjectGroupPython] C_element043  label="C_element : 0.099"  # scripted group (container) (typed FeaturePython)
  n = 0.099335
FEATURE [App::DocumentObjectGroupPython] F_element007  label="F_element : 0.314"  # scripted group (container) (typed FeaturePython)
  n = 0.314247
FEATURE [App::DocumentObjectGroupPython] Cl_element012  label="Cl_element : 0.586"  # scripted group (container) (typed FeaturePython)
  n = 0.586418
FEATURE [App::DocumentObjectGroupPython] G4_FREON_12  label="G4_FREON-12"  # scripted group (container) (typed FeaturePython)
  Dunit = g/cm3
  Dvalue = 1.12
  Group = -> [C_element043,F_element007,Cl_element012]
  conduct = 2
  density = 1
  expand = 3
  formula = G4_FREON-12
  name = G4_FREON-12
  specific = 4
FEATURE [App::DocumentObjectGroupPython] C_element044  label="C_element : 0.057"  # scripted group (container) (typed FeaturePython)
  n = 0.057245
FEATURE [App::DocumentObjectGroupPython] F_element008  label="F_element : 0.181"  # scripted group (container) (typed FeaturePython)
  n = 0.181096
FEATURE [App::DocumentObjectGroupPython] Br_element001  label="Br_element : 0.762"  # scripted group (container) (typed FeaturePython)
  n = 0.761659
FEATURE [App::DocumentObjectGroupPython] G4_FREON_12B2  label="G4_FREON-12B2"  # scripted group (container) (typed FeaturePython)
  Dunit = g/cm3
  Dvalue = 1.8
  Group = -> [C_element044,F_element008,Br_element001]
  conduct = 2
  density = 1
  expand = 3
  formula = G4_FREON-12B2
  name = G4_FREON-12B2
  specific = 4
FEATURE [App::DocumentObjectGroupPython] C_element045  label="C_element : 0.115"  # scripted group (container) (typed FeaturePython)
  n = 0.114983
FEATURE [App::DocumentObjectGroupPython] F_element009  label="F_element : 0.546"  # scripted group (container) (typed FeaturePython)
  n = 0.545621
FEATURE [App::DocumentObjectGroupPython] Cl_element013  label="Cl_element : 0.339"  # scripted group (container) (typed FeaturePython)
  n = 0.339396
FEATURE [App::DocumentObjectGroupPython] G4_FREON_13  label="G4_FREON-13"  # scripted group (container) (typed FeaturePython)
  Dunit = g/cm3
  Dvalue = 0.95
  Group = -> [C_element045,F_element009,Cl_element013]
  conduct = 2
  density = 1
  expand = 3
  formula = G4_FREON-13
  name = G4_FREON-13
  specific = 4
FEATURE [App::DocumentObjectGroupPython] C_element046  label="C_element : 025"  # scripted group (container) (typed FeaturePython)
  n = 1
  ref = C_element
FEATURE [App::DocumentObjectGroupPython] F_element010  label="F_element : 3"  # scripted group (container) (typed FeaturePython)
  n = 3
  ref = F_element
FEATURE [App::DocumentObjectGroupPython] Br_element002  label="Br_element : 1"  # scripted group (container) (typed FeaturePython)
  n = 1
  ref = Br_element
FEATURE [App::DocumentObjectGroupPython] G4_FREON_13B1  label="G4_FREON-13B1"  # scripted group (container) (typed FeaturePython)
  Dunit = g/cm3
  Dvalue = 1.5
  Group = -> [C_element046,F_element010,Br_element002]
  conduct = 2
  density = 1
  expand = 3
  formula = G4_FREON-13B1
  name = G4_FREON-13B1
  specific = 4
FEATURE [App::DocumentObjectGroupPython] C_element047  label="C_element : 0.061"  # scripted group (container) (typed FeaturePython)
  n = 0.061309
FEATURE [App::DocumentObjectGroupPython] F_element011  label="F_element : 0.291"  # scripted group (container) (typed FeaturePython)
  n = 0.290924
FEATURE [App::DocumentObjectGroupPython] I_element002  label="I_element : 0.648"  # scripted group (container) (typed FeaturePython)
  n = 0.647767
FEATURE [App::DocumentObjectGroupPython] G4_FREON_13I1  label="G4_FREON-13I1"  # scripted group (container) (typed FeaturePython)
  Dunit = g/cm3
  Dvalue = 1.8
  Group = -> [C_element047,F_element011,I_element002]
  conduct = 2
  density = 1
  expand = 3
  formula = G4_FREON-13I1
  name = G4_FREON-13I1
  specific = 4
FEATURE [App::DocumentObjectGroupPython] Gd_element001  label="Gd_element : 2"  # scripted group (container) (typed FeaturePython)
  n = 2
  ref = Gd_element
FEATURE [App::DocumentObjectGroupPython] O_element041  label="O_element : 021"  # scripted group (container) (typed FeaturePython)
  n = 2
  ref = O_element
FEATURE [App::DocumentObjectGroupPython] S_element012  label="S_element : 004"  # scripted group (container) (typed FeaturePython)
  n = 1
  ref = S_element
FEATURE [App::DocumentObjectGroupPython] G4_GADOLINIUM_OXYSULFIDE  # scripted group (container) (typed FeaturePython)
  Dunit = g/cm3
  Dvalue = 7.44
  Group = -> [Gd_element001,O_element041,S_element012]
  conduct = 2
  density = 1
  expand = 3
  formula = G4_GADOLINIUM_OXYSULFIDE
  name = G4_GADOLINIUM_OXYSULFIDE
  specific = 4
FEATURE [App::DocumentObjectGroupPython] Ga_element001  label="Ga_element : 1"  # scripted group (container) (typed FeaturePython)
  n = 1
  ref = Ga_element
FEATURE [App::DocumentObjectGroupPython] As_element001  label="As_element : 1"  # scripted group (container) (typed FeaturePython)
  n = 1
  ref = As_element
FEATURE [App::DocumentObjectGroupPython] G4_GALLIUM_ARSENIDE  # scripted group (container) (typed FeaturePython)
  Dunit = g/cm3
  Dvalue = 5.31
  Group = -> [Ga_element001,As_element001]
  conduct = 2
  density = 1
  expand = 3
  formula = G4_GALLIUM_ARSENIDE
  name = G4_GALLIUM_ARSENIDE
  specific = 4
FEATURE [App::DocumentObjectGroupPython] H_element041  label="H_element : 0.081"  # scripted group (container) (typed FeaturePython)
  n = 0.08118
FEATURE [App::DocumentObjectGroupPython] C_element048  label="C_element : 0.416"  # scripted group (container) (typed FeaturePython)
  n = 0.41606
FEATURE [App::DocumentObjectGroupPython] N_element018  label="N_element : 0.111"  # scripted group (container) (typed FeaturePython)
  n = 0.11124
FEATURE [App::DocumentObjectGroupPython] O_element042  label="O_element : 0.381"  # scripted group (container) (typed FeaturePython)
  n = 0.38064
FEATURE [App::DocumentObjectGroupPython] S_element013  label="S_element : 0.011"  # scripted group (container) (typed FeaturePython)
  n = 0.01088
FEATURE [App::DocumentObjectGroupPython] G4_GEL_PHOTO_EMULSION  # scripted group (container) (typed FeaturePython)
  Dunit = g/cm3
  Dvalue = 1.2914
  Group = -> [H_element041,C_element048,N_element018,O_element042,S_element013]
  conduct = 2
  density = 1
  expand = 3
  formula = G4_GEL_PHOTO_EMULSION
  name = G4_GEL_PHOTO_EMULSION
  specific = 4
FEATURE [App::DocumentObjectGroupPython] B_element004  label="B_element : 0.040"  # scripted group (container) (typed FeaturePython)
  n = 0.0400639
FEATURE [App::DocumentObjectGroupPython] O_element043  label="O_element : 0.540"  # scripted group (container) (typed FeaturePython)
  n = 0.539561
FEATURE [App::DocumentObjectGroupPython] Na_element008  label="Na_element : 0.028"  # scripted group (container) (typed FeaturePython)
  n = 0.0281909
FEATURE [App::DocumentObjectGroupPython] Al_element003  label="Al_element : 0.012"  # scripted group (container) (typed FeaturePython)
  n = 0.011644
FEATURE [App::DocumentObjectGroupPython] Si_element003  label="Si_element : 0.377"  # scripted group (container) (typed FeaturePython)
  n = 0.377219
FEATURE [App::DocumentObjectGroupPython] K_element004  label="K_element : 0.014"  # scripted group (container) (typed FeaturePython)
  n = 0.00332099
FEATURE [App::DocumentObjectGroupPython] G4_Pyrex_Glass  # scripted group (container) (typed FeaturePython)
  Dunit = g/cm3
  Dvalue = 2.23
  Group = -> [B_element004,O_element043,Na_element008,Al_element003,Si_element003,K_element004]
  conduct = 2
  density = 1
  expand = 3
  formula = G4_Pyrex_Glass
  name = G4_Pyrex_Glass
  specific = 4
FEATURE [App::DocumentObjectGroupPython] O_element044  label="O_element : 0.156"  # scripted group (container) (typed FeaturePython)
  n = 0.156453
FEATURE [App::DocumentObjectGroupPython] Si_element004  label="Si_element : 0.081"  # scripted group (container) (typed FeaturePython)
  n = 0.080866
FEATURE [App::DocumentObjectGroupPython] Ti_element001  label="Ti_element : 0.008"  # scripted group (container) (typed FeaturePython)
  n = 0.008092
FEATURE [App::DocumentObjectGroupPython] As_element002  label="As_element : 0.003"  # scripted group (container) (typed FeaturePython)
  n = 0.002651
FEATURE [App::DocumentObjectGroupPython] Pb_element001  label="Pb_element : 0.752"  # scripted group (container) (typed FeaturePython)
  n = 0.751938
FEATURE [App::DocumentObjectGroupPython] G4_GLASS_LEAD  # scripted group (container) (typed FeaturePython)
  Dunit = g/cm3
  Dvalue = 6.22
  Group = -> [O_element044,Si_element004,Ti_element001,As_element002,Pb_element001]
  conduct = 2
  density = 1
  expand = 3
  formula = G4_GLASS_LEAD
  name = G4_GLASS_LEAD
  specific = 4
FEATURE [App::DocumentObjectGroupPython] O_element045  label="O_element : 0.460"  # scripted group (container) (typed FeaturePython)
  n = 0.4598
FEATURE [App::DocumentObjectGroupPython] Na_element009  label="Na_element : 0.096"  # scripted group (container) (typed FeaturePython)
  n = 0.0964411
FEATURE [App::DocumentObjectGroupPython] Si_element005  label="Si_element : 0.378"  # scripted group (container) (typed FeaturePython)
  n = 0.336553
FEATURE [App::DocumentObjectGroupPython] Ca_element011  label="Ca_element : 0.107"  # scripted group (container) (typed FeaturePython)
  n = 0.107205
FEATURE [App::DocumentObjectGroupPython] G4_GLASS_PLATE  # scripted group (container) (typed FeaturePython)
  Dunit = g/cm3
  Dvalue = 2.4
  Group = -> [O_element045,Na_element009,Si_element005,Ca_element011]
  conduct = 2
  density = 1
  expand = 3
  formula = G4_GLASS_PLATE
  name = G4_GLASS_PLATE
  specific = 4
FEATURE [App::DocumentObjectGroupPython] C_element049  label="C_element : 026"  # scripted group (container) (typed FeaturePython)
  n = 5
  ref = C_element
FEATURE [App::DocumentObjectGroupPython] H_element042  label="H_element : 021"  # scripted group (container) (typed FeaturePython)
  n = 10
  ref = H_element
FEATURE [App::DocumentObjectGroupPython] N_element019  label="N_element : 2"  # scripted group (container) (typed FeaturePython)
  n = 2
  ref = N_element
FEATURE [App::DocumentObjectGroupPython] O_element046  label="O_element : 022"  # scripted group (container) (typed FeaturePython)
  n = 3
  ref = O_element
FEATURE [App::DocumentObjectGroupPython] G4_GLUTAMINE  # scripted group (container) (typed FeaturePython)
  Dunit = g/cm3
  Dvalue = 1.46
  Group = -> [C_element049,H_element042,N_element019,O_element046]
  conduct = 2
  density = 1
  expand = 3
  formula = G4_GLUTAMINE
  name = G4_GLUTAMINE
  specific = 4
FEATURE [App::DocumentObjectGroupPython] C_element050  label="C_element : 027"  # scripted group (container) (typed FeaturePython)
  n = 3
  ref = C_element
FEATURE [App::DocumentObjectGroupPython] H_element043  label="H_element : 022"  # scripted group (container) (typed FeaturePython)
  n = 8
  ref = H_element
FEATURE [App::DocumentObjectGroupPython] O_element047  label="O_element : 023"  # scripted group (container) (typed FeaturePython)
  n = 3
  ref = O_element
FEATURE [App::DocumentObjectGroupPython] G4_GLYCEROL  # scripted group (container) (typed FeaturePython)
  Dunit = g/cm3
  Dvalue = 1.2613
  Group = -> [C_element050,H_element043,O_element047]
  conduct = 2
  density = 1
  expand = 3
  formula = G4_GLYCEROL
  name = G4_GLYCEROL
  specific = 4
FEATURE [App::DocumentObjectGroupPython] C_element051  label="C_element : 028"  # scripted group (container) (typed FeaturePython)
  n = 5
  ref = C_element
FEATURE [App::DocumentObjectGroupPython] H_element044  label="H_element : 023"  # scripted group (container) (typed FeaturePython)
  n = 5
  ref = H_element
FEATURE [App::DocumentObjectGroupPython] N_element020  label="N_element : 009"  # scripted group (container) (typed FeaturePython)
  n = 5
  ref = N_element
FEATURE [App::DocumentObjectGroupPython] O_element048  label="O_element : 024"  # scripted group (container) (typed FeaturePython)
  n = 1
  ref = O_element
FEATURE [App::DocumentObjectGroupPython] G4_GUANINE  # scripted group (container) (typed FeaturePython)
  Dunit = g/cm3
  Dvalue = 2.2
  Group = -> [C_element051,H_element044,N_element020,O_element048]
  conduct = 2
  density = 1
  expand = 3
  formula = G4_GUANINE
  name = G4_GUANINE
  specific = 4
FEATURE [App::DocumentObjectGroupPython] Ca_element012  label="Ca_element : 006"  # scripted group (container) (typed FeaturePython)
  n = 1
  ref = Ca_element
FEATURE [App::DocumentObjectGroupPython] S_element014  label="S_element : 005"  # scripted group (container) (typed FeaturePython)
  n = 1
  ref = S_element
FEATURE [App::DocumentObjectGroupPython] O_element049  label="O_element : 6"  # scripted group (container) (typed FeaturePython)
  n = 6
  ref = O_element
FEATURE [App::DocumentObjectGroupPython] H_element045  label="H_element : 024"  # scripted group (container) (typed FeaturePython)
  n = 4
  ref = H_element
FEATURE [App::DocumentObjectGroupPython] G4_GYPSUM  # scripted group (container) (typed FeaturePython)
  Dunit = g/cm3
  Dvalue = 2.32
  Group = -> [Ca_element012,S_element014,O_element049,H_element045]
  conduct = 2
  density = 1
  expand = 3
  formula = G4_GYPSUM
  name = G4_GYPSUM
  specific = 4
FEATURE [App::DocumentObjectGroupPython] C_element052  label="C_element : 7"  # scripted group (container) (typed FeaturePython)
  n = 7
  ref = C_element
FEATURE [App::DocumentObjectGroupPython] H_element046  label="H_element : 16"  # scripted group (container) (typed FeaturePython)
  n = 16
  ref = H_element
FEATURE [App::DocumentObjectGroupPython] G4_N_HEPTANE  label="G4_N-HEPTANE"  # scripted group (container) (typed FeaturePython)
  Dunit = g/cm3
  Dvalue = 0.68376
  Group = -> [C_element052,H_element046]
  conduct = 2
  density = 1
  expand = 3
  formula = G4_N-HEPTANE
  name = G4_N-HEPTANE
  specific = 4
FEATURE [App::DocumentObjectGroupPython] C_element053  label="C_element : 029"  # scripted group (container) (typed FeaturePython)
  n = 6
  ref = C_element
FEATURE [App::DocumentObjectGroupPython] H_element047  label="H_element : 14"  # scripted group (container) (typed FeaturePython)
  n = 14
  ref = H_element
FEATURE [App::DocumentObjectGroupPython] G4_N_HEXANE  label="G4_N-HEXANE"  # scripted group (container) (typed FeaturePython)
  Dunit = g/cm3
  Dvalue = 0.6603
  Group = -> [C_element053,H_element047]
  conduct = 2
  density = 1
  expand = 3
  formula = G4_N-HEXANE
  name = G4_N-HEXANE
  specific = 4
FEATURE [App::DocumentObjectGroupPython] C_element054  label="C_element : 22"  # scripted group (container) (typed FeaturePython)
  n = 22
  ref = C_element
FEATURE [App::DocumentObjectGroupPython] H_element048  label="H_element : 025"  # scripted group (container) (typed FeaturePython)
  n = 10
  ref = H_element
FEATURE [App::DocumentObjectGroupPython] N_element021  label="N_element : 010"  # scripted group (container) (typed FeaturePython)
  n = 2
  ref = N_element
FEATURE [App::DocumentObjectGroupPython] O_element050  label="O_element : 025"  # scripted group (container) (typed FeaturePython)
  n = 5
  ref = O_element
FEATURE [App::DocumentObjectGroupPython] G4_KAPTON  # scripted group (container) (typed FeaturePython)
  Dunit = g/cm3
  Dvalue = 1.42
  Group = -> [C_element054,H_element048,N_element021,O_element050]
  conduct = 2
  density = 1
  expand = 3
  formula = G4_KAPTON
  name = G4_KAPTON
  specific = 4
FEATURE [App::DocumentObjectGroupPython] La_element001  label="La_element : 1"  # scripted group (container) (typed FeaturePython)
  n = 1
  ref = La_element
FEATURE [App::DocumentObjectGroupPython] Br_element003  label="Br_element : 002"  # scripted group (container) (typed FeaturePython)
  n = 1
  ref = Br_element
FEATURE [App::DocumentObjectGroupPython] O_element051  label="O_element : 026"  # scripted group (container) (typed FeaturePython)
  n = 1
  ref = O_element
FEATURE [App::DocumentObjectGroupPython] G4_LANTHANUM_OXYBROMIDE  # scripted group (container) (typed FeaturePython)
  Dunit = g/cm3
  Dvalue = 6.28
  Group = -> [La_element001,Br_element003,O_element051]
  conduct = 2
  density = 1
  expand = 3
  formula = G4_LANTHANUM_OXYBROMIDE
  name = G4_LANTHANUM_OXYBROMIDE
  specific = 4
FEATURE [App::DocumentObjectGroupPython] La_element002  label="La_element : 2"  # scripted group (container) (typed FeaturePython)
  n = 2
  ref = La_element
FEATURE [App::DocumentObjectGroupPython] O_element052  label="O_element : 027"  # scripted group (container) (typed FeaturePython)
  n = 2
  ref = O_element
FEATURE [App::DocumentObjectGroupPython] S_element015  label="S_element : 006"  # scripted group (container) (typed FeaturePython)
  n = 1
  ref = S_element
FEATURE [App::DocumentObjectGroupPython] G4_LANTHANUM_OXYSULFIDE  # scripted group (container) (typed FeaturePython)
  Dunit = g/cm3
  Dvalue = 5.86
  Group = -> [La_element002,O_element052,S_element015]
  conduct = 2
  density = 1
  expand = 3
  formula = G4_LANTHANUM_OXYSULFIDE
  name = G4_LANTHANUM_OXYSULFIDE
  specific = 4
FEATURE [App::DocumentObjectGroupPython] O_element053  label="O_element : 0.072"  # scripted group (container) (typed FeaturePython)
  n = 0.071682
FEATURE [App::DocumentObjectGroupPython] Pb_element002  label="Pb_element : 0.928"  # scripted group (container) (typed FeaturePython)
  n = 0.928318
FEATURE [App::DocumentObjectGroupPython] G4_LEAD_OXIDE  # scripted group (container) (typed FeaturePython)
  Dunit = g/cm3
  Dvalue = 9.53
  Group = -> [O_element053,Pb_element002]
  conduct = 2
  density = 1
  expand = 3
  formula = G4_LEAD_OXIDE
  name = G4_LEAD_OXIDE
  specific = 4
FEATURE [App::DocumentObjectGroupPython] Li_element001  label="Li_element : 1"  # scripted group (container) (typed FeaturePython)
  n = 1
  ref = Li_element
FEATURE [App::DocumentObjectGroupPython] N_element022  label="N_element : 011"  # scripted group (container) (typed FeaturePython)
  n = 1
  ref = N_element
FEATURE [App::DocumentObjectGroupPython] H_element049  label="H_element : 026"  # scripted group (container) (typed FeaturePython)
  n = 2
  ref = H_element
FEATURE [App::DocumentObjectGroupPython] G4_LITHIUM_AMIDE  # scripted group (container) (typed FeaturePython)
  Dunit = g/cm3
  Dvalue = 1.178
  Group = -> [Li_element001,N_element022,H_element049]
  conduct = 2
  density = 1
  expand = 3
  formula = G4_LITHIUM_AMIDE
  name = G4_LITHIUM_AMIDE
  specific = 4
FEATURE [App::DocumentObjectGroupPython] Li_element002  label="Li_element : 2"  # scripted group (container) (typed FeaturePython)
  n = 2
  ref = Li_element
FEATURE [App::DocumentObjectGroupPython] C_element055  label="C_element : 030"  # scripted group (container) (typed FeaturePython)
  n = 1
  ref = C_element
FEATURE [App::DocumentObjectGroupPython] O_element054  label="O_element : 028"  # scripted group (container) (typed FeaturePython)
  n = 3
  ref = O_element
FEATURE [App::DocumentObjectGroupPython] G4_LITHIUM_CARBONATE  # scripted group (container) (typed FeaturePython)
  Dunit = g/cm3
  Dvalue = 2.11
  Group = -> [Li_element002,C_element055,O_element054]
  conduct = 2
  density = 1
  expand = 3
  formula = G4_LITHIUM_CARBONATE
  name = G4_LITHIUM_CARBONATE
  specific = 4
FEATURE [App::DocumentObjectGroupPython] Li_element003  label="Li_element : 003"  # scripted group (container) (typed FeaturePython)
  n = 1
  ref = Li_element
FEATURE [App::DocumentObjectGroupPython] F_element012  label="F_element : 004"  # scripted group (container) (typed FeaturePython)
  n = 1
  ref = F_element
FEATURE [App::DocumentObjectGroupPython] G4_LITHIUM_FLUORIDE  # scripted group (container) (typed FeaturePython)
  Dunit = g/cm3
  Dvalue = 2.635
  Group = -> [Li_element003,F_element012]
  conduct = 2
  density = 1
  expand = 3
  formula = G4_LITHIUM_FLUORIDE
  name = G4_LITHIUM_FLUORIDE
  specific = 4
FEATURE [App::DocumentObjectGroupPython] Li_element004  label="Li_element : 004"  # scripted group (container) (typed FeaturePython)
  n = 1
  ref = Li_element
FEATURE [App::DocumentObjectGroupPython] H_element050  label="H_element : 027"  # scripted group (container) (typed FeaturePython)
  n = 1
  ref = H_element
FEATURE [App::DocumentObjectGroupPython] G4_LITHIUM_HYDRIDE  # scripted group (container) (typed FeaturePython)
  Dunit = g/cm3
  Dvalue = 0.82
  Group = -> [Li_element004,H_element050]
  conduct = 2
  density = 1
  expand = 3
  formula = G4_LITHIUM_HYDRIDE
  name = G4_LITHIUM_HYDRIDE
  specific = 4
FEATURE [App::DocumentObjectGroupPython] Li_element005  label="Li_element : 005"  # scripted group (container) (typed FeaturePython)
  n = 1
  ref = Li_element
FEATURE [App::DocumentObjectGroupPython] I_element003  label="I_element : 002"  # scripted group (container) (typed FeaturePython)
  n = 1
  ref = I_element
FEATURE [App::DocumentObjectGroupPython] G4_LITHIUM_IODIDE  # scripted group (container) (typed FeaturePython)
  Dunit = g/cm3
  Dvalue = 3.494
  Group = -> [Li_element005,I_element003]
  conduct = 2
  density = 1
  expand = 3
  formula = G4_LITHIUM_IODIDE
  name = G4_LITHIUM_IODIDE
  specific = 4
FEATURE [App::DocumentObjectGroupPython] Li_element006  label="Li_element : 006"  # scripted group (container) (typed FeaturePython)
  n = 2
  ref = Li_element
FEATURE [App::DocumentObjectGroupPython] O_element055  label="O_element : 029"  # scripted group (container) (typed FeaturePython)
  n = 1
  ref = O_element
FEATURE [App::DocumentObjectGroupPython] G4_LITHIUM_OXIDE  # scripted group (container) (typed FeaturePython)
  Dunit = g/cm3
  Dvalue = 2.013
  Group = -> [Li_element006,O_element055]
  conduct = 2
  density = 1
  expand = 3
  formula = G4_LITHIUM_OXIDE
  name = G4_LITHIUM_OXIDE
  specific = 4
FEATURE [App::DocumentObjectGroupPython] Li_element007  label="Li_element : 007"  # scripted group (container) (typed FeaturePython)
  n = 2
  ref = Li_element
FEATURE [App::DocumentObjectGroupPython] B_element005  label="B_element : 005"  # scripted group (container) (typed FeaturePython)
  n = 4
  ref = B_element
FEATURE [App::DocumentObjectGroupPython] O_element056  label="O_element : 7"  # scripted group (container) (typed FeaturePython)
  n = 7
  ref = O_element
FEATURE [App::DocumentObjectGroupPython] G4_LITHIUM_TETRABORATE  # scripted group (container) (typed FeaturePython)
  Dunit = g/cm3
  Dvalue = 2.44
  Group = -> [Li_element007,B_element005,O_element056]
  conduct = 2
  density = 1
  expand = 3
  formula = G4_LITHIUM_TETRABORATE
  name = G4_LITHIUM_TETRABORATE
  specific = 4
FEATURE [App::DocumentObjectGroupPython] H_element051  label="H_element : 0.105"  # scripted group (container) (typed FeaturePython)
  n = 0.105
FEATURE [App::DocumentObjectGroupPython] C_element056  label="C_element : 0.083"  # scripted group (container) (typed FeaturePython)
  n = 0.083
FEATURE [App::DocumentObjectGroupPython] N_element023  label="N_element : 0.023"  # scripted group (container) (typed FeaturePython)
  n = 0.023
FEATURE [App::DocumentObjectGroupPython] O_element057  label="O_element : 0.779"  # scripted group (container) (typed FeaturePython)
  n = 0.779
FEATURE [App::DocumentObjectGroupPython] Na_element010  label="Na_element : 0.097"  # scripted group (container) (typed FeaturePython)
  n = 0.002
FEATURE [App::DocumentObjectGroupPython] P_element006  label="P_element : 0.105"  # scripted group (container) (typed FeaturePython)
  n = 0.001
FEATURE [App::DocumentObjectGroupPython] S_element016  label="S_element : 0.017"  # scripted group (container) (typed FeaturePython)
  n = 0.002
FEATURE [App::DocumentObjectGroupPython] Cl_element014  label="Cl_element : 0.587"  # scripted group (container) (typed FeaturePython)
  n = 0.003
FEATURE [App::DocumentObjectGroupPython] K_element005  label="K_element : 0.015"  # scripted group (container) (typed FeaturePython)
  n = 0.002
FEATURE [App::DocumentObjectGroupPython] G4_LUNG_ICRP  # scripted group (container) (typed FeaturePython)
  Dunit = g/cm3
  Dvalue = 1.04
  Group = -> [H_element051,C_element056,N_element023,O_element057,Na_element010,P_element006,S_element016,Cl_element014,K_element005]
  conduct = 2
  density = 1
  expand = 3
  formula = G4_LUNG_ICRP
  name = G4_LUNG_ICRP
  specific = 4
FEATURE [App::DocumentObjectGroupPython] H_element052  label="H_element : 0.116"  # scripted group (container) (typed FeaturePython)
  n = 0.114318
FEATURE [App::DocumentObjectGroupPython] C_element057  label="C_element : 0.656"  # scripted group (container) (typed FeaturePython)
  n = 0.655824
FEATURE [App::DocumentObjectGroupPython] O_element058  label="O_element : 0.092"  # scripted group (container) (typed FeaturePython)
  n = 0.0921831
FEATURE [App::DocumentObjectGroupPython] Mg_element004  label="Mg_element : 0.135"  # scripted group (container) (typed FeaturePython)
  n = 0.134792
FEATURE [App::DocumentObjectGroupPython] Ca_element013  label="Ca_element : 0.003"  # scripted group (container) (typed FeaturePython)
  n = 0.002883
FEATURE [App::DocumentObjectGroupPython] G4_M3_WAX  # scripted group (container) (typed FeaturePython)
  Dunit = g/cm3
  Dvalue = 1.05
  Group = -> [H_element052,C_element057,O_element058,Mg_element004,Ca_element013]
  conduct = 2
  density = 1
  expand = 3
  formula = G4_M3_WAX
  name = G4_M3_WAX
  specific = 4
FEATURE [App::DocumentObjectGroupPython] Mg_element005  label="Mg_element : 1"  # scripted group (container) (typed FeaturePython)
  n = 1
  ref = Mg_element
FEATURE [App::DocumentObjectGroupPython] C_element058  label="C_element : 031"  # scripted group (container) (typed FeaturePython)
  n = 1
  ref = C_element
FEATURE [App::DocumentObjectGroupPython] O_element059  label="O_element : 030"  # scripted group (container) (typed FeaturePython)
  n = 3
  ref = O_element
FEATURE [App::DocumentObjectGroupPython] G4_MAGNESIUM_CARBONATE  # scripted group (container) (typed FeaturePython)
  Dunit = g/cm3
  Dvalue = 2.958
  Group = -> [Mg_element005,C_element058,O_element059]
  conduct = 2
  density = 1
  expand = 3
  formula = G4_MAGNESIUM_CARBONATE
  name = G4_MAGNESIUM_CARBONATE
  specific = 4
FEATURE [App::DocumentObjectGroupPython] Mg_element006  label="Mg_element : 002"  # scripted group (container) (typed FeaturePython)
  n = 1
  ref = Mg_element
FEATURE [App::DocumentObjectGroupPython] F_element013  label="F_element : 005"  # scripted group (container) (typed FeaturePython)
  n = 2
  ref = F_element
FEATURE [App::DocumentObjectGroupPython] G4_MAGNESIUM_FLUORIDE  # scripted group (container) (typed FeaturePython)
  Dunit = g/cm3
  Dvalue = 3
  Group = -> [Mg_element006,F_element013]
  conduct = 2
  density = 1
  expand = 3
  formula = G4_MAGNESIUM_FLUORIDE
  name = G4_MAGNESIUM_FLUORIDE
  specific = 4
FEATURE [App::DocumentObjectGroupPython] Mg_element007  label="Mg_element : 003"  # scripted group (container) (typed FeaturePython)
  n = 1
  ref = Mg_element
FEATURE [App::DocumentObjectGroupPython] O_element060  label="O_element : 031"  # scripted group (container) (typed FeaturePython)
  n = 1
  ref = O_element
FEATURE [App::DocumentObjectGroupPython] G4_MAGNESIUM_OXIDE  # scripted group (container) (typed FeaturePython)
  Dunit = g/cm3
  Dvalue = 3.58
  Group = -> [Mg_element007,O_element060]
  conduct = 2
  density = 1
  expand = 3
  formula = G4_MAGNESIUM_OXIDE
  name = G4_MAGNESIUM_OXIDE
  specific = 4
FEATURE [App::DocumentObjectGroupPython] Mg_element008  label="Mg_element : 004"  # scripted group (container) (typed FeaturePython)
  n = 1
  ref = Mg_element
FEATURE [App::DocumentObjectGroupPython] B_element006  label="B_element : 006"  # scripted group (container) (typed FeaturePython)
  n = 4
  ref = B_element
FEATURE [App::DocumentObjectGroupPython] O_element061  label="O_element : 032"  # scripted group (container) (typed FeaturePython)
  n = 7
  ref = O_element
FEATURE [App::DocumentObjectGroupPython] G4_MAGNESIUM_TETRABORATE  # scripted group (container) (typed FeaturePython)
  Dunit = g/cm3
  Dvalue = 2.53
  Group = -> [Mg_element008,B_element006,O_element061]
  conduct = 2
  density = 1
  expand = 3
  formula = G4_MAGNESIUM_TETRABORATE
  name = G4_MAGNESIUM_TETRABORATE
  specific = 4
FEATURE [App::DocumentObjectGroupPython] Hg_element001  label="Hg_element : 1"  # scripted group (container) (typed FeaturePython)
  n = 1
  ref = Hg_element
FEATURE [App::DocumentObjectGroupPython] I_element004  label="I_element : 2"  # scripted group (container) (typed FeaturePython)
  n = 2
  ref = I_element
FEATURE [App::DocumentObjectGroupPython] G4_MERCURIC_IODIDE  # scripted group (container) (typed FeaturePython)
  Dunit = g/cm3
  Dvalue = 6.36
  Group = -> [Hg_element001,I_element004]
  conduct = 2
  density = 1
  expand = 3
  formula = G4_MERCURIC_IODIDE
  name = G4_MERCURIC_IODIDE
  specific = 4
FEATURE [App::DocumentObjectGroupPython] C_element059  label="C_element : 032"  # scripted group (container) (typed FeaturePython)
  n = 1
  ref = C_element
FEATURE [App::DocumentObjectGroupPython] H_element053  label="H_element : 028"  # scripted group (container) (typed FeaturePython)
  n = 4
  ref = H_element
FEATURE [App::DocumentObjectGroupPython] G4_METHANE  # scripted group (container) (typed FeaturePython)
  Dunit = g/cm3
  Dvalue = 0.000667151
  Group = -> [C_element059,H_element053]
  conduct = 2
  density = 1
  expand = 3
  formula = G4_METHANE
  name = G4_METHANE
  specific = 4
FEATURE [App::DocumentObjectGroupPython] C_element060  label="C_element : 033"  # scripted group (container) (typed FeaturePython)
  n = 1
  ref = C_element
FEATURE [App::DocumentObjectGroupPython] H_element054  label="H_element : 029"  # scripted group (container) (typed FeaturePython)
  n = 4
  ref = H_element
FEATURE [App::DocumentObjectGroupPython] O_element062  label="O_element : 033"  # scripted group (container) (typed FeaturePython)
  n = 1
  ref = O_element
FEATURE [App::DocumentObjectGroupPython] G4_METHANOL  # scripted group (container) (typed FeaturePython)
  Dunit = g/cm3
  Dvalue = 0.7914
  Group = -> [C_element060,H_element054,O_element062]
  conduct = 2
  density = 1
  expand = 3
  formula = G4_METHANOL
  name = G4_METHANOL
  specific = 4
FEATURE [App::DocumentObjectGroupPython] H_element055  label="H_element : 0.134"  # scripted group (container) (typed FeaturePython)
  n = 0.13404
FEATURE [App::DocumentObjectGroupPython] C_element061  label="C_element : 0.778"  # scripted group (container) (typed FeaturePython)
  n = 0.77796
FEATURE [App::DocumentObjectGroupPython] O_element063  label="O_element : 0.035"  # scripted group (container) (typed FeaturePython)
  n = 0.03502
FEATURE [App::DocumentObjectGroupPython] Mg_element009  label="Mg_element : 0.039"  # scripted group (container) (typed FeaturePython)
  n = 0.038594
FEATURE [App::DocumentObjectGroupPython] Ti_element002  label="Ti_element : 0.014"  # scripted group (container) (typed FeaturePython)
  n = 0.014386
FEATURE [App::DocumentObjectGroupPython] G4_MIX_D_WAX  # scripted group (container) (typed FeaturePython)
  Dunit = g/cm3
  Dvalue = 0.99
  Group = -> [H_element055,C_element061,O_element063,Mg_element009,Ti_element002]
  conduct = 2
  density = 1
  expand = 3
  formula = G4_MIX_D_WAX
  name = G4_MIX_D_WAX
  specific = 4
FEATURE [App::DocumentObjectGroupPython] H_element056  label="H_element : 0.135"  # scripted group (container) (typed FeaturePython)
  n = 0.081192
FEATURE [App::DocumentObjectGroupPython] C_element062  label="C_element : 0.583"  # scripted group (container) (typed FeaturePython)
  n = 0.583442
FEATURE [App::DocumentObjectGroupPython] N_element024  label="N_element : 0.018"  # scripted group (container) (typed FeaturePython)
  n = 0.017798
FEATURE [App::DocumentObjectGroupPython] O_element064  label="O_element : 0.186"  # scripted group (container) (typed FeaturePython)
  n = 0.186381
FEATURE [App::DocumentObjectGroupPython] Mg_element010  label="Mg_element : 0.130"  # scripted group (container) (typed FeaturePython)
  n = 0.130287
FEATURE [App::DocumentObjectGroupPython] Cl_element015  label="Cl_element : 0.588"  # scripted group (container) (typed FeaturePython)
  n = 0.0009
FEATURE [App::DocumentObjectGroupPython] G4_MS20_TISSUE  # scripted group (container) (typed FeaturePython)
  Dunit = g/cm3
  Dvalue = 1
  Group = -> [H_element056,C_element062,N_element024,O_element064,Mg_element010,Cl_element015]
  conduct = 2
  density = 1
  expand = 3
  formula = G4_MS20_TISSUE
  name = G4_MS20_TISSUE
  specific = 4
FEATURE [App::DocumentObjectGroupPython] H_element057  label="H_element : 0.136"  # scripted group (container) (typed FeaturePython)
  n = 0.102
FEATURE [App::DocumentObjectGroupPython] C_element063  label="C_element : 0.143"  # scripted group (container) (typed FeaturePython)
  n = 0.143
FEATURE [App::DocumentObjectGroupPython] N_element025  label="N_element : 0.034"  # scripted group (container) (typed FeaturePython)
  n = 0.034
FEATURE [App::DocumentObjectGroupPython] O_element065  label="O_element : 0.710"  # scripted group (container) (typed FeaturePython)
  n = 0.71
FEATURE [App::DocumentObjectGroupPython] Na_element011  label="Na_element : 0.098"  # scripted group (container) (typed FeaturePython)
  n = 0.001
FEATURE [App::DocumentObjectGroupPython] P_element007  label="P_element : 0.002"  # scripted group (container) (typed FeaturePython)
  n = 0.002
FEATURE [App::DocumentObjectGroupPython] S_element017  label="S_element : 0.018"  # scripted group (container) (typed FeaturePython)
  n = 0.003
FEATURE [App::DocumentObjectGroupPython] Cl_element016  label="Cl_element : 0.589"  # scripted group (container) (typed FeaturePython)
  n = 0.001
FEATURE [App::DocumentObjectGroupPython] K_element006  label="K_element : 0.004"  # scripted group (container) (typed FeaturePython)
  n = 0.004
FEATURE [App::DocumentObjectGroupPython] G4_MUSCLE_SKELETAL_ICRP  # scripted group (container) (typed FeaturePython)
  Dunit = g/cm3
  Dvalue = 1.05
  Group = -> [H_element057,C_element063,N_element025,O_element065,Na_element011,P_element007,S_element017,Cl_element016,K_element006]
  conduct = 2
  density = 1
  expand = 3
  formula = G4_MUSCLE_SKELETAL_ICRP
  name = G4_MUSCLE_SKELETAL_ICRP
  specific = 4
FEATURE [App::DocumentObjectGroupPython] H_element058  label="H_element : 0.137"  # scripted group (container) (typed FeaturePython)
  n = 0.102102
FEATURE [App::DocumentObjectGroupPython] C_element064  label="C_element : 0.123"  # scripted group (container) (typed FeaturePython)
  n = 0.123123
FEATURE [App::DocumentObjectGroupPython] N_element026  label="N_element : 0.756"  # scripted group (container) (typed FeaturePython)
  n = 0.035035
FEATURE [App::DocumentObjectGroupPython] O_element066  label="O_element : 0.730"  # scripted group (container) (typed FeaturePython)
  n = 0.72973
FEATURE [App::DocumentObjectGroupPython] Na_element012  label="Na_element : 0.099"  # scripted group (container) (typed FeaturePython)
  n = 0.001001
FEATURE [App::DocumentObjectGroupPython] P_element008  label="P_element : 0.106"  # scripted group (container) (typed FeaturePython)
  n = 0.002002
FEATURE [App::DocumentObjectGroupPython] S_element018  label="S_element : 0.019"  # scripted group (container) (typed FeaturePython)
  n = 0.004004
FEATURE [App::DocumentObjectGroupPython] K_element007  label="K_element : 0.016"  # scripted group (container) (typed FeaturePython)
  n = 0.003003
FEATURE [App::DocumentObjectGroupPython] G4_MUSCLE_STRIATED_ICRU  # scripted group (container) (typed FeaturePython)
  Dunit = g/cm3
  Dvalue = 1.04
  Group = -> [H_element058,C_element064,N_element026,O_element066,Na_element012,P_element008,S_element018,K_element007]
  conduct = 2
  density = 1
  expand = 3
  formula = G4_MUSCLE_STRIATED_ICRU
  name = G4_MUSCLE_STRIATED_ICRU
  specific = 4
FEATURE [App::DocumentObjectGroupPython] H_element059  label="H_element : 0.098"  # scripted group (container) (typed FeaturePython)
  n = 0.0982341
FEATURE [App::DocumentObjectGroupPython] C_element065  label="C_element : 0.156"  # scripted group (container) (typed FeaturePython)
  n = 0.156214
FEATURE [App::DocumentObjectGroupPython] N_element027  label="N_element : 0.757"  # scripted group (container) (typed FeaturePython)
  n = 0.035451
FEATURE [App::DocumentObjectGroupPython] O_element067  label="O_element : 0.880"  # scripted group (container) (typed FeaturePython)
  n = 0.710101
FEATURE [App::DocumentObjectGroupPython] G4_MUSCLE_WITH_SUCROSE  # scripted group (container) (typed FeaturePython)
  Dunit = g/cm3
  Dvalue = 1.11
  Group = -> [H_element059,C_element065,N_element027,O_element067]
  conduct = 2
  density = 1
  expand = 3
  formula = G4_MUSCLE_WITH_SUCROSE
  name = G4_MUSCLE_WITH_SUCROSE
  specific = 4
FEATURE [App::DocumentObjectGroupPython] H_element060  label="H_element : 0.138"  # scripted group (container) (typed FeaturePython)
  n = 0.101969
FEATURE [App::DocumentObjectGroupPython] C_element066  label="C_element : 0.120"  # scripted group (container) (typed FeaturePython)
  n = 0.120058
FEATURE [App::DocumentObjectGroupPython] N_element028  label="N_element : 0.758"  # scripted group (container) (typed FeaturePython)
  n = 0.035451
FEATURE [App::DocumentObjectGroupPython] O_element068  label="O_element : 0.743"  # scripted group (container) (typed FeaturePython)
  n = 0.742522
FEATURE [App::DocumentObjectGroupPython] G4_MUSCLE_WITHOUT_SUCROSE  # scripted group (container) (typed FeaturePython)
  Dunit = g/cm3
  Dvalue = 1.07
  Group = -> [H_element060,C_element066,N_element028,O_element068]
  conduct = 2
  density = 1
  expand = 3
  formula = G4_MUSCLE_WITHOUT_SUCROSE
  name = G4_MUSCLE_WITHOUT_SUCROSE
  specific = 4
FEATURE [App::DocumentObjectGroupPython] C_element067  label="C_element : 10"  # scripted group (container) (typed FeaturePython)
  n = 10
  ref = C_element
FEATURE [App::DocumentObjectGroupPython] H_element061  label="H_element : 030"  # scripted group (container) (typed FeaturePython)
  n = 8
  ref = H_element
FEATURE [App::DocumentObjectGroupPython] G4_NAPHTHALENE  # scripted group (container) (typed FeaturePython)
  Dunit = g/cm3
  Dvalue = 1.145
  Group = -> [C_element067,H_element061]
  conduct = 2
  density = 1
  expand = 3
  formula = G4_NAPHTHALENE
  name = G4_NAPHTHALENE
  specific = 4
FEATURE [App::DocumentObjectGroupPython] C_element068  label="C_element : 034"  # scripted group (container) (typed FeaturePython)
  n = 6
  ref = C_element
FEATURE [App::DocumentObjectGroupPython] H_element062  label="H_element : 031"  # scripted group (container) (typed FeaturePython)
  n = 5
  ref = H_element
FEATURE [App::DocumentObjectGroupPython] N_element029  label="N_element : 012"  # scripted group (container) (typed FeaturePython)
  n = 1
  ref = N_element
FEATURE [App::DocumentObjectGroupPython] O_element069  label="O_element : 034"  # scripted group (container) (typed FeaturePython)
  n = 2
  ref = O_element
FEATURE [App::DocumentObjectGroupPython] G4_NITROBENZENE  # scripted group (container) (typed FeaturePython)
  Dunit = g/cm3
  Dvalue = 1.19867
  Group = -> [C_element068,H_element062,N_element029,O_element069]
  conduct = 2
  density = 1
  expand = 3
  formula = G4_NITROBENZENE
  name = G4_NITROBENZENE
  specific = 4
FEATURE [App::DocumentObjectGroupPython] N_element030  label="N_element : 013"  # scripted group (container) (typed FeaturePython)
  n = 2
  ref = N_element
FEATURE [App::DocumentObjectGroupPython] O_element070  label="O_element : 035"  # scripted group (container) (typed FeaturePython)
  n = 1
  ref = O_element
FEATURE [App::DocumentObjectGroupPython] G4_NITROUS_OXIDE  # scripted group (container) (typed FeaturePython)
  Dunit = g/cm3
  Dvalue = 0.00183094
  Group = -> [N_element030,O_element070]
  conduct = 2
  density = 1
  expand = 3
  formula = G4_NITROUS_OXIDE
  name = G4_NITROUS_OXIDE
  specific = 4
FEATURE [App::DocumentObjectGroupPython] H_element063  label="H_element : 0.104"  # scripted group (container) (typed FeaturePython)
  n = 0.103509
FEATURE [App::DocumentObjectGroupPython] C_element069  label="C_element : 0.648"  # scripted group (container) (typed FeaturePython)
  n = 0.648416
FEATURE [App::DocumentObjectGroupPython] N_element031  label="N_element : 0.100"  # scripted group (container) (typed FeaturePython)
  n = 0.0995361
FEATURE [App::DocumentObjectGroupPython] O_element071  label="O_element : 0.149"  # scripted group (container) (typed FeaturePython)
  n = 0.148539
FEATURE [App::DocumentObjectGroupPython] G4_NYLON_8062  label="G4_NYLON-8062"  # scripted group (container) (typed FeaturePython)
  Dunit = g/cm3
  Dvalue = 1.08
  Group = -> [H_element063,C_element069,N_element031,O_element071]
  conduct = 2
  density = 1
  expand = 3
  formula = G4_NYLON-8062
  name = G4_NYLON-8062
  specific = 4
FEATURE [App::DocumentObjectGroupPython] C_element070  label="C_element : 035"  # scripted group (container) (typed FeaturePython)
  n = 6
  ref = C_element
FEATURE [App::DocumentObjectGroupPython] H_element064  label="H_element : 11"  # scripted group (container) (typed FeaturePython)
  n = 11
  ref = H_element
FEATURE [App::DocumentObjectGroupPython] N_element032  label="N_element : 014"  # scripted group (container) (typed FeaturePython)
  n = 1
  ref = N_element
FEATURE [App::DocumentObjectGroupPython] O_element072  label="O_element : 036"  # scripted group (container) (typed FeaturePython)
  n = 1
  ref = O_element
FEATURE [App::DocumentObjectGroupPython] G4_NYLON_6_6  label="G4_NYLON-6-6"  # scripted group (container) (typed FeaturePython)
  Dunit = g/cm3
  Dvalue = 1.14
  Group = -> [C_element070,H_element064,N_element032,O_element072]
  conduct = 2
  density = 1
  expand = 3
  formula = G4_NYLON-6-6
  name = G4_NYLON-6-6
  specific = 4
FEATURE [App::DocumentObjectGroupPython] H_element065  label="H_element : 0.139"  # scripted group (container) (typed FeaturePython)
  n = 0.107062
FEATURE [App::DocumentObjectGroupPython] C_element071  label="C_element : 0.680"  # scripted group (container) (typed FeaturePython)
  n = 0.680449
FEATURE [App::DocumentObjectGroupPython] N_element033  label="N_element : 0.099"  # scripted group (container) (typed FeaturePython)
  n = 0.099189
FEATURE [App::DocumentObjectGroupPython] O_element073  label="O_element : 0.113"  # scripted group (container) (typed FeaturePython)
  n = 0.1133
FEATURE [App::DocumentObjectGroupPython] G4_NYLON_6_10  label="G4_NYLON-6-10"  # scripted group (container) (typed FeaturePython)
  Dunit = g/cm3
  Dvalue = 1.14
  Group = -> [H_element065,C_element071,N_element033,O_element073]
  conduct = 2
  density = 1
  expand = 3
  formula = G4_NYLON-6-10
  name = G4_NYLON-6-10
  specific = 4
FEATURE [App::DocumentObjectGroupPython] H_element066  label="H_element : 0.140"  # scripted group (container) (typed FeaturePython)
  n = 0.115476
FEATURE [App::DocumentObjectGroupPython] C_element072  label="C_element : 0.721"  # scripted group (container) (typed FeaturePython)
  n = 0.720818
FEATURE [App::DocumentObjectGroupPython] N_element034  label="N_element : 0.076"  # scripted group (container) (typed FeaturePython)
  n = 0.0764169
FEATURE [App::DocumentObjectGroupPython] O_element074  label="O_element : 0.087"  # scripted group (container) (typed FeaturePython)
  n = 0.0872889
FEATURE [App::DocumentObjectGroupPython] G4_NYLON_11_RILSAN  label="G4_NYLON-11_RILSAN"  # scripted group (container) (typed FeaturePython)
  Dunit = g/cm3
  Dvalue = 1.425
  Group = -> [H_element066,C_element072,N_element034,O_element074]
  conduct = 2
  density = 1
  expand = 3
  formula = G4_NYLON-11_RILSAN
  name = G4_NYLON-11_RILSAN
  specific = 4
FEATURE [App::DocumentObjectGroupPython] C_element073  label="C_element : 8"  # scripted group (container) (typed FeaturePython)
  n = 8
  ref = C_element
FEATURE [App::DocumentObjectGroupPython] H_element067  label="H_element : 18"  # scripted group (container) (typed FeaturePython)
  n = 18
  ref = H_element
FEATURE [App::DocumentObjectGroupPython] G4_OCTANE  # scripted group (container) (typed FeaturePython)
  Dunit = g/cm3
  Dvalue = 0.7026
  Group = -> [C_element073,H_element067]
  conduct = 2
  density = 1
  expand = 3
  formula = G4_OCTANE
  name = G4_OCTANE
  specific = 4
FEATURE [App::DocumentObjectGroupPython] C_element074  label="C_element : 25"  # scripted group (container) (typed FeaturePython)
  n = 25
  ref = C_element
FEATURE [App::DocumentObjectGroupPython] H_element068  label="H_element : 52"  # scripted group (container) (typed FeaturePython)
  n = 52
  ref = H_element
FEATURE [App::DocumentObjectGroupPython] G4_PARAFFIN  # scripted group (container) (typed FeaturePython)
  Dunit = g/cm3
  Dvalue = 0.93
  Group = -> [C_element074,H_element068]
  conduct = 2
  density = 1
  expand = 3
  formula = G4_PARAFFIN
  name = G4_PARAFFIN
  specific = 4
FEATURE [App::DocumentObjectGroupPython] C_element075  label="C_element : 036"  # scripted group (container) (typed FeaturePython)
  n = 5
  ref = C_element
FEATURE [App::DocumentObjectGroupPython] H_element069  label="H_element : 032"  # scripted group (container) (typed FeaturePython)
  n = 12
  ref = H_element
FEATURE [App::DocumentObjectGroupPython] G4_N_PENTANE  label="G4_N-PENTANE"  # scripted group (container) (typed FeaturePython)
  Dunit = g/cm3
  Dvalue = 0.6262
  Group = -> [C_element075,H_element069]
  conduct = 2
  density = 1
  expand = 3
  formula = G4_N-PENTANE
  name = G4_N-PENTANE
  specific = 4
FEATURE [App::DocumentObjectGroupPython] H_element070  label="H_element : 0.014"  # scripted group (container) (typed FeaturePython)
  n = 0.0141
FEATURE [App::DocumentObjectGroupPython] C_element076  label="C_element : 0.072"  # scripted group (container) (typed FeaturePython)
  n = 0.072261
FEATURE [App::DocumentObjectGroupPython] N_element035  label="N_element : 0.019"  # scripted group (container) (typed FeaturePython)
  n = 0.01932
FEATURE [App::DocumentObjectGroupPython] O_element075  label="O_element : 0.066"  # scripted group (container) (typed FeaturePython)
  n = 0.066101
FEATURE [App::DocumentObjectGroupPython] S_element019  label="S_element : 0.020"  # scripted group (container) (typed FeaturePython)
  n = 0.00189
FEATURE [App::DocumentObjectGroupPython] Br_element004  label="Br_element : 0.349"  # scripted group (container) (typed FeaturePython)
  n = 0.349103
FEATURE [App::DocumentObjectGroupPython] Ag_element001  label="Ag_element : 0.474"  # scripted group (container) (typed FeaturePython)
  n = 0.474105
FEATURE [App::DocumentObjectGroupPython] I_element005  label="I_element : 0.003"  # scripted group (container) (typed FeaturePython)
  n = 0.00312
FEATURE [App::DocumentObjectGroupPython] G4_PHOTO_EMULSION  # scripted group (container) (typed FeaturePython)
  Dunit = g/cm3
  Dvalue = 3.815
  Group = -> [H_element070,C_element076,N_element035,O_element075,S_element019,Br_element004,Ag_element001,I_element005]
  conduct = 2
  density = 1
  expand = 3
  formula = G4_PHOTO_EMULSION
  name = G4_PHOTO_EMULSION
  specific = 4
FEATURE [App::DocumentObjectGroupPython] C_element077  label="C_element : 9"  # scripted group (container) (typed FeaturePython)
  n = 9
  ref = C_element
FEATURE [App::DocumentObjectGroupPython] H_element071  label="H_element : 033"  # scripted group (container) (typed FeaturePython)
  n = 10
  ref = H_element
FEATURE [App::DocumentObjectGroupPython] G4_PLASTIC_SC_VINYLTOLUENE  # scripted group (container) (typed FeaturePython)
  Dunit = g/cm3
  Dvalue = 1.032
  Group = -> [C_element077,H_element071]
  conduct = 2
  density = 1
  expand = 3
  formula = G4_PLASTIC_SC_VINYLTOLUENE
  name = G4_PLASTIC_SC_VINYLTOLUENE
  specific = 4
FEATURE [App::DocumentObjectGroupPython] Pu_element001  label="Pu_element : 1"  # scripted group (container) (typed FeaturePython)
  n = 1
  ref = Pu_element
FEATURE [App::DocumentObjectGroupPython] O_element076  label="O_element : 037"  # scripted group (container) (typed FeaturePython)
  n = 2
  ref = O_element
FEATURE [App::DocumentObjectGroupPython] G4_PLUTONIUM_DIOXIDE  # scripted group (container) (typed FeaturePython)
  Dunit = g/cm3
  Dvalue = 11.46
  Group = -> [Pu_element001,O_element076]
  conduct = 2
  density = 1
  expand = 3
  formula = G4_PLUTONIUM_DIOXIDE
  name = G4_PLUTONIUM_DIOXIDE
  specific = 4
FEATURE [App::DocumentObjectGroupPython] C_element078  label="C_element : 037"  # scripted group (container) (typed FeaturePython)
  n = 3
  ref = C_element
FEATURE [App::DocumentObjectGroupPython] H_element072  label="H_element : 034"  # scripted group (container) (typed FeaturePython)
  n = 3
  ref = H_element
FEATURE [App::DocumentObjectGroupPython] N_element036  label="N_element : 015"  # scripted group (container) (typed FeaturePython)
  n = 1
  ref = N_element
FEATURE [App::DocumentObjectGroupPython] G4_POLYACRYLONITRILE  # scripted group (container) (typed FeaturePython)
  Dunit = g/cm3
  Dvalue = 1.17
  Group = -> [C_element078,H_element072,N_element036]
  conduct = 2
  density = 1
  expand = 3
  formula = G4_POLYACRYLONITRILE
  name = G4_POLYACRYLONITRILE
  specific = 4
FEATURE [App::DocumentObjectGroupPython] C_element079  label="C_element : 16"  # scripted group (container) (typed FeaturePython)
  n = 16
  ref = C_element
FEATURE [App::DocumentObjectGroupPython] H_element073  label="H_element : 035"  # scripted group (container) (typed FeaturePython)
  n = 14
  ref = H_element
FEATURE [App::DocumentObjectGroupPython] O_element077  label="O_element : 038"  # scripted group (container) (typed FeaturePython)
  n = 3
  ref = O_element
FEATURE [App::DocumentObjectGroupPython] G4_POLYCARBONATE  # scripted group (container) (typed FeaturePython)
  Dunit = g/cm3
  Dvalue = 1.2
  Group = -> [C_element079,H_element073,O_element077]
  conduct = 2
  density = 1
  expand = 3
  formula = G4_POLYCARBONATE
  name = G4_POLYCARBONATE
  specific = 4
FEATURE [App::DocumentObjectGroupPython] C_element080  label="C_element : 038"  # scripted group (container) (typed FeaturePython)
  n = 8
  ref = C_element
FEATURE [App::DocumentObjectGroupPython] H_element074  label="H_element : 036"  # scripted group (container) (typed FeaturePython)
  n = 7
  ref = H_element
FEATURE [App::DocumentObjectGroupPython] Cl_element017  label="Cl_element : 007"  # scripted group (container) (typed FeaturePython)
  n = 1
  ref = Cl_element
FEATURE [App::DocumentObjectGroupPython] G4_POLYCHLOROSTYRENE  # scripted group (container) (typed FeaturePython)
  Dunit = g/cm3
  Dvalue = 1.3
  Group = -> [C_element080,H_element074,Cl_element017]
  conduct = 2
  density = 1
  expand = 3
  formula = G4_POLYCHLOROSTYRENE
  name = G4_POLYCHLOROSTYRENE
  specific = 4
FEATURE [App::DocumentObjectGroupPython] C_element081  label="C_element : 039"  # scripted group (container) (typed FeaturePython)
  n = 1
  ref = C_element
FEATURE [App::DocumentObjectGroupPython] H_element075  label="H_element : 037"  # scripted group (container) (typed FeaturePython)
  n = 2
  ref = H_element
FEATURE [App::DocumentObjectGroupPython] G4_POLYETHYLENE  # scripted group (container) (typed FeaturePython)
  Dunit = g/cm3
  Dvalue = 0.94
  Group = -> [C_element081,H_element075]
  conduct = 2
  density = 1
  expand = 3
  formula = G4_POLYETHYLENE
  name = G4_POLYETHYLENE
  specific = 4
FEATURE [App::DocumentObjectGroupPython] C_element082  label="C_element : 040"  # scripted group (container) (typed FeaturePython)
  n = 10
  ref = C_element
FEATURE [App::DocumentObjectGroupPython] H_element076  label="H_element : 038"  # scripted group (container) (typed FeaturePython)
  n = 8
  ref = H_element
FEATURE [App::DocumentObjectGroupPython] O_element078  label="O_element : 039"  # scripted group (container) (typed FeaturePython)
  n = 4
  ref = O_element
FEATURE [App::DocumentObjectGroupPython] G4_MYLAR  # scripted group (container) (typed FeaturePython)
  Dunit = g/cm3
  Dvalue = 1.4
  Group = -> [C_element082,H_element076,O_element078]
  conduct = 2
  density = 1
  expand = 3
  formula = G4_MYLAR
  name = G4_MYLAR
  specific = 4
FEATURE [App::DocumentObjectGroupPython] C_element083  label="C_element : 041"  # scripted group (container) (typed FeaturePython)
  n = 5
  ref = C_element
FEATURE [App::DocumentObjectGroupPython] H_element077  label="H_element : 039"  # scripted group (container) (typed FeaturePython)
  n = 8
  ref = H_element
FEATURE [App::DocumentObjectGroupPython] O_element079  label="O_element : 040"  # scripted group (container) (typed FeaturePython)
  n = 2
  ref = O_element
FEATURE [App::DocumentObjectGroupPython] G4_PLEXIGLASS  # scripted group (container) (typed FeaturePython)
  Dunit = g/cm3
  Dvalue = 1.19
  Group = -> [C_element083,H_element077,O_element079]
  conduct = 2
  density = 1
  expand = 3
  formula = G4_PLEXIGLASS
  name = G4_PLEXIGLASS
  specific = 4
FEATURE [App::DocumentObjectGroupPython] C_element084  label="C_element : 042"  # scripted group (container) (typed FeaturePython)
  n = 1
  ref = C_element
FEATURE [App::DocumentObjectGroupPython] H_element078  label="H_element : 040"  # scripted group (container) (typed FeaturePython)
  n = 2
  ref = H_element
FEATURE [App::DocumentObjectGroupPython] O_element080  label="O_element : 041"  # scripted group (container) (typed FeaturePython)
  n = 1
  ref = O_element
FEATURE [App::DocumentObjectGroupPython] G4_POLYOXYMETHYLENE  # scripted group (container) (typed FeaturePython)
  Dunit = g/cm3
  Dvalue = 1.425
  Group = -> [C_element084,H_element078,O_element080]
  conduct = 2
  density = 1
  expand = 3
  formula = G4_POLYOXYMETHYLENE
  name = G4_POLYOXYMETHYLENE
  specific = 4
FEATURE [App::DocumentObjectGroupPython] C_element085  label="C_element : 043"  # scripted group (container) (typed FeaturePython)
  n = 2
  ref = C_element
FEATURE [App::DocumentObjectGroupPython] H_element079  label="H_element : 041"  # scripted group (container) (typed FeaturePython)
  n = 4
  ref = H_element
FEATURE [App::DocumentObjectGroupPython] G4_POLYPROPYLENE  # scripted group (container) (typed FeaturePython)
  Dunit = g/cm3
  Dvalue = 0.9
  Group = -> [C_element085,H_element079]
  conduct = 2
  density = 1
  expand = 3
  formula = G4_POLYPROPYLENE
  name = G4_POLYPROPYLENE
  specific = 4
FEATURE [App::DocumentObjectGroupPython] C_element086  label="C_element : 044"  # scripted group (container) (typed FeaturePython)
  n = 8
  ref = C_element
FEATURE [App::DocumentObjectGroupPython] H_element080  label="H_element : 042"  # scripted group (container) (typed FeaturePython)
  n = 8
  ref = H_element
FEATURE [App::DocumentObjectGroupPython] G4_POLYSTYRENE  # scripted group (container) (typed FeaturePython)
  Dunit = g/cm3
  Dvalue = 1.06
  Group = -> [C_element086,H_element080]
  conduct = 2
  density = 1
  expand = 3
  formula = G4_POLYSTYRENE
  name = G4_POLYSTYRENE
  specific = 4
FEATURE [App::DocumentObjectGroupPython] C_element087  label="C_element : 045"  # scripted group (container) (typed FeaturePython)
  n = 2
  ref = C_element
FEATURE [App::DocumentObjectGroupPython] F_element014  label="F_element : 4"  # scripted group (container) (typed FeaturePython)
  n = 4
  ref = F_element
FEATURE [App::DocumentObjectGroupPython] G4_TEFLON  # scripted group (container) (typed FeaturePython)
  Dunit = g/cm3
  Dvalue = 2.2
  Group = -> [C_element087,F_element014]
  conduct = 2
  density = 1
  expand = 3
  formula = G4_TEFLON
  name = G4_TEFLON
  specific = 4
FEATURE [App::DocumentObjectGroupPython] C_element088  label="C_element : 046"  # scripted group (container) (typed FeaturePython)
  n = 2
  ref = C_element
FEATURE [App::DocumentObjectGroupPython] F_element015  label="F_element : 006"  # scripted group (container) (typed FeaturePython)
  n = 3
  ref = F_element
FEATURE [App::DocumentObjectGroupPython] Cl_element018  label="Cl_element : 008"  # scripted group (container) (typed FeaturePython)
  n = 1
  ref = Cl_element
FEATURE [App::DocumentObjectGroupPython] G4_POLYTRIFLUOROCHLOROETHYLENE  # scripted group (container) (typed FeaturePython)
  Dunit = g/cm3
  Dvalue = 2.1
  Group = -> [C_element088,F_element015,Cl_element018]
  conduct = 2
  density = 1
  expand = 3
  formula = G4_POLYTRIFLUOROCHLOROETHYLENE
  name = G4_POLYTRIFLUOROCHLOROETHYLENE
  specific = 4
FEATURE [App::DocumentObjectGroupPython] C_element089  label="C_element : 047"  # scripted group (container) (typed FeaturePython)
  n = 4
  ref = C_element
FEATURE [App::DocumentObjectGroupPython] H_element081  label="H_element : 043"  # scripted group (container) (typed FeaturePython)
  n = 6
  ref = H_element
FEATURE [App::DocumentObjectGroupPython] O_element081  label="O_element : 042"  # scripted group (container) (typed FeaturePython)
  n = 2
  ref = O_element
FEATURE [App::DocumentObjectGroupPython] G4_POLYVINYL_ACETATE  # scripted group (container) (typed FeaturePython)
  Dunit = g/cm3
  Dvalue = 1.19
  Group = -> [C_element089,H_element081,O_element081]
  conduct = 2
  density = 1
  expand = 3
  formula = G4_POLYVINYL_ACETATE
  name = G4_POLYVINYL_ACETATE
  specific = 4
FEATURE [App::DocumentObjectGroupPython] C_element090  label="C_element : 048"  # scripted group (container) (typed FeaturePython)
  n = 2
  ref = C_element
FEATURE [App::DocumentObjectGroupPython] H_element082  label="H_element : 044"  # scripted group (container) (typed FeaturePython)
  n = 4
  ref = H_element
FEATURE [App::DocumentObjectGroupPython] O_element082  label="O_element : 043"  # scripted group (container) (typed FeaturePython)
  n = 1
  ref = O_element
FEATURE [App::DocumentObjectGroupPython] G4_POLYVINYL_ALCOHOL  # scripted group (container) (typed FeaturePython)
  Dunit = g/cm3
  Dvalue = 1.3
  Group = -> [C_element090,H_element082,O_element082]
  conduct = 2
  density = 1
  expand = 3
  formula = G4_POLYVINYL_ALCOHOL
  name = G4_POLYVINYL_ALCOHOL
  specific = 4
FEATURE [App::DocumentObjectGroupPython] C_element091  label="C_element : 049"  # scripted group (container) (typed FeaturePython)
  n = 8
  ref = C_element
FEATURE [App::DocumentObjectGroupPython] H_element083  label="H_element : 045"  # scripted group (container) (typed FeaturePython)
  n = 14
  ref = H_element
FEATURE [App::DocumentObjectGroupPython] O_element083  label="O_element : 044"  # scripted group (container) (typed FeaturePython)
  n = 2
  ref = O_element
FEATURE [App::DocumentObjectGroupPython] G4_POLYVINYL_BUTYRAL  # scripted group (container) (typed FeaturePython)
  Dunit = g/cm3
  Dvalue = 1.12
  Group = -> [C_element091,H_element083,O_element083]
  conduct = 2
  density = 1
  expand = 3
  formula = G4_POLYVINYL_BUTYRAL
  name = G4_POLYVINYL_BUTYRAL
  specific = 4
FEATURE [App::DocumentObjectGroupPython] C_element092  label="C_element : 050"  # scripted group (container) (typed FeaturePython)
  n = 2
  ref = C_element
FEATURE [App::DocumentObjectGroupPython] H_element084  label="H_element : 046"  # scripted group (container) (typed FeaturePython)
  n = 3
  ref = H_element
FEATURE [App::DocumentObjectGroupPython] Cl_element019  label="Cl_element : 009"  # scripted group (container) (typed FeaturePython)
  n = 1
  ref = Cl_element
FEATURE [App::DocumentObjectGroupPython] G4_POLYVINYL_CHLORIDE  # scripted group (container) (typed FeaturePython)
  Dunit = g/cm3
  Dvalue = 1.3
  Group = -> [C_element092,H_element084,Cl_element019]
  conduct = 2
  density = 1
  expand = 3
  formula = G4_POLYVINYL_CHLORIDE
  name = G4_POLYVINYL_CHLORIDE
  specific = 4
FEATURE [App::DocumentObjectGroupPython] C_element093  label="C_element : 051"  # scripted group (container) (typed FeaturePython)
  n = 2
  ref = C_element
FEATURE [App::DocumentObjectGroupPython] H_element085  label="H_element : 047"  # scripted group (container) (typed FeaturePython)
  n = 2
  ref = H_element
FEATURE [App::DocumentObjectGroupPython] Cl_element020  label="Cl_element : 010"  # scripted group (container) (typed FeaturePython)
  n = 2
  ref = Cl_element
FEATURE [App::DocumentObjectGroupPython] G4_POLYVINYLIDENE_CHLORIDE  # scripted group (container) (typed FeaturePython)
  Dunit = g/cm3
  Dvalue = 1.7
  Group = -> [C_element093,H_element085,Cl_element020]
  conduct = 2
  density = 1
  expand = 3
  formula = G4_POLYVINYLIDENE_CHLORIDE
  name = G4_POLYVINYLIDENE_CHLORIDE
  specific = 4
FEATURE [App::DocumentObjectGroupPython] C_element094  label="C_element : 052"  # scripted group (container) (typed FeaturePython)
  n = 2
  ref = C_element
FEATURE [App::DocumentObjectGroupPython] H_element086  label="H_element : 048"  # scripted group (container) (typed FeaturePython)
  n = 2
  ref = H_element
FEATURE [App::DocumentObjectGroupPython] F_element016  label="F_element : 007"  # scripted group (container) (typed FeaturePython)
  n = 2
  ref = F_element
FEATURE [App::DocumentObjectGroupPython] G4_POLYVINYLIDENE_FLUORIDE  # scripted group (container) (typed FeaturePython)
  Dunit = g/cm3
  Dvalue = 1.76
  Group = -> [C_element094,H_element086,F_element016]
  conduct = 2
  density = 1
  expand = 3
  formula = G4_POLYVINYLIDENE_FLUORIDE
  name = G4_POLYVINYLIDENE_FLUORIDE
  specific = 4
FEATURE [App::DocumentObjectGroupPython] C_element095  label="C_element : 053"  # scripted group (container) (typed FeaturePython)
  n = 6
  ref = C_element
FEATURE [App::DocumentObjectGroupPython] H_element087  label="H_element : 9"  # scripted group (container) (typed FeaturePython)
  n = 9
  ref = H_element
FEATURE [App::DocumentObjectGroupPython] N_element037  label="N_element : 016"  # scripted group (container) (typed FeaturePython)
  n = 1
  ref = N_element
FEATURE [App::DocumentObjectGroupPython] O_element084  label="O_element : 045"  # scripted group (container) (typed FeaturePython)
  n = 1
  ref = O_element
FEATURE [App::DocumentObjectGroupPython] G4_POLYVINYL_PYRROLIDONE  # scripted group (container) (typed FeaturePython)
  Dunit = g/cm3
  Dvalue = 1.25
  Group = -> [C_element095,H_element087,N_element037,O_element084]
  conduct = 2
  density = 1
  expand = 3
  formula = G4_POLYVINYL_PYRROLIDONE
  name = G4_POLYVINYL_PYRROLIDONE
  specific = 4
FEATURE [App::DocumentObjectGroupPython] K_element008  label="K_element : 1"  # scripted group (container) (typed FeaturePython)
  n = 1
  ref = K_element
FEATURE [App::DocumentObjectGroupPython] I_element006  label="I_element : 003"  # scripted group (container) (typed FeaturePython)
  n = 1
  ref = I_element
FEATURE [App::DocumentObjectGroupPython] G4_POTASSIUM_IODIDE  # scripted group (container) (typed FeaturePython)
  Dunit = g/cm3
  Dvalue = 3.13
  Group = -> [K_element008,I_element006]
  conduct = 2
  density = 1
  expand = 3
  formula = G4_POTASSIUM_IODIDE
  name = G4_POTASSIUM_IODIDE
  specific = 4
FEATURE [App::DocumentObjectGroupPython] K_element009  label="K_element : 2"  # scripted group (container) (typed FeaturePython)
  n = 2
  ref = K_element
FEATURE [App::DocumentObjectGroupPython] O_element085  label="O_element : 046"  # scripted group (container) (typed FeaturePython)
  n = 1
  ref = O_element
FEATURE [App::DocumentObjectGroupPython] G4_POTASSIUM_OXIDE  # scripted group (container) (typed FeaturePython)
  Dunit = g/cm3
  Dvalue = 2.32
  Group = -> [K_element009,O_element085]
  conduct = 2
  density = 1
  expand = 3
  formula = G4_POTASSIUM_OXIDE
  name = G4_POTASSIUM_OXIDE
  specific = 4
FEATURE [App::DocumentObjectGroupPython] C_element096  label="C_element : 054"  # scripted group (container) (typed FeaturePython)
  n = 3
  ref = C_element
FEATURE [App::DocumentObjectGroupPython] H_element088  label="H_element : 049"  # scripted group (container) (typed FeaturePython)
  n = 8
  ref = H_element
FEATURE [App::DocumentObjectGroupPython] G4_PROPANE  # scripted group (container) (typed FeaturePython)
  Dunit = g/cm3
  Dvalue = 0.00187939
  Group = -> [C_element096,H_element088]
  conduct = 2
  density = 1
  expand = 3
  formula = G4_PROPANE
  name = G4_PROPANE
  specific = 4
FEATURE [App::DocumentObjectGroupPython] C_element097  label="C_element : 055"  # scripted group (container) (typed FeaturePython)
  n = 3
  ref = C_element
FEATURE [App::DocumentObjectGroupPython] H_element089  label="H_element : 050"  # scripted group (container) (typed FeaturePython)
  n = 8
  ref = H_element
FEATURE [App::DocumentObjectGroupPython] G4_lPROPANE  # scripted group (container) (typed FeaturePython)
  Dunit = g/cm3
  Dvalue = 0.43
  Group = -> [C_element097,H_element089]
  conduct = 2
  density = 1
  expand = 3
  formula = G4_lPROPANE
  name = G4_lPROPANE
  specific = 4
FEATURE [App::DocumentObjectGroupPython] C_element098  label="C_element : 056"  # scripted group (container) (typed FeaturePython)
  n = 3
  ref = C_element
FEATURE [App::DocumentObjectGroupPython] H_element090  label="H_element : 051"  # scripted group (container) (typed FeaturePython)
  n = 8
  ref = H_element
FEATURE [App::DocumentObjectGroupPython] O_element086  label="O_element : 047"  # scripted group (container) (typed FeaturePython)
  n = 1
  ref = O_element
FEATURE [App::DocumentObjectGroupPython] G4_N_PROPYL_ALCOHOL  label="G4_N-PROPYL_ALCOHOL"  # scripted group (container) (typed FeaturePython)
  Dunit = g/cm3
  Dvalue = 0.8035
  Group = -> [C_element098,H_element090,O_element086]
  conduct = 2
  density = 1
  expand = 3
  formula = G4_N-PROPYL_ALCOHOL
  name = G4_N-PROPYL_ALCOHOL
  specific = 4
FEATURE [App::DocumentObjectGroupPython] C_element099  label="C_element : 057"  # scripted group (container) (typed FeaturePython)
  n = 5
  ref = C_element
FEATURE [App::DocumentObjectGroupPython] H_element091  label="H_element : 052"  # scripted group (container) (typed FeaturePython)
  n = 5
  ref = H_element
FEATURE [App::DocumentObjectGroupPython] N_element038  label="N_element : 017"  # scripted group (container) (typed FeaturePython)
  n = 1
  ref = N_element
FEATURE [App::DocumentObjectGroupPython] G4_PYRIDINE  # scripted group (container) (typed FeaturePython)
  Dunit = g/cm3
  Dvalue = 0.9819
  Group = -> [C_element099,H_element091,N_element038]
  conduct = 2
  density = 1
  expand = 3
  formula = G4_PYRIDINE
  name = G4_PYRIDINE
  specific = 4
FEATURE [App::DocumentObjectGroupPython] H_element092  label="H_element : 0.144"  # scripted group (container) (typed FeaturePython)
  n = 0.143711
FEATURE [App::DocumentObjectGroupPython] C_element100  label="C_element : 0.856"  # scripted group (container) (typed FeaturePython)
  n = 0.856289
FEATURE [App::DocumentObjectGroupPython] G4_RUBBER_BUTYL  # scripted group (container) (typed FeaturePython)
  Dunit = g/cm3
  Dvalue = 0.92
  Group = -> [H_element092,C_element100]
  conduct = 2
  density = 1
  expand = 3
  formula = G4_RUBBER_BUTYL
  name = G4_RUBBER_BUTYL
  specific = 4
FEATURE [App::DocumentObjectGroupPython] H_element093  label="H_element : 0.118"  # scripted group (container) (typed FeaturePython)
  n = 0.118371
FEATURE [App::DocumentObjectGroupPython] C_element101  label="C_element : 0.882"  # scripted group (container) (typed FeaturePython)
  n = 0.881629
FEATURE [App::DocumentObjectGroupPython] G4_RUBBER_NATURAL  # scripted group (container) (typed FeaturePython)
  Dunit = g/cm3
  Dvalue = 0.92
  Group = -> [H_element093,C_element101]
  conduct = 2
  density = 1
  expand = 3
  formula = G4_RUBBER_NATURAL
  name = G4_RUBBER_NATURAL
  specific = 4
FEATURE [App::DocumentObjectGroupPython] H_element094  label="H_element : 0.145"  # scripted group (container) (typed FeaturePython)
  n = 0.05692
FEATURE [App::DocumentObjectGroupPython] C_element102  label="C_element : 0.543"  # scripted group (container) (typed FeaturePython)
  n = 0.542646
FEATURE [App::DocumentObjectGroupPython] Cl_element021  label="Cl_element : 0.400"  # scripted group (container) (typed FeaturePython)
  n = 0.400434
FEATURE [App::DocumentObjectGroupPython] G4_RUBBER_NEOPRENE  # scripted group (container) (typed FeaturePython)
  Dunit = g/cm3
  Dvalue = 1.23
  Group = -> [H_element094,C_element102,Cl_element021]
  conduct = 2
  density = 1
  expand = 3
  formula = G4_RUBBER_NEOPRENE
  name = G4_RUBBER_NEOPRENE
  specific = 4
FEATURE [App::DocumentObjectGroupPython] Si_element006  label="Si_element : 1"  # scripted group (container) (typed FeaturePython)
  n = 1
  ref = Si_element
FEATURE [App::DocumentObjectGroupPython] O_element087  label="O_element : 048"  # scripted group (container) (typed FeaturePython)
  n = 2
  ref = O_element
FEATURE [App::DocumentObjectGroupPython] G4_SILICON_DIOXIDE  # scripted group (container) (typed FeaturePython)
  Dunit = g/cm3
  Dvalue = 2.32
  Group = -> [Si_element006,O_element087]
  conduct = 2
  density = 1
  expand = 3
  formula = G4_SILICON_DIOXIDE
  name = G4_SILICON_DIOXIDE
  specific = 4
FEATURE [App::DocumentObjectGroupPython] Ag_element002  label="Ag_element : 1"  # scripted group (container) (typed FeaturePython)
  n = 1
  ref = Ag_element
FEATURE [App::DocumentObjectGroupPython] Br_element005  label="Br_element : 003"  # scripted group (container) (typed FeaturePython)
  n = 1
  ref = Br_element
FEATURE [App::DocumentObjectGroupPython] G4_SILVER_BROMIDE  # scripted group (container) (typed FeaturePython)
  Dunit = g/cm3
  Dvalue = 6.473
  Group = -> [Ag_element002,Br_element005]
  conduct = 2
  density = 1
  expand = 3
  formula = G4_SILVER_BROMIDE
  name = G4_SILVER_BROMIDE
  specific = 4
FEATURE [App::DocumentObjectGroupPython] Ag_element003  label="Ag_element : 002"  # scripted group (container) (typed FeaturePython)
  n = 1
  ref = Ag_element
FEATURE [App::DocumentObjectGroupPython] Cl_element022  label="Cl_element : 011"  # scripted group (container) (typed FeaturePython)
  n = 1
  ref = Cl_element
FEATURE [App::DocumentObjectGroupPython] G4_SILVER_CHLORIDE  # scripted group (container) (typed FeaturePython)
  Dunit = g/cm3
  Dvalue = 5.56
  Group = -> [Ag_element003,Cl_element022]
  conduct = 2
  density = 1
  expand = 3
  formula = G4_SILVER_CHLORIDE
  name = G4_SILVER_CHLORIDE
  specific = 4
FEATURE [App::DocumentObjectGroupPython] Br_element006  label="Br_element : 0.423"  # scripted group (container) (typed FeaturePython)
  n = 0.422895
FEATURE [App::DocumentObjectGroupPython] Ag_element004  label="Ag_element : 0.574"  # scripted group (container) (typed FeaturePython)
  n = 0.573748
FEATURE [App::DocumentObjectGroupPython] I_element007  label="I_element : 0.649"  # scripted group (container) (typed FeaturePython)
  n = 0.003357
FEATURE [App::DocumentObjectGroupPython] G4_SILVER_HALIDES  # scripted group (container) (typed FeaturePython)
  Dunit = g/cm3
  Dvalue = 6.47
  Group = -> [Br_element006,Ag_element004,I_element007]
  conduct = 2
  density = 1
  expand = 3
  formula = G4_SILVER_HALIDES
  name = G4_SILVER_HALIDES
  specific = 4
FEATURE [App::DocumentObjectGroupPython] Ag_element005  label="Ag_element : 003"  # scripted group (container) (typed FeaturePython)
  n = 1
  ref = Ag_element
FEATURE [App::DocumentObjectGroupPython] I_element008  label="I_element : 004"  # scripted group (container) (typed FeaturePython)
  n = 1
  ref = I_element
FEATURE [App::DocumentObjectGroupPython] G4_SILVER_IODIDE  # scripted group (container) (typed FeaturePython)
  Dunit = g/cm3
  Dvalue = 6.01
  Group = -> [Ag_element005,I_element008]
  conduct = 2
  density = 1
  expand = 3
  formula = G4_SILVER_IODIDE
  name = G4_SILVER_IODIDE
  specific = 4
FEATURE [App::DocumentObjectGroupPython] H_element095  label="H_element : 0.100"  # scripted group (container) (typed FeaturePython)
  n = 0.1
FEATURE [App::DocumentObjectGroupPython] C_element103  label="C_element : 0.204"  # scripted group (container) (typed FeaturePython)
  n = 0.204
FEATURE [App::DocumentObjectGroupPython] N_element039  label="N_element : 0.759"  # scripted group (container) (typed FeaturePython)
  n = 0.042
FEATURE [App::DocumentObjectGroupPython] O_element088  label="O_element : 0.645"  # scripted group (container) (typed FeaturePython)
  n = 0.645
FEATURE [App::DocumentObjectGroupPython] Na_element013  label="Na_element : 0.100"  # scripted group (container) (typed FeaturePython)
  n = 0.002
FEATURE [App::DocumentObjectGroupPython] P_element009  label="P_element : 0.107"  # scripted group (container) (typed FeaturePython)
  n = 0.001
FEATURE [App::DocumentObjectGroupPython] S_element020  label="S_element : 0.021"  # scripted group (container) (typed FeaturePython)
  n = 0.002
FEATURE [App::DocumentObjectGroupPython] Cl_element023  label="Cl_element : 0.590"  # scripted group (container) (typed FeaturePython)
  n = 0.003
FEATURE [App::DocumentObjectGroupPython] K_element010  label="K_element : 0.001"  # scripted group (container) (typed FeaturePython)
  n = 0.001
FEATURE [App::DocumentObjectGroupPython] G4_SKIN_ICRP  # scripted group (container) (typed FeaturePython)
  Dunit = g/cm3
  Dvalue = 1.09
  Group = -> [H_element095,C_element103,N_element039,O_element088,Na_element013,P_element009,S_element020,Cl_element023,K_element010]
  conduct = 2
  density = 1
  expand = 3
  formula = G4_SKIN_ICRP
  name = G4_SKIN_ICRP
  specific = 4
FEATURE [App::DocumentObjectGroupPython] Na_element014  label="Na_element : 2"  # scripted group (container) (typed FeaturePython)
  n = 2
  ref = Na_element
FEATURE [App::DocumentObjectGroupPython] C_element104  label="C_element : 058"  # scripted group (container) (typed FeaturePython)
  n = 1
  ref = C_element
FEATURE [App::DocumentObjectGroupPython] O_element089  label="O_element : 049"  # scripted group (container) (typed FeaturePython)
  n = 3
  ref = O_element
FEATURE [App::DocumentObjectGroupPython] G4_SODIUM_CARBONATE  # scripted group (container) (typed FeaturePython)
  Dunit = g/cm3
  Dvalue = 2.532
  Group = -> [Na_element014,C_element104,O_element089]
  conduct = 2
  density = 1
  expand = 3
  formula = G4_SODIUM_CARBONATE
  name = G4_SODIUM_CARBONATE
  specific = 4
FEATURE [App::DocumentObjectGroupPython] Na_element015  label="Na_element : 1"  # scripted group (container) (typed FeaturePython)
  n = 1
  ref = Na_element
FEATURE [App::DocumentObjectGroupPython] I_element009  label="I_element : 005"  # scripted group (container) (typed FeaturePython)
  n = 1
  ref = I_element
FEATURE [App::DocumentObjectGroupPython] G4_SODIUM_IODIDE  # scripted group (container) (typed FeaturePython)
  Dunit = g/cm3
  Dvalue = 3.667
  Group = -> [Na_element015,I_element009]
  conduct = 2
  density = 1
  expand = 3
  formula = G4_SODIUM_IODIDE
  name = G4_SODIUM_IODIDE
  specific = 4
FEATURE [App::DocumentObjectGroupPython] Na_element016  label="Na_element : 003"  # scripted group (container) (typed FeaturePython)
  n = 2
  ref = Na_element
FEATURE [App::DocumentObjectGroupPython] O_element090  label="O_element : 050"  # scripted group (container) (typed FeaturePython)
  n = 1
  ref = O_element
FEATURE [App::DocumentObjectGroupPython] G4_SODIUM_MONOXIDE  # scripted group (container) (typed FeaturePython)
  Dunit = g/cm3
  Dvalue = 2.27
  Group = -> [Na_element016,O_element090]
  conduct = 2
  density = 1
  expand = 3
  formula = G4_SODIUM_MONOXIDE
  name = G4_SODIUM_MONOXIDE
  specific = 4
FEATURE [App::DocumentObjectGroupPython] Na_element017  label="Na_element : 004"  # scripted group (container) (typed FeaturePython)
  n = 1
  ref = Na_element
FEATURE [App::DocumentObjectGroupPython] N_element040  label="N_element : 018"  # scripted group (container) (typed FeaturePython)
  n = 1
  ref = N_element
FEATURE [App::DocumentObjectGroupPython] O_element091  label="O_element : 051"  # scripted group (container) (typed FeaturePython)
  n = 3
  ref = O_element
FEATURE [App::DocumentObjectGroupPython] G4_SODIUM_NITRATE  # scripted group (container) (typed FeaturePython)
  Dunit = g/cm3
  Dvalue = 2.261
  Group = -> [Na_element017,N_element040,O_element091]
  conduct = 2
  density = 1
  expand = 3
  formula = G4_SODIUM_NITRATE
  name = G4_SODIUM_NITRATE
  specific = 4
FEATURE [App::DocumentObjectGroupPython] C_element105  label="C_element : 059"  # scripted group (container) (typed FeaturePython)
  n = 14
  ref = C_element
FEATURE [App::DocumentObjectGroupPython] H_element096  label="H_element : 053"  # scripted group (container) (typed FeaturePython)
  n = 12
  ref = H_element
FEATURE [App::DocumentObjectGroupPython] G4_STILBENE  # scripted group (container) (typed FeaturePython)
  Dunit = g/cm3
  Dvalue = 0.9707
  Group = -> [C_element105,H_element096]
  conduct = 2
  density = 1
  expand = 3
  formula = G4_STILBENE
  name = G4_STILBENE
  specific = 4
FEATURE [App::DocumentObjectGroupPython] C_element106  label="C_element : 12"  # scripted group (container) (typed FeaturePython)
  n = 12
  ref = C_element
FEATURE [App::DocumentObjectGroupPython] H_element097  label="H_element : 22"  # scripted group (container) (typed FeaturePython)
  n = 22
  ref = H_element
FEATURE [App::DocumentObjectGroupPython] O_element092  label="O_element : 11"  # scripted group (container) (typed FeaturePython)
  n = 11
  ref = O_element
FEATURE [App::DocumentObjectGroupPython] G4_SUCROSE  # scripted group (container) (typed FeaturePython)
  Dunit = g/cm3
  Dvalue = 1.5805
  Group = -> [C_element106,H_element097,O_element092]
  conduct = 2
  density = 1
  expand = 3
  formula = G4_SUCROSE
  name = G4_SUCROSE
  specific = 4
FEATURE [App::DocumentObjectGroupPython] C_element107  label="C_element : 18"  # scripted group (container) (typed FeaturePython)
  n = 18
  ref = C_element
FEATURE [App::DocumentObjectGroupPython] H_element098  label="H_element : 054"  # scripted group (container) (typed FeaturePython)
  n = 14
  ref = H_element
FEATURE [App::DocumentObjectGroupPython] G4_TERPHENYL  # scripted group (container) (typed FeaturePython)
  Dunit = g/cm3
  Dvalue = 1.24
  Group = -> [C_element107,H_element098]
  conduct = 2
  density = 1
  expand = 3
  formula = G4_TERPHENYL
  name = G4_TERPHENYL
  specific = 4
FEATURE [App::DocumentObjectGroupPython] H_element099  label="H_element : 0.146"  # scripted group (container) (typed FeaturePython)
  n = 0.106
FEATURE [App::DocumentObjectGroupPython] C_element108  label="C_element : 0.883"  # scripted group (container) (typed FeaturePython)
  n = 0.099
FEATURE [App::DocumentObjectGroupPython] N_element041  label="N_element : 0.020"  # scripted group (container) (typed FeaturePython)
  n = 0.02
FEATURE [App::DocumentObjectGroupPython] O_element093  label="O_element : 0.766"  # scripted group (container) (typed FeaturePython)
  n = 0.766
FEATURE [App::DocumentObjectGroupPython] Na_element018  label="Na_element : 0.101"  # scripted group (container) (typed FeaturePython)
  n = 0.002
FEATURE [App::DocumentObjectGroupPython] P_element010  label="P_element : 0.108"  # scripted group (container) (typed FeaturePython)
  n = 0.001
FEATURE [App::DocumentObjectGroupPython] S_element021  label="S_element : 0.022"  # scripted group (container) (typed FeaturePython)
  n = 0.002
FEATURE [App::DocumentObjectGroupPython] Cl_element024  label="Cl_element : 0.002"  # scripted group (container) (typed FeaturePython)
  n = 0.002
FEATURE [App::DocumentObjectGroupPython] K_element011  label="K_element : 0.017"  # scripted group (container) (typed FeaturePython)
  n = 0.002
FEATURE [App::DocumentObjectGroupPython] G4_TESTIS_ICRP  # scripted group (container) (typed FeaturePython)
  Dunit = g/cm3
  Dvalue = 1.04
  Group = -> [H_element099,C_element108,N_element041,O_element093,Na_element018,P_element010,S_element021,Cl_element024,K_element011]
  conduct = 2
  density = 1
  expand = 3
  formula = G4_TESTIS_ICRP
  name = G4_TESTIS_ICRP
  specific = 4
FEATURE [App::DocumentObjectGroupPython] C_element109  label="C_element : 060"  # scripted group (container) (typed FeaturePython)
  n = 2
  ref = C_element
FEATURE [App::DocumentObjectGroupPython] Cl_element025  label="Cl_element : 012"  # scripted group (container) (typed FeaturePython)
  n = 4
  ref = Cl_element
FEATURE [App::DocumentObjectGroupPython] G4_TETRACHLOROETHYLENE  # scripted group (container) (typed FeaturePython)
  Dunit = g/cm3
  Dvalue = 1.625
  Group = -> [C_element109,Cl_element025]
  conduct = 2
  density = 1
  expand = 3
  formula = G4_TETRACHLOROETHYLENE
  name = G4_TETRACHLOROETHYLENE
  specific = 4
FEATURE [App::DocumentObjectGroupPython] Tl_element001  label="Tl_element : 1"  # scripted group (container) (typed FeaturePython)
  n = 1
  ref = Tl_element
FEATURE [App::DocumentObjectGroupPython] Cl_element026  label="Cl_element : 013"  # scripted group (container) (typed FeaturePython)
  n = 1
  ref = Cl_element
FEATURE [App::DocumentObjectGroupPython] G4_THALLIUM_CHLORIDE  # scripted group (container) (typed FeaturePython)
  Dunit = g/cm3
  Dvalue = 7.004
  Group = -> [Tl_element001,Cl_element026]
  conduct = 2
  density = 1
  expand = 3
  formula = G4_THALLIUM_CHLORIDE
  name = G4_THALLIUM_CHLORIDE
  specific = 4
FEATURE [App::DocumentObjectGroupPython] H_element100  label="H_element : 0.147"  # scripted group (container) (typed FeaturePython)
  n = 0.105
FEATURE [App::DocumentObjectGroupPython] C_element110  label="C_element : 0.256"  # scripted group (container) (typed FeaturePython)
  n = 0.256
FEATURE [App::DocumentObjectGroupPython] N_element042  label="N_element : 0.760"  # scripted group (container) (typed FeaturePython)
  n = 0.027
FEATURE [App::DocumentObjectGroupPython] O_element094  label="O_element : 0.602"  # scripted group (container) (typed FeaturePython)
  n = 0.602
FEATURE [App::DocumentObjectGroupPython] Na_element019  label="Na_element : 0.102"  # scripted group (container) (typed FeaturePython)
  n = 0.001
FEATURE [App::DocumentObjectGroupPython] P_element011  label="P_element : 0.109"  # scripted group (container) (typed FeaturePython)
  n = 0.002
FEATURE [App::DocumentObjectGroupPython] S_element022  label="S_element : 0.023"  # scripted group (container) (typed FeaturePython)
  n = 0.003
FEATURE [App::DocumentObjectGroupPython] Cl_element027  label="Cl_element : 0.591"  # scripted group (container) (typed FeaturePython)
  n = 0.002
FEATURE [App::DocumentObjectGroupPython] K_element012  label="K_element : 0.018"  # scripted group (container) (typed FeaturePython)
  n = 0.002
FEATURE [App::DocumentObjectGroupPython] G4_TISSUE_SOFT_ICRP  # scripted group (container) (typed FeaturePython)
  Dunit = g/cm3
  Dvalue = 1.03
  Group = -> [H_element100,C_element110,N_element042,O_element094,Na_element019,P_element011,S_element022,Cl_element027,K_element012]
  conduct = 2
  density = 1
  expand = 3
  formula = G4_TISSUE_SOFT_ICRP
  name = G4_TISSUE_SOFT_ICRP
  specific = 4
FEATURE [App::DocumentObjectGroupPython] H_element101  label="H_element : 0.148"  # scripted group (container) (typed FeaturePython)
  n = 0.101
FEATURE [App::DocumentObjectGroupPython] C_element111  label="C_element : 0.111"  # scripted group (container) (typed FeaturePython)
  n = 0.111
FEATURE [App::DocumentObjectGroupPython] N_element043  label="N_element : 0.026"  # scripted group (container) (typed FeaturePython)
  n = 0.026
FEATURE [App::DocumentObjectGroupPython] O_element095  label="O_element : 0.762"  # scripted group (container) (typed FeaturePython)
  n = 0.762
FEATURE [App::DocumentObjectGroupPython] G4_TISSUE_SOFT_ICRU_4  label="G4_TISSUE_SOFT_ICRU-4"  # scripted group (container) (typed FeaturePython)
  Dunit = g/cm3
  Dvalue = 1
  Group = -> [H_element101,C_element111,N_element043,O_element095]
  conduct = 2
  density = 1
  expand = 3
  formula = G4_TISSUE_SOFT_ICRU-4
  name = G4_TISSUE_SOFT_ICRU-4
  specific = 4
FEATURE [App::DocumentObjectGroupPython] H_element102  label="H_element : 0.149"  # scripted group (container) (typed FeaturePython)
  n = 0.101869
FEATURE [App::DocumentObjectGroupPython] C_element112  label="C_element : 0.456"  # scripted group (container) (typed FeaturePython)
  n = 0.456179
FEATURE [App::DocumentObjectGroupPython] N_element044  label="N_element : 0.761"  # scripted group (container) (typed FeaturePython)
  n = 0.035172
FEATURE [App::DocumentObjectGroupPython] O_element096  label="O_element : 0.407"  # scripted group (container) (typed FeaturePython)
  n = 0.40678
FEATURE [App::DocumentObjectGroupPython] G4_TISSUE_METHANE  label="G4_TISSUE-METHANE"  # scripted group (container) (typed FeaturePython)
  Dunit = g/cm3
  Dvalue = 0.00106409
  Group = -> [H_element102,C_element112,N_element044,O_element096]
  conduct = 2
  density = 1
  expand = 3
  formula = G4_TISSUE-METHANE
  name = G4_TISSUE-METHANE
  specific = 4
FEATURE [App::DocumentObjectGroupPython] H_element103  label="H_element : 0.103"  # scripted group (container) (typed FeaturePython)
  n = 0.102672
FEATURE [App::DocumentObjectGroupPython] C_element113  label="C_element : 0.569"  # scripted group (container) (typed FeaturePython)
  n = 0.56894
FEATURE [App::DocumentObjectGroupPython] N_element045  label="N_element : 0.762"  # scripted group (container) (typed FeaturePython)
  n = 0.035022
FEATURE [App::DocumentObjectGroupPython] O_element097  label="O_element : 0.293"  # scripted group (container) (typed FeaturePython)
  n = 0.293366
FEATURE [App::DocumentObjectGroupPython] G4_TISSUE_PROPANE  label="G4_TISSUE-PROPANE"  # scripted group (container) (typed FeaturePython)
  Dunit = g/cm3
  Dvalue = 0.00182628
  Group = -> [H_element103,C_element113,N_element045,O_element097]
  conduct = 2
  density = 1
  expand = 3
  formula = G4_TISSUE-PROPANE
  name = G4_TISSUE-PROPANE
  specific = 4
FEATURE [App::DocumentObjectGroupPython] Ti_element003  label="Ti_element : 1"  # scripted group (container) (typed FeaturePython)
  n = 1
  ref = Ti_element
FEATURE [App::DocumentObjectGroupPython] O_element098  label="O_element : 052"  # scripted group (container) (typed FeaturePython)
  n = 2
  ref = O_element
FEATURE [App::DocumentObjectGroupPython] G4_TITANIUM_DIOXIDE  # scripted group (container) (typed FeaturePython)
  Dunit = g/cm3
  Dvalue = 4.26
  Group = -> [Ti_element003,O_element098]
  conduct = 2
  density = 1
  expand = 3
  formula = G4_TITANIUM_DIOXIDE
  name = G4_TITANIUM_DIOXIDE
  specific = 4
FEATURE [App::DocumentObjectGroupPython] C_element114  label="C_element : 061"  # scripted group (container) (typed FeaturePython)
  n = 7
  ref = C_element
FEATURE [App::DocumentObjectGroupPython] H_element104  label="H_element : 055"  # scripted group (container) (typed FeaturePython)
  n = 8
  ref = H_element
FEATURE [App::DocumentObjectGroupPython] G4_TOLUENE  # scripted group (container) (typed FeaturePython)
  Dunit = g/cm3
  Dvalue = 0.8669
  Group = -> [C_element114,H_element104]
  conduct = 2
  density = 1
  expand = 3
  formula = G4_TOLUENE
  name = G4_TOLUENE
  specific = 4
FEATURE [App::DocumentObjectGroupPython] C_element115  label="C_element : 062"  # scripted group (container) (typed FeaturePython)
  n = 2
  ref = C_element
FEATURE [App::DocumentObjectGroupPython] H_element105  label="H_element : 056"  # scripted group (container) (typed FeaturePython)
  n = 1
  ref = H_element
FEATURE [App::DocumentObjectGroupPython] Cl_element028  label="Cl_element : 014"  # scripted group (container) (typed FeaturePython)
  n = 3
  ref = Cl_element
FEATURE [App::DocumentObjectGroupPython] G4_TRICHLOROETHYLENE  # scripted group (container) (typed FeaturePython)
  Dunit = g/cm3
  Dvalue = 1.46
  Group = -> [C_element115,H_element105,Cl_element028]
  conduct = 2
  density = 1
  expand = 3
  formula = G4_TRICHLOROETHYLENE
  name = G4_TRICHLOROETHYLENE
  specific = 4
FEATURE [App::DocumentObjectGroupPython] C_element116  label="C_element : 063"  # scripted group (container) (typed FeaturePython)
  n = 6
  ref = C_element
FEATURE [App::DocumentObjectGroupPython] H_element106  label="H_element : 15"  # scripted group (container) (typed FeaturePython)
  n = 15
  ref = H_element
FEATURE [App::DocumentObjectGroupPython] O_element099  label="O_element : 053"  # scripted group (container) (typed FeaturePython)
  n = 4
  ref = O_element
FEATURE [App::DocumentObjectGroupPython] P_element012  label="P_element : 1"  # scripted group (container) (typed FeaturePython)
  n = 1
  ref = P_element
FEATURE [App::DocumentObjectGroupPython] G4_TRIETHYL_PHOSPHATE  # scripted group (container) (typed FeaturePython)
  Dunit = g/cm3
  Dvalue = 1.07
  Group = -> [C_element116,H_element106,O_element099,P_element012]
  conduct = 2
  density = 1
  expand = 3
  formula = G4_TRIETHYL_PHOSPHATE
  name = G4_TRIETHYL_PHOSPHATE
  specific = 4
FEATURE [App::DocumentObjectGroupPython] W_element003  label="W_element : 003"  # scripted group (container) (typed FeaturePython)
  n = 1
  ref = W_element
FEATURE [App::DocumentObjectGroupPython] F_element017  label="F_element : 6"  # scripted group (container) (typed FeaturePython)
  n = 6
  ref = F_element
FEATURE [App::DocumentObjectGroupPython] G4_TUNGSTEN_HEXAFLUORIDE  # scripted group (container) (typed FeaturePython)
  Dunit = g/cm3
  Dvalue = 2.4
  Group = -> [W_element003,F_element017]
  conduct = 2
  density = 1
  expand = 3
  formula = G4_TUNGSTEN_HEXAFLUORIDE
  name = G4_TUNGSTEN_HEXAFLUORIDE
  specific = 4
FEATURE [App::DocumentObjectGroupPython] U_element001  label="U_element : 1"  # scripted group (container) (typed FeaturePython)
  n = 1
  ref = U_element
FEATURE [App::DocumentObjectGroupPython] C_element117  label="C_element : 064"  # scripted group (container) (typed FeaturePython)
  n = 2
  ref = C_element
FEATURE [App::DocumentObjectGroupPython] G4_URANIUM_DICARBIDE  # scripted group (container) (typed FeaturePython)
  Dunit = g/cm3
  Dvalue = 11.28
  Group = -> [U_element001,C_element117]
  conduct = 2
  density = 1
  expand = 3
  formula = G4_URANIUM_DICARBIDE
  name = G4_URANIUM_DICARBIDE
  specific = 4
FEATURE [App::DocumentObjectGroupPython] U_element002  label="U_element : 002"  # scripted group (container) (typed FeaturePython)
  n = 1
  ref = U_element
FEATURE [App::DocumentObjectGroupPython] C_element118  label="C_element : 065"  # scripted group (container) (typed FeaturePython)
  n = 1
  ref = C_element
FEATURE [App::DocumentObjectGroupPython] G4_URANIUM_MONOCARBIDE  # scripted group (container) (typed FeaturePython)
  Dunit = g/cm3
  Dvalue = 13.63
  Group = -> [U_element002,C_element118]
  conduct = 2
  density = 1
  expand = 3
  formula = G4_URANIUM_MONOCARBIDE
  name = G4_URANIUM_MONOCARBIDE
  specific = 4
FEATURE [App::DocumentObjectGroupPython] U_element003  label="U_element : 003"  # scripted group (container) (typed FeaturePython)
  n = 1
  ref = U_element
FEATURE [App::DocumentObjectGroupPython] O_element100  label="O_element : 054"  # scripted group (container) (typed FeaturePython)
  n = 2
  ref = O_element
FEATURE [App::DocumentObjectGroupPython] G4_URANIUM_OXIDE  # scripted group (container) (typed FeaturePython)
  Dunit = g/cm3
  Dvalue = 10.96
  Group = -> [U_element003,O_element100]
  conduct = 2
  density = 1
  expand = 3
  formula = G4_URANIUM_OXIDE
  name = G4_URANIUM_OXIDE
  specific = 4
FEATURE [App::DocumentObjectGroupPython] C_element119  label="C_element : 066"  # scripted group (container) (typed FeaturePython)
  n = 1
  ref = C_element
FEATURE [App::DocumentObjectGroupPython] H_element107  label="H_element : 057"  # scripted group (container) (typed FeaturePython)
  n = 4
  ref = H_element
FEATURE [App::DocumentObjectGroupPython] N_element046  label="N_element : 019"  # scripted group (container) (typed FeaturePython)
  n = 2
  ref = N_element
FEATURE [App::DocumentObjectGroupPython] O_element101  label="O_element : 055"  # scripted group (container) (typed FeaturePython)
  n = 1
  ref = O_element
FEATURE [App::DocumentObjectGroupPython] G4_UREA  # scripted group (container) (typed FeaturePython)
  Dunit = g/cm3
  Dvalue = 1.323
  Group = -> [C_element119,H_element107,N_element046,O_element101]
  conduct = 2
  density = 1
  expand = 3
  formula = G4_UREA
  name = G4_UREA
  specific = 4
FEATURE [App::DocumentObjectGroupPython] C_element120  label="C_element : 067"  # scripted group (container) (typed FeaturePython)
  n = 5
  ref = C_element
FEATURE [App::DocumentObjectGroupPython] H_element108  label="H_element : 058"  # scripted group (container) (typed FeaturePython)
  n = 11
  ref = H_element
FEATURE [App::DocumentObjectGroupPython] N_element047  label="N_element : 020"  # scripted group (container) (typed FeaturePython)
  n = 1
  ref = N_element
FEATURE [App::DocumentObjectGroupPython] O_element102  label="O_element : 056"  # scripted group (container) (typed FeaturePython)
  n = 2
  ref = O_element
FEATURE [App::DocumentObjectGroupPython] G4_VALINE  # scripted group (container) (typed FeaturePython)
  Dunit = g/cm3
  Dvalue = 1.23
  Group = -> [C_element120,H_element108,N_element047,O_element102]
  conduct = 2
  density = 1
  expand = 3
  formula = G4_VALINE
  name = G4_VALINE
  specific = 4
FEATURE [App::DocumentObjectGroupPython] H_element109  label="H_element : 0.009"  # scripted group (container) (typed FeaturePython)
  n = 0.009417
FEATURE [App::DocumentObjectGroupPython] C_element121  label="C_element : 0.281"  # scripted group (container) (typed FeaturePython)
  n = 0.280555
FEATURE [App::DocumentObjectGroupPython] F_element018  label="F_element : 0.710"  # scripted group (container) (typed FeaturePython)
  n = 0.710028
FEATURE [App::DocumentObjectGroupPython] G4_VITON  # scripted group (container) (typed FeaturePython)
  Dunit = g/cm3
  Dvalue = 1.8
  Group = -> [H_element109,C_element121,F_element018]
  conduct = 2
  density = 1
  expand = 3
  formula = G4_VITON
  name = G4_VITON
  specific = 4
FEATURE [App::DocumentObjectGroupPython] H_element110  label="H_element : 059"  # scripted group (container) (typed FeaturePython)
  n = 2
  ref = H_element
FEATURE [App::DocumentObjectGroupPython] O_element103  label="O_element : 057"  # scripted group (container) (typed FeaturePython)
  n = 1
  ref = O_element
FEATURE [App::DocumentObjectGroupPython] G4_WATER  # scripted group (container) (typed FeaturePython)
  Dunit = g/cm3
  Dvalue = 1
  Group = -> [H_element110,O_element103]
  conduct = 2
  density = 1
  expand = 3
  formula = G4_WATER
  name = G4_WATER
  specific = 4
FEATURE [App::DocumentObjectGroupPython] H_element111  label="H_element : 060"  # scripted group (container) (typed FeaturePython)
  n = 2
  ref = H_element
FEATURE [App::DocumentObjectGroupPython] O_element104  label="O_element : 058"  # scripted group (container) (typed FeaturePython)
  n = 1
  ref = O_element
FEATURE [App::DocumentObjectGroupPython] G4_WATER_VAPOR  # scripted group (container) (typed FeaturePython)
  Dunit = g/cm3
  Dvalue = 0.000756182
  Group = -> [H_element111,O_element104]
  conduct = 2
  density = 1
  expand = 3
  formula = G4_WATER_VAPOR
  name = G4_WATER_VAPOR
  specific = 4
FEATURE [App::DocumentObjectGroupPython] C_element122  label="C_element : 068"  # scripted group (container) (typed FeaturePython)
  n = 8
  ref = C_element
FEATURE [App::DocumentObjectGroupPython] H_element112  label="H_element : 061"  # scripted group (container) (typed FeaturePython)
  n = 10
  ref = H_element
FEATURE [App::DocumentObjectGroupPython] G4_XYLENE  # scripted group (container) (typed FeaturePython)
  Dunit = g/cm3
  Dvalue = 0.87
  Group = -> [C_element122,H_element112]
  conduct = 2
  density = 1
  expand = 3
  formula = G4_XYLENE
  name = G4_XYLENE
  specific = 4
FEATURE [App::DocumentObjectGroupPython] C_element123  label="C_element : 069"  # scripted group (container) (typed FeaturePython)
  n = 1
  ref = C_element
FEATURE [App::DocumentObjectGroupPython] G4_GRAPHITE  # scripted group (container) (typed FeaturePython)
  Dunit = g/cm3
  Dvalue = 2.21
  Group = -> [C_element123]
  conduct = 2
  density = 1
  expand = 3
  formula = G4_GRAPHITE
  name = G4_GRAPHITE
  specific = 4
FEATURE [App::DocumentObjectGroupPython] NIST  # scripted group (container) (typed FeaturePython)
  Group = -> [G4_A_150_TISSUE,G4_ACETONE,G4_ACETYLENE,G4_ADENINE,G4_ADIPOSE_TISSUE_ICRP,G4_AIR,G4_ALANINE,G4_ALUMINUM_OXIDE,G4_AMBER,G4_AMMONIA,G4_ANILINE,G4_ANTHRACENE,G4_B_100_BONE,G4_BAKELITE,G4_BARIUM_FLUORIDE,G4_BARIUM_SULFATE,G4_BENZENE,G4_BERYLLIUM_OXIDE,G4_BGO,G4_BLOOD_ICRP,G4_BONE_COMPACT_ICRU,G4_BONE_CORTICAL_ICRP,G4_BORON_CARBIDE,G4_BORON_OXIDE,G4_BRAIN_ICRP,G4_BUTANE,G4_N_BUTYL_ALCOHOL,G4_C_552,+152 more]
FEATURE [App::DocumentObjectGroupPython] H_element113  label="H_element : 062"  # scripted group (container) (typed FeaturePython)
  n = 1
  ref = H_element
FEATURE [App::DocumentObjectGroupPython] G4_H  # scripted group (container) (typed FeaturePython)
  Dunit = g/cm3
  Dvalue = 8.3748e-05
  Group = -> [H_element113]
  conduct = 2
  density = 1
  expand = 3
  formula = H
  name = G4_H
  specific = 4
FEATURE [App::DocumentObjectGroupPython] He_element001  label="He_element : 1"  # scripted group (container) (typed FeaturePython)
  n = 1
  ref = He_element
FEATURE [App::DocumentObjectGroupPython] G4_He  # scripted group (container) (typed FeaturePython)
  Dunit = g/cm3
  Dvalue = 0.000166322
  Group = -> [He_element001]
  conduct = 2
  density = 1
  expand = 3
  formula = He
  name = G4_He
  specific = 4
FEATURE [App::DocumentObjectGroupPython] Li_element008  label="Li_element : 008"  # scripted group (container) (typed FeaturePython)
  n = 1
  ref = Li_element
FEATURE [App::DocumentObjectGroupPython] G4_Li  # scripted group (container) (typed FeaturePython)
  Dunit = g/cm3
  Dvalue = 0.534
  Group = -> [Li_element008]
  conduct = 2
  density = 1
  expand = 3
  formula = Li
  name = G4_Li
  specific = 4
FEATURE [App::DocumentObjectGroupPython] Be_element002  label="Be_element : 002"  # scripted group (container) (typed FeaturePython)
  n = 1
  ref = Be_element
FEATURE [App::DocumentObjectGroupPython] G4_Be  # scripted group (container) (typed FeaturePython)
  Dunit = g/cm3
  Dvalue = 1.848
  Group = -> [Be_element002]
  conduct = 2
  density = 1
  expand = 3
  formula = Be
  name = G4_Be
  specific = 4
FEATURE [App::DocumentObjectGroupPython] B_element007  label="B_element : 007"  # scripted group (container) (typed FeaturePython)
  n = 1
  ref = B_element
FEATURE [App::DocumentObjectGroupPython] G4_B  # scripted group (container) (typed FeaturePython)
  Dunit = g/cm3
  Dvalue = 2.37
  Group = -> [B_element007]
  conduct = 2
  density = 1
  expand = 3
  formula = B
  name = G4_B
  specific = 4
FEATURE [App::DocumentObjectGroupPython] C_element124  label="C_element : 070"  # scripted group (container) (typed FeaturePython)
  n = 1
  ref = C_element
FEATURE [App::DocumentObjectGroupPython] G4_C  # scripted group (container) (typed FeaturePython)
  Dunit = g/cm3
  Dvalue = 2
  Group = -> [C_element124]
  conduct = 2
  density = 1
  expand = 3
  formula = C
  name = G4_C
  specific = 4
FEATURE [App::DocumentObjectGroupPython] N_element048  label="N_element : 021"  # scripted group (container) (typed FeaturePython)
  n = 1
  ref = N_element
FEATURE [App::DocumentObjectGroupPython] G4_N  # scripted group (container) (typed FeaturePython)
  Dunit = g/cm3
  Dvalue = 0.0011652
  Group = -> [N_element048]
  conduct = 2
  density = 1
  expand = 3
  formula = N
  name = G4_N
  specific = 4
FEATURE [App::DocumentObjectGroupPython] O_element105  label="O_element : 059"  # scripted group (container) (typed FeaturePython)
  n = 1
  ref = O_element
FEATURE [App::DocumentObjectGroupPython] G4_O  # scripted group (container) (typed FeaturePython)
  Dunit = g/cm3
  Dvalue = 0.00133151
  Group = -> [O_element105]
  conduct = 2
  density = 1
  expand = 3
  formula = O
  name = G4_O
  specific = 4
FEATURE [App::DocumentObjectGroupPython] F_element019  label="F_element : 008"  # scripted group (container) (typed FeaturePython)
  n = 1
  ref = F_element
FEATURE [App::DocumentObjectGroupPython] G4_F  # scripted group (container) (typed FeaturePython)
  Dunit = g/cm3
  Dvalue = 0.00158029
  Group = -> [F_element019]
  conduct = 2
  density = 1
  expand = 3
  formula = F
  name = G4_F
  specific = 4
FEATURE [App::DocumentObjectGroupPython] Ne_element001  label="Ne_element : 1"  # scripted group (container) (typed FeaturePython)
  n = 1
  ref = Ne_element
FEATURE [App::DocumentObjectGroupPython] G4_Ne  # scripted group (container) (typed FeaturePython)
  Dunit = g/cm3
  Dvalue = 0.000838505
  Group = -> [Ne_element001]
  conduct = 2
  density = 1
  expand = 3
  formula = Ne
  name = G4_Ne
  specific = 4
FEATURE [App::DocumentObjectGroupPython] Na_element020  label="Na_element : 005"  # scripted group (container) (typed FeaturePython)
  n = 1
  ref = Na_element
FEATURE [App::DocumentObjectGroupPython] G4_Na  # scripted group (container) (typed FeaturePython)
  Dunit = g/cm3
  Dvalue = 0.971
  Group = -> [Na_element020]
  conduct = 2
  density = 1
  expand = 3
  formula = Na
  name = G4_Na
  specific = 4
FEATURE [App::DocumentObjectGroupPython] Mg_element011  label="Mg_element : 005"  # scripted group (container) (typed FeaturePython)
  n = 1
  ref = Mg_element
FEATURE [App::DocumentObjectGroupPython] G4_Mg  # scripted group (container) (typed FeaturePython)
  Dunit = g/cm3
  Dvalue = 1.74
  Group = -> [Mg_element011]
  conduct = 2
  density = 1
  expand = 3
  formula = Mg
  name = G4_Mg
  specific = 4
FEATURE [App::DocumentObjectGroupPython] Al_element004  label="Al_element : 1"  # scripted group (container) (typed FeaturePython)
  n = 1
  ref = Al_element
FEATURE [App::DocumentObjectGroupPython] G4_Al  # scripted group (container) (typed FeaturePython)
  Dunit = g/cm3
  Dvalue = 2.699
  Group = -> [Al_element004]
  conduct = 2
  density = 1
  expand = 3
  formula = Al
  name = G4_Al
  specific = 4
FEATURE [App::DocumentObjectGroupPython] Si_element007  label="Si_element : 002"  # scripted group (container) (typed FeaturePython)
  n = 1
  ref = Si_element
FEATURE [App::DocumentObjectGroupPython] G4_Si  # scripted group (container) (typed FeaturePython)
  Dunit = g/cm3
  Dvalue = 2.33
  Group = -> [Si_element007]
  conduct = 2
  density = 1
  expand = 3
  formula = Si
  name = G4_Si
  specific = 4
FEATURE [App::DocumentObjectGroupPython] P_element013  label="P_element : 002"  # scripted group (container) (typed FeaturePython)
  n = 1
  ref = P_element
FEATURE [App::DocumentObjectGroupPython] G4_P  # scripted group (container) (typed FeaturePython)
  Dunit = g/cm3
  Dvalue = 2.2
  Group = -> [P_element013]
  conduct = 2
  density = 1
  expand = 3
  formula = P
  name = G4_P
  specific = 4
FEATURE [App::DocumentObjectGroupPython] S_element023  label="S_element : 007"  # scripted group (container) (typed FeaturePython)
  n = 1
  ref = S_element
FEATURE [App::DocumentObjectGroupPython] G4_S  # scripted group (container) (typed FeaturePython)
  Dunit = g/cm3
  Dvalue = 2
  Group = -> [S_element023]
  conduct = 2
  density = 1
  expand = 3
  formula = S
  name = G4_S
  specific = 4
FEATURE [App::DocumentObjectGroupPython] Cl_element029  label="Cl_element : 015"  # scripted group (container) (typed FeaturePython)
  n = 1
  ref = Cl_element
FEATURE [App::DocumentObjectGroupPython] G4_Cl  # scripted group (container) (typed FeaturePython)
  Dunit = g/cm3
  Dvalue = 0.00299473
  Group = -> [Cl_element029]
  conduct = 2
  density = 1
  expand = 3
  formula = Cl
  name = G4_Cl
  specific = 4
FEATURE [App::DocumentObjectGroupPython] Ar_element002  label="Ar_element : 1"  # scripted group (container) (typed FeaturePython)
  n = 1
  ref = Ar_element
FEATURE [App::DocumentObjectGroupPython] G4_Ar  # scripted group (container) (typed FeaturePython)
  Dunit = g/cm3
  Dvalue = 0.00166201
  Group = -> [Ar_element002]
  conduct = 2
  density = 1
  expand = 3
  formula = Ar
  name = G4_Ar
  specific = 4
FEATURE [App::DocumentObjectGroupPython] K_element013  label="K_element : 003"  # scripted group (container) (typed FeaturePython)
  n = 1
  ref = K_element
FEATURE [App::DocumentObjectGroupPython] G4_K  # scripted group (container) (typed FeaturePython)
  Dunit = g/cm3
  Dvalue = 0.862
  Group = -> [K_element013]
  conduct = 2
  density = 1
  expand = 3
  formula = K
  name = G4_K
  specific = 4
FEATURE [App::DocumentObjectGroupPython] Ca_element014  label="Ca_element : 007"  # scripted group (container) (typed FeaturePython)
  n = 1
  ref = Ca_element
FEATURE [App::DocumentObjectGroupPython] G4_Ca  # scripted group (container) (typed FeaturePython)
  Dunit = g/cm3
  Dvalue = 1.55
  Group = -> [Ca_element014]
  conduct = 2
  density = 1
  expand = 3
  formula = Ca
  name = G4_Ca
  specific = 4
FEATURE [App::DocumentObjectGroupPython] Sc_element001  label="Sc_element : 1"  # scripted group (container) (typed FeaturePython)
  n = 1
  ref = Sc_element
FEATURE [App::DocumentObjectGroupPython] G4_Sc  # scripted group (container) (typed FeaturePython)
  Dunit = g/cm3
  Dvalue = 2.989
  Group = -> [Sc_element001]
  conduct = 2
  density = 1
  expand = 3
  formula = Sc
  name = G4_Sc
  specific = 4
FEATURE [App::DocumentObjectGroupPython] Ti_element004  label="Ti_element : 002"  # scripted group (container) (typed FeaturePython)
  n = 1
  ref = Ti_element
FEATURE [App::DocumentObjectGroupPython] G4_Ti  # scripted group (container) (typed FeaturePython)
  Dunit = g/cm3
  Dvalue = 4.54
  Group = -> [Ti_element004]
  conduct = 2
  density = 1
  expand = 3
  formula = Ti
  name = G4_Ti
  specific = 4
FEATURE [App::DocumentObjectGroupPython] V_element001  label="V_element : 1"  # scripted group (container) (typed FeaturePython)
  n = 1
  ref = V_element
FEATURE [App::DocumentObjectGroupPython] G4_V  # scripted group (container) (typed FeaturePython)
  Dunit = g/cm3
  Dvalue = 6.11
  Group = -> [V_element001]
  conduct = 2
  density = 1
  expand = 3
  formula = V
  name = G4_V
  specific = 4
FEATURE [App::DocumentObjectGroupPython] Cr_element001  label="Cr_element : 1"  # scripted group (container) (typed FeaturePython)
  n = 1
  ref = Cr_element
FEATURE [App::DocumentObjectGroupPython] G4_Cr  # scripted group (container) (typed FeaturePython)
  Dunit = g/cm3
  Dvalue = 7.18
  Group = -> [Cr_element001]
  conduct = 2
  density = 1
  expand = 3
  formula = Cr
  name = G4_Cr
  specific = 4
FEATURE [App::DocumentObjectGroupPython] Mn_element001  label="Mn_element : 1"  # scripted group (container) (typed FeaturePython)
  n = 1
  ref = Mn_element
FEATURE [App::DocumentObjectGroupPython] G4_Mn  # scripted group (container) (typed FeaturePython)
  Dunit = g/cm3
  Dvalue = 7.44
  Group = -> [Mn_element001]
  conduct = 2
  density = 1
  expand = 3
  formula = Mn
  name = G4_Mn
  specific = 4
FEATURE [App::DocumentObjectGroupPython] Fe_element007  label="Fe_element : 004"  # scripted group (container) (typed FeaturePython)
  n = 1
  ref = Fe_element
FEATURE [App::DocumentObjectGroupPython] G4_Fe  # scripted group (container) (typed FeaturePython)
  Dunit = g/cm3
  Dvalue = 7.874
  Group = -> [Fe_element007]
  conduct = 2
  density = 1
  expand = 3
  formula = Fe
  name = G4_Fe
  specific = 4
FEATURE [App::DocumentObjectGroupPython] Co_element001  label="Co_element : 1"  # scripted group (container) (typed FeaturePython)
  n = 1
  ref = Co_element
FEATURE [App::DocumentObjectGroupPython] G4_Co  # scripted group (container) (typed FeaturePython)
  Dunit = g/cm3
  Dvalue = 8.9
  Group = -> [Co_element001]
  conduct = 2
  density = 1
  expand = 3
  formula = Co
  name = G4_Co
  specific = 4
FEATURE [App::DocumentObjectGroupPython] Ni_element001  label="Ni_element : 1"  # scripted group (container) (typed FeaturePython)
  n = 1
  ref = Ni_element
FEATURE [App::DocumentObjectGroupPython] G4_Ni  # scripted group (container) (typed FeaturePython)
  Dunit = g/cm3
  Dvalue = 8.902
  Group = -> [Ni_element001]
  conduct = 2
  density = 1
  expand = 3
  formula = Ni
  name = G4_Ni
  specific = 4
FEATURE [App::DocumentObjectGroupPython] Cu_element001  label="Cu_element : 1"  # scripted group (container) (typed FeaturePython)
  n = 1
  ref = Cu_element
FEATURE [App::DocumentObjectGroupPython] G4_Cu  # scripted group (container) (typed FeaturePython)
  Dunit = g/cm3
  Dvalue = 8.96
  Group = -> [Cu_element001]
  conduct = 2
  density = 1
  expand = 3
  formula = Cu
  name = G4_Cu
  specific = 4
FEATURE [App::DocumentObjectGroupPython] Zn_element001  label="Zn_element : 1"  # scripted group (container) (typed FeaturePython)
  n = 1
  ref = Zn_element
FEATURE [App::DocumentObjectGroupPython] G4_Zn  # scripted group (container) (typed FeaturePython)
  Dunit = g/cm3
  Dvalue = 7.133
  Group = -> [Zn_element001]
  conduct = 2
  density = 1
  expand = 3
  formula = Zn
  name = G4_Zn
  specific = 4
FEATURE [App::DocumentObjectGroupPython] Ga_element002  label="Ga_element : 002"  # scripted group (container) (typed FeaturePython)
  n = 1
  ref = Ga_element
FEATURE [App::DocumentObjectGroupPython] G4_Ga  # scripted group (container) (typed FeaturePython)
  Dunit = g/cm3
  Dvalue = 5.904
  Group = -> [Ga_element002]
  conduct = 2
  density = 1
  expand = 3
  formula = Ga
  name = G4_Ga
  specific = 4
FEATURE [App::DocumentObjectGroupPython] Ge_element002  label="Ge_element : 1"  # scripted group (container) (typed FeaturePython)
  n = 1
  ref = Ge_element
FEATURE [App::DocumentObjectGroupPython] G4_Ge  # scripted group (container) (typed FeaturePython)
  Dunit = g/cm3
  Dvalue = 5.323
  Group = -> [Ge_element002]
  conduct = 2
  density = 1
  expand = 3
  formula = Ge
  name = G4_Ge
  specific = 4
FEATURE [App::DocumentObjectGroupPython] As_element003  label="As_element : 002"  # scripted group (container) (typed FeaturePython)
  n = 1
  ref = As_element
FEATURE [App::DocumentObjectGroupPython] G4_As  # scripted group (container) (typed FeaturePython)
  Dunit = g/cm3
  Dvalue = 5.73
  Group = -> [As_element003]
  conduct = 2
  density = 1
  expand = 3
  formula = As
  name = G4_As
  specific = 4
FEATURE [App::DocumentObjectGroupPython] Se_element001  label="Se_element : 1"  # scripted group (container) (typed FeaturePython)
  n = 1
  ref = Se_element
FEATURE [App::DocumentObjectGroupPython] G4_Se  # scripted group (container) (typed FeaturePython)
  Dunit = g/cm3
  Dvalue = 4.5
  Group = -> [Se_element001]
  conduct = 2
  density = 1
  expand = 3
  formula = Se
  name = G4_Se
  specific = 4
FEATURE [App::DocumentObjectGroupPython] Br_element007  label="Br_element : 004"  # scripted group (container) (typed FeaturePython)
  n = 1
  ref = Br_element
FEATURE [App::DocumentObjectGroupPython] G4_Br  # scripted group (container) (typed FeaturePython)
  Dunit = g/cm3
  Dvalue = 0.0070721
  Group = -> [Br_element007]
  conduct = 2
  density = 1
  expand = 3
  formula = Br
  name = G4_Br
  specific = 4
FEATURE [App::DocumentObjectGroupPython] Kr_element001  label="Kr_element : 1"  # scripted group (container) (typed FeaturePython)
  n = 1
  ref = Kr_element
FEATURE [App::DocumentObjectGroupPython] G4_Kr  # scripted group (container) (typed FeaturePython)
  Dunit = g/cm3
  Dvalue = 0.00347832
  Group = -> [Kr_element001]
  conduct = 2
  density = 1
  expand = 3
  formula = Kr
  name = G4_Kr
  specific = 4
FEATURE [App::DocumentObjectGroupPython] Rb_element001  label="Rb_element : 1"  # scripted group (container) (typed FeaturePython)
  n = 1
  ref = Rb_element
FEATURE [App::DocumentObjectGroupPython] G4_Rb  # scripted group (container) (typed FeaturePython)
  Dunit = g/cm3
  Dvalue = 1.532
  Group = -> [Rb_element001]
  conduct = 2
  density = 1
  expand = 3
  formula = Rb
  name = G4_Rb
  specific = 4
FEATURE [App::DocumentObjectGroupPython] Sr_element001  label="Sr_element : 1"  # scripted group (container) (typed FeaturePython)
  n = 1
  ref = Sr_element
FEATURE [App::DocumentObjectGroupPython] G4_Sr  # scripted group (container) (typed FeaturePython)
  Dunit = g/cm3
  Dvalue = 2.54
  Group = -> [Sr_element001]
  conduct = 2
  density = 1
  expand = 3
  formula = Sr
  name = G4_Sr
  specific = 4
FEATURE [App::DocumentObjectGroupPython] Y_element001  label="Y_element : 1"  # scripted group (container) (typed FeaturePython)
  n = 1
  ref = Y_element
FEATURE [App::DocumentObjectGroupPython] G4_Y  # scripted group (container) (typed FeaturePython)
  Dunit = g/cm3
  Dvalue = 4.469
  Group = -> [Y_element001]
  conduct = 2
  density = 1
  expand = 3
  formula = Y
  name = G4_Y
  specific = 4
FEATURE [App::DocumentObjectGroupPython] Zr_element001  label="Zr_element : 1"  # scripted group (container) (typed FeaturePython)
  n = 1
  ref = Zr_element
FEATURE [App::DocumentObjectGroupPython] G4_Zr  # scripted group (container) (typed FeaturePython)
  Dunit = g/cm3
  Dvalue = 6.506
  Group = -> [Zr_element001]
  conduct = 2
  density = 1
  expand = 3
  formula = Zr
  name = G4_Zr
  specific = 4
FEATURE [App::DocumentObjectGroupPython] Nb_element001  label="Nb_element : 1"  # scripted group (container) (typed FeaturePython)
  n = 1
  ref = Nb_element
FEATURE [App::DocumentObjectGroupPython] G4_Nb  # scripted group (container) (typed FeaturePython)
  Dunit = g/cm3
  Dvalue = 8.57
  Group = -> [Nb_element001]
  conduct = 2
  density = 1
  expand = 3
  formula = Nb
  name = G4_Nb
  specific = 4
FEATURE [App::DocumentObjectGroupPython] Mo_element001  label="Mo_element : 1"  # scripted group (container) (typed FeaturePython)
  n = 1
  ref = Mo_element
FEATURE [App::DocumentObjectGroupPython] G4_Mo  # scripted group (container) (typed FeaturePython)
  Dunit = g/cm3
  Dvalue = 10.22
  Group = -> [Mo_element001]
  conduct = 2
  density = 1
  expand = 3
  formula = Mo
  name = G4_Mo
  specific = 4
FEATURE [App::DocumentObjectGroupPython] Tc_element001  label="Tc_element : 1"  # scripted group (container) (typed FeaturePython)
  n = 1
  ref = Tc_element
FEATURE [App::DocumentObjectGroupPython] G4_Tc  # scripted group (container) (typed FeaturePython)
  Dunit = g/cm3
  Dvalue = 11.5
  Group = -> [Tc_element001]
  conduct = 2
  density = 1
  expand = 3
  formula = Tc
  name = G4_Tc
  specific = 4
FEATURE [App::DocumentObjectGroupPython] Ru_element001  label="Ru_element : 1"  # scripted group (container) (typed FeaturePython)
  n = 1
  ref = Ru_element
FEATURE [App::DocumentObjectGroupPython] G4_Ru  # scripted group (container) (typed FeaturePython)
  Dunit = g/cm3
  Dvalue = 12.41
  Group = -> [Ru_element001]
  conduct = 2
  density = 1
  expand = 3
  formula = Ru
  name = G4_Ru
  specific = 4
FEATURE [App::DocumentObjectGroupPython] Rh_element001  label="Rh_element : 1"  # scripted group (container) (typed FeaturePython)
  n = 1
  ref = Rh_element
FEATURE [App::DocumentObjectGroupPython] G4_Rh  # scripted group (container) (typed FeaturePython)
  Dunit = g/cm3
  Dvalue = 12.41
  Group = -> [Rh_element001]
  conduct = 2
  density = 1
  expand = 3
  formula = Rh
  name = G4_Rh
  specific = 4
FEATURE [App::DocumentObjectGroupPython] Pd_element001  label="Pd_element : 1"  # scripted group (container) (typed FeaturePython)
  n = 1
  ref = Pd_element
FEATURE [App::DocumentObjectGroupPython] G4_Pd  # scripted group (container) (typed FeaturePython)
  Dunit = g/cm3
  Dvalue = 12.02
  Group = -> [Pd_element001]
  conduct = 2
  density = 1
  expand = 3
  formula = Pd
  name = G4_Pd
  specific = 4
FEATURE [App::DocumentObjectGroupPython] Ag_element006  label="Ag_element : 004"  # scripted group (container) (typed FeaturePython)
  n = 1
  ref = Ag_element
FEATURE [App::DocumentObjectGroupPython] G4_Ag  # scripted group (container) (typed FeaturePython)
  Dunit = g/cm3
  Dvalue = 10.5
  Group = -> [Ag_element006]
  conduct = 2
  density = 1
  expand = 3
  formula = Ag
  name = G4_Ag
  specific = 4
FEATURE [App::DocumentObjectGroupPython] Cd_element003  label="Cd_element : 003"  # scripted group (container) (typed FeaturePython)
  n = 1
  ref = Cd_element
FEATURE [App::DocumentObjectGroupPython] G4_Cd  # scripted group (container) (typed FeaturePython)
  Dunit = g/cm3
  Dvalue = 8.65
  Group = -> [Cd_element003]
  conduct = 2
  density = 1
  expand = 3
  formula = Cd
  name = G4_Cd
  specific = 4
FEATURE [App::DocumentObjectGroupPython] In_element001  label="In_element : 1"  # scripted group (container) (typed FeaturePython)
  n = 1
  ref = In_element
FEATURE [App::DocumentObjectGroupPython] G4_In  # scripted group (container) (typed FeaturePython)
  Dunit = g/cm3
  Dvalue = 7.31
  Group = -> [In_element001]
  conduct = 2
  density = 1
  expand = 3
  formula = In
  name = G4_In
  specific = 4
FEATURE [App::DocumentObjectGroupPython] Sn_element001  label="Sn_element : 1"  # scripted group (container) (typed FeaturePython)
  n = 1
  ref = Sn_element
FEATURE [App::DocumentObjectGroupPython] G4_Sn  # scripted group (container) (typed FeaturePython)
  Dunit = g/cm3
  Dvalue = 7.31
  Group = -> [Sn_element001]
  conduct = 2
  density = 1
  expand = 3
  formula = Sn
  name = G4_Sn
  specific = 4
FEATURE [App::DocumentObjectGroupPython] Sb_element001  label="Sb_element : 1"  # scripted group (container) (typed FeaturePython)
  n = 1
  ref = Sb_element
FEATURE [App::DocumentObjectGroupPython] G4_Sb  # scripted group (container) (typed FeaturePython)
  Dunit = g/cm3
  Dvalue = 6.691
  Group = -> [Sb_element001]
  conduct = 2
  density = 1
  expand = 3
  formula = Sb
  name = G4_Sb
  specific = 4
FEATURE [App::DocumentObjectGroupPython] Te_element002  label="Te_element : 002"  # scripted group (container) (typed FeaturePython)
  n = 1
  ref = Te_element
FEATURE [App::DocumentObjectGroupPython] G4_Te  # scripted group (container) (typed FeaturePython)
  Dunit = g/cm3
  Dvalue = 6.24
  Group = -> [Te_element002]
  conduct = 2
  density = 1
  expand = 3
  formula = Te
  name = G4_Te
  specific = 4
FEATURE [App::DocumentObjectGroupPython] I_element010  label="I_element : 006"  # scripted group (container) (typed FeaturePython)
  n = 1
  ref = I_element
FEATURE [App::DocumentObjectGroupPython] G4_I  # scripted group (container) (typed FeaturePython)
  Dunit = g/cm3
  Dvalue = 4.93
  Group = -> [I_element010]
  conduct = 2
  density = 1
  expand = 3
  formula = I
  name = G4_I
  specific = 4
FEATURE [App::DocumentObjectGroupPython] Xe_element001  label="Xe_element : 1"  # scripted group (container) (typed FeaturePython)
  n = 1
  ref = Xe_element
FEATURE [App::DocumentObjectGroupPython] G4_Xe  # scripted group (container) (typed FeaturePython)
  Dunit = g/cm3
  Dvalue = 0.00548536
  Group = -> [Xe_element001]
  conduct = 2
  density = 1
  expand = 3
  formula = Xe
  name = G4_Xe
  specific = 4
FEATURE [App::DocumentObjectGroupPython] Cs_element003  label="Cs_element : 003"  # scripted group (container) (typed FeaturePython)
  n = 1
  ref = Cs_element
FEATURE [App::DocumentObjectGroupPython] G4_Cs  # scripted group (container) (typed FeaturePython)
  Dunit = g/cm3
  Dvalue = 1.873
  Group = -> [Cs_element003]
  conduct = 2
  density = 1
  expand = 3
  formula = Cs
  name = G4_Cs
  specific = 4
FEATURE [App::DocumentObjectGroupPython] Ba_element003  label="Ba_element : 003"  # scripted group (container) (typed FeaturePython)
  n = 1
  ref = Ba_element
FEATURE [App::DocumentObjectGroupPython] G4_Ba  # scripted group (container) (typed FeaturePython)
  Dunit = g/cm3
  Dvalue = 3.5
  Group = -> [Ba_element003]
  conduct = 2
  density = 1
  expand = 3
  formula = Ba
  name = G4_Ba
  specific = 4
FEATURE [App::DocumentObjectGroupPython] La_element003  label="La_element : 003"  # scripted group (container) (typed FeaturePython)
  n = 1
  ref = La_element
FEATURE [App::DocumentObjectGroupPython] G4_La  # scripted group (container) (typed FeaturePython)
  Dunit = g/cm3
  Dvalue = 6.154
  Group = -> [La_element003]
  conduct = 2
  density = 1
  expand = 3
  formula = La
  name = G4_La
  specific = 4
FEATURE [App::DocumentObjectGroupPython] Ce_element002  label="Ce_element : 1"  # scripted group (container) (typed FeaturePython)
  n = 1
  ref = Ce_element
FEATURE [App::DocumentObjectGroupPython] G4_Ce  # scripted group (container) (typed FeaturePython)
  Dunit = g/cm3
  Dvalue = 6.657
  Group = -> [Ce_element002]
  conduct = 2
  density = 1
  expand = 3
  formula = Ce
  name = G4_Ce
  specific = 4
FEATURE [App::DocumentObjectGroupPython] Pr_element001  label="Pr_element : 1"  # scripted group (container) (typed FeaturePython)
  n = 1
  ref = Pr_element
FEATURE [App::DocumentObjectGroupPython] G4_Pr  # scripted group (container) (typed FeaturePython)
  Dunit = g/cm3
  Dvalue = 6.71
  Group = -> [Pr_element001]
  conduct = 2
  density = 1
  expand = 3
  formula = Pr
  name = G4_Pr
  specific = 4
FEATURE [App::DocumentObjectGroupPython] Nd_element001  label="Nd_element : 1"  # scripted group (container) (typed FeaturePython)
  n = 1
  ref = Nd_element
FEATURE [App::DocumentObjectGroupPython] G4_Nd  # scripted group (container) (typed FeaturePython)
  Dunit = g/cm3
  Dvalue = 6.9
  Group = -> [Nd_element001]
  conduct = 2
  density = 1
  expand = 3
  formula = Nd
  name = G4_Nd
  specific = 4
FEATURE [App::DocumentObjectGroupPython] Pm_element001  label="Pm_element : 1"  # scripted group (container) (typed FeaturePython)
  n = 1
  ref = Pm_element
FEATURE [App::DocumentObjectGroupPython] G4_Pm  # scripted group (container) (typed FeaturePython)
  Dunit = g/cm3
  Dvalue = 7.22
  Group = -> [Pm_element001]
  conduct = 2
  density = 1
  expand = 3
  formula = Pm
  name = G4_Pm
  specific = 4
FEATURE [App::DocumentObjectGroupPython] Sm_element001  label="Sm_element : 1"  # scripted group (container) (typed FeaturePython)
  n = 1
  ref = Sm_element
FEATURE [App::DocumentObjectGroupPython] G4_Sm  # scripted group (container) (typed FeaturePython)
  Dunit = g/cm3
  Dvalue = 7.46
  Group = -> [Sm_element001]
  conduct = 2
  density = 1
  expand = 3
  formula = Sm
  name = G4_Sm
  specific = 4
FEATURE [App::DocumentObjectGroupPython] Eu_element001  label="Eu_element : 1"  # scripted group (container) (typed FeaturePython)
  n = 1
  ref = Eu_element
FEATURE [App::DocumentObjectGroupPython] G4_Eu  # scripted group (container) (typed FeaturePython)
  Dunit = g/cm3
  Dvalue = 5.243
  Group = -> [Eu_element001]
  conduct = 2
  density = 1
  expand = 3
  formula = Eu
  name = G4_Eu
  specific = 4
FEATURE [App::DocumentObjectGroupPython] Gd_element002  label="Gd_element : 1"  # scripted group (container) (typed FeaturePython)
  n = 1
  ref = Gd_element
FEATURE [App::DocumentObjectGroupPython] G4_Gd  # scripted group (container) (typed FeaturePython)
  Dunit = g/cm3
  Dvalue = 7.9004
  Group = -> [Gd_element002]
  conduct = 2
  density = 1
  expand = 3
  formula = Gd
  name = G4_Gd
  specific = 4
FEATURE [App::DocumentObjectGroupPython] Tb_element001  label="Tb_element : 1"  # scripted group (container) (typed FeaturePython)
  n = 1
  ref = Tb_element
FEATURE [App::DocumentObjectGroupPython] G4_Tb  # scripted group (container) (typed FeaturePython)
  Dunit = g/cm3
  Dvalue = 8.229
  Group = -> [Tb_element001]
  conduct = 2
  density = 1
  expand = 3
  formula = Tb
  name = G4_Tb
  specific = 4
FEATURE [App::DocumentObjectGroupPython] Dy_element001  label="Dy_element : 1"  # scripted group (container) (typed FeaturePython)
  n = 1
  ref = Dy_element
FEATURE [App::DocumentObjectGroupPython] G4_Dy  # scripted group (container) (typed FeaturePython)
  Dunit = g/cm3
  Dvalue = 8.55
  Group = -> [Dy_element001]
  conduct = 2
  density = 1
  expand = 3
  formula = Dy
  name = G4_Dy
  specific = 4
FEATURE [App::DocumentObjectGroupPython] Ho_element001  label="Ho_element : 1"  # scripted group (container) (typed FeaturePython)
  n = 1
  ref = Ho_element
FEATURE [App::DocumentObjectGroupPython] G4_Ho  # scripted group (container) (typed FeaturePython)
  Dunit = g/cm3
  Dvalue = 8.795
  Group = -> [Ho_element001]
  conduct = 2
  density = 1
  expand = 3
  formula = Ho
  name = G4_Ho
  specific = 4
FEATURE [App::DocumentObjectGroupPython] Er_element001  label="Er_element : 1"  # scripted group (container) (typed FeaturePython)
  n = 1
  ref = Er_element
FEATURE [App::DocumentObjectGroupPython] G4_Er  # scripted group (container) (typed FeaturePython)
  Dunit = g/cm3
  Dvalue = 9.066
  Group = -> [Er_element001]
  conduct = 2
  density = 1
  expand = 3
  formula = Er
  name = G4_Er
  specific = 4
FEATURE [App::DocumentObjectGroupPython] Tm_element001  label="Tm_element : 1"  # scripted group (container) (typed FeaturePython)
  n = 1
  ref = Tm_element
FEATURE [App::DocumentObjectGroupPython] G4_Tm  # scripted group (container) (typed FeaturePython)
  Dunit = g/cm3
  Dvalue = 9.321
  Group = -> [Tm_element001]
  conduct = 2
  density = 1
  expand = 3
  formula = Tm
  name = G4_Tm
  specific = 4
FEATURE [App::DocumentObjectGroupPython] Yb_element001  label="Yb_element : 1"  # scripted group (container) (typed FeaturePython)
  n = 1
  ref = Yb_element
FEATURE [App::DocumentObjectGroupPython] G4_Yb  # scripted group (container) (typed FeaturePython)
  Dunit = g/cm3
  Dvalue = 6.73
  Group = -> [Yb_element001]
  conduct = 2
  density = 1
  expand = 3
  formula = Yb
  name = G4_Yb
  specific = 4
FEATURE [App::DocumentObjectGroupPython] Lu_element001  label="Lu_element : 1"  # scripted group (container) (typed FeaturePython)
  n = 1
  ref = Lu_element
FEATURE [App::DocumentObjectGroupPython] G4_Lu  # scripted group (container) (typed FeaturePython)
  Dunit = g/cm3
  Dvalue = 9.84
  Group = -> [Lu_element001]
  conduct = 2
  density = 1
  expand = 3
  formula = Lu
  name = G4_Lu
  specific = 4
FEATURE [App::DocumentObjectGroupPython] Hf_element001  label="Hf_element : 1"  # scripted group (container) (typed FeaturePython)
  n = 1
  ref = Hf_element
FEATURE [App::DocumentObjectGroupPython] G4_Hf  # scripted group (container) (typed FeaturePython)
  Dunit = g/cm3
  Dvalue = 13.31
  Group = -> [Hf_element001]
  conduct = 2
  density = 1
  expand = 3
  formula = Hf
  name = G4_Hf
  specific = 4
FEATURE [App::DocumentObjectGroupPython] Ta_element001  label="Ta_element : 1"  # scripted group (container) (typed FeaturePython)
  n = 1
  ref = Ta_element
FEATURE [App::DocumentObjectGroupPython] G4_Ta  # scripted group (container) (typed FeaturePython)
  Dunit = g/cm3
  Dvalue = 16.654
  Group = -> [Ta_element001]
  conduct = 2
  density = 1
  expand = 3
  formula = Ta
  name = G4_Ta
  specific = 4
FEATURE [App::DocumentObjectGroupPython] W_element004  label="W_element : 004"  # scripted group (container) (typed FeaturePython)
  n = 1
  ref = W_element
FEATURE [App::DocumentObjectGroupPython] G4_W  # scripted group (container) (typed FeaturePython)
  Dunit = g/cm3
  Dvalue = 19.3
  Group = -> [W_element004]
  conduct = 2
  density = 1
  expand = 3
  formula = W
  name = G4_W
  specific = 4
FEATURE [App::DocumentObjectGroupPython] Re_element001  label="Re_element : 1"  # scripted group (container) (typed FeaturePython)
  n = 1
  ref = Re_element
FEATURE [App::DocumentObjectGroupPython] G4_Re  # scripted group (container) (typed FeaturePython)
  Dunit = g/cm3
  Dvalue = 21.02
  Group = -> [Re_element001]
  conduct = 2
  density = 1
  expand = 3
  formula = Re
  name = G4_Re
  specific = 4
FEATURE [App::DocumentObjectGroupPython] Os_element001  label="Os_element : 1"  # scripted group (container) (typed FeaturePython)
  n = 1
  ref = Os_element
FEATURE [App::DocumentObjectGroupPython] G4_Os  # scripted group (container) (typed FeaturePython)
  Dunit = g/cm3
  Dvalue = 22.57
  Group = -> [Os_element001]
  conduct = 2
  density = 1
  expand = 3
  formula = Os
  name = G4_Os
  specific = 4
FEATURE [App::DocumentObjectGroupPython] Ir_element001  label="Ir_element : 1"  # scripted group (container) (typed FeaturePython)
  n = 1
  ref = Ir_element
FEATURE [App::DocumentObjectGroupPython] G4_Ir  # scripted group (container) (typed FeaturePython)
  Dunit = g/cm3
  Dvalue = 22.42
  Group = -> [Ir_element001]
  conduct = 2
  density = 1
  expand = 3
  formula = Ir
  name = G4_Ir
  specific = 4
FEATURE [App::DocumentObjectGroupPython] Pt_element001  label="Pt_element : 1"  # scripted group (container) (typed FeaturePython)
  n = 1
  ref = Pt_element
FEATURE [App::DocumentObjectGroupPython] G4_Pt  # scripted group (container) (typed FeaturePython)
  Dunit = g/cm3
  Dvalue = 21.45
  Group = -> [Pt_element001]
  conduct = 2
  density = 1
  expand = 3
  formula = Pt
  name = G4_Pt
  specific = 4
FEATURE [App::DocumentObjectGroupPython] Au_element001  label="Au_element : 1"  # scripted group (container) (typed FeaturePython)
  n = 1
  ref = Au_element
FEATURE [App::DocumentObjectGroupPython] G4_Au  # scripted group (container) (typed FeaturePython)
  Dunit = g/cm3
  Dvalue = 19.32
  Group = -> [Au_element001]
  conduct = 2
  density = 1
  expand = 3
  formula = Au
  name = G4_Au
  specific = 4
FEATURE [App::DocumentObjectGroupPython] Hg_element002  label="Hg_element : 002"  # scripted group (container) (typed FeaturePython)
  n = 1
  ref = Hg_element
FEATURE [App::DocumentObjectGroupPython] G4_Hg  # scripted group (container) (typed FeaturePython)
  Dunit = g/cm3
  Dvalue = 13.546
  Group = -> [Hg_element002]
  conduct = 2
  density = 1
  expand = 3
  formula = Hg
  name = G4_Hg
  specific = 4
FEATURE [App::DocumentObjectGroupPython] Tl_element002  label="Tl_element : 002"  # scripted group (container) (typed FeaturePython)
  n = 1
  ref = Tl_element
FEATURE [App::DocumentObjectGroupPython] G4_Tl  # scripted group (container) (typed FeaturePython)
  Dunit = g/cm3
  Dvalue = 11.72
  Group = -> [Tl_element002]
  conduct = 2
  density = 1
  expand = 3
  formula = Tl
  name = G4_Tl
  specific = 4
FEATURE [App::DocumentObjectGroupPython] Pb_element003  label="Pb_element : 1"  # scripted group (container) (typed FeaturePython)
  n = 1
  ref = Pb_element
FEATURE [App::DocumentObjectGroupPython] G4_Pb  # scripted group (container) (typed FeaturePython)
  Dunit = g/cm3
  Dvalue = 11.35
  Group = -> [Pb_element003]
  conduct = 2
  density = 1
  expand = 3
  formula = Pb
  name = G4_Pb
  specific = 4
FEATURE [App::DocumentObjectGroupPython] Bi_element002  label="Bi_element : 1"  # scripted group (container) (typed FeaturePython)
  n = 1
  ref = Bi_element
FEATURE [App::DocumentObjectGroupPython] G4_Bi  # scripted group (container) (typed FeaturePython)
  Dunit = g/cm3
  Dvalue = 9.747
  Group = -> [Bi_element002]
  conduct = 2
  density = 1
  expand = 3
  formula = Bi
  name = G4_Bi
  specific = 4
FEATURE [App::DocumentObjectGroupPython] Po_element001  label="Po_element : 1"  # scripted group (container) (typed FeaturePython)
  n = 1
  ref = Po_element
FEATURE [App::DocumentObjectGroupPython] G4_Po  # scripted group (container) (typed FeaturePython)
  Dunit = g/cm3
  Dvalue = 9.32
  Group = -> [Po_element001]
  conduct = 2
  density = 1
  expand = 3
  formula = Po
  name = G4_Po
  specific = 4
FEATURE [App::DocumentObjectGroupPython] At_element001  label="At_element : 1"  # scripted group (container) (typed FeaturePython)
  n = 1
  ref = At_element
FEATURE [App::DocumentObjectGroupPython] G4_At  # scripted group (container) (typed FeaturePython)
  Dunit = g/cm3
  Dvalue = 9.32
  Group = -> [At_element001]
  conduct = 2
  density = 1
  expand = 3
  formula = At
  name = G4_At
  specific = 4
FEATURE [App::DocumentObjectGroupPython] Rn_element001  label="Rn_element : 1"  # scripted group (container) (typed FeaturePython)
  n = 1
  ref = Rn_element
FEATURE [App::DocumentObjectGroupPython] G4_Rn  # scripted group (container) (typed FeaturePython)
  Dunit = g/cm3
  Dvalue = 0.00900662
  Group = -> [Rn_element001]
  conduct = 2
  density = 1
  expand = 3
  formula = Rn
  name = G4_Rn
  specific = 4
FEATURE [App::DocumentObjectGroupPython] Fr_element001  label="Fr_element : 1"  # scripted group (container) (typed FeaturePython)
  n = 1
  ref = Fr_element
FEATURE [App::DocumentObjectGroupPython] G4_Fr  # scripted group (container) (typed FeaturePython)
  Dunit = g/cm3
  Dvalue = 1
  Group = -> [Fr_element001]
  conduct = 2
  density = 1
  expand = 3
  formula = Fr
  name = G4_Fr
  specific = 4
FEATURE [App::DocumentObjectGroupPython] Ra_element001  label="Ra_element : 1"  # scripted group (container) (typed FeaturePython)
  n = 1
  ref = Ra_element
FEATURE [App::DocumentObjectGroupPython] G4_Ra  # scripted group (container) (typed FeaturePython)
  Dunit = g/cm3
  Dvalue = 5
  Group = -> [Ra_element001]
  conduct = 2
  density = 1
  expand = 3
  formula = Ra
  name = G4_Ra
  specific = 4
FEATURE [App::DocumentObjectGroupPython] Ac_element001  label="Ac_element : 1"  # scripted group (container) (typed FeaturePython)
  n = 1
  ref = Ac_element
FEATURE [App::DocumentObjectGroupPython] G4_Ac  # scripted group (container) (typed FeaturePython)
  Dunit = g/cm3
  Dvalue = 10.07
  Group = -> [Ac_element001]
  conduct = 2
  density = 1
  expand = 3
  formula = Ac
  name = G4_Ac
  specific = 4
FEATURE [App::DocumentObjectGroupPython] Th_element001  label="Th_element : 1"  # scripted group (container) (typed FeaturePython)
  n = 1
  ref = Th_element
FEATURE [App::DocumentObjectGroupPython] G4_Th  # scripted group (container) (typed FeaturePython)
  Dunit = g/cm3
  Dvalue = 11.72
  Group = -> [Th_element001]
  conduct = 2
  density = 1
  expand = 3
  formula = Th
  name = G4_Th
  specific = 4
FEATURE [App::DocumentObjectGroupPython] Pa_element001  label="Pa_element : 1"  # scripted group (container) (typed FeaturePython)
  n = 1
  ref = Pa_element
FEATURE [App::DocumentObjectGroupPython] G4_Pa  # scripted group (container) (typed FeaturePython)
  Dunit = g/cm3
  Dvalue = 15.37
  Group = -> [Pa_element001]
  conduct = 2
  density = 1
  expand = 3
  formula = Pa
  name = G4_Pa
  specific = 4
FEATURE [App::DocumentObjectGroupPython] U_element004  label="U_element : 004"  # scripted group (container) (typed FeaturePython)
  n = 1
  ref = U_element
FEATURE [App::DocumentObjectGroupPython] G4_U  # scripted group (container) (typed FeaturePython)
  Dunit = g/cm3
  Dvalue = 18.95
  Group = -> [U_element004]
  conduct = 2
  density = 1
  expand = 3
  formula = U
  name = G4_U
  specific = 4
FEATURE [App::DocumentObjectGroupPython] Np_element001  label="Np_element : 1"  # scripted group (container) (typed FeaturePython)
  n = 1
  ref = Np_element
FEATURE [App::DocumentObjectGroupPython] G4_Np  # scripted group (container) (typed FeaturePython)
  Dunit = g/cm3
  Dvalue = 20.25
  Group = -> [Np_element001]
  conduct = 2
  density = 1
  expand = 3
  formula = Np
  name = G4_Np
  specific = 4
FEATURE [App::DocumentObjectGroupPython] Pu_element002  label="Pu_element : 002"  # scripted group (container) (typed FeaturePython)
  n = 1
  ref = Pu_element
FEATURE [App::DocumentObjectGroupPython] G4_Pu  # scripted group (container) (typed FeaturePython)
  Dunit = g/cm3
  Dvalue = 19.84
  Group = -> [Pu_element002]
  conduct = 2
  density = 1
  expand = 3
  formula = Pu
  name = G4_Pu
  specific = 4
FEATURE [App::DocumentObjectGroupPython] Am_element001  label="Am_element : 1"  # scripted group (container) (typed FeaturePython)
  n = 1
  ref = Am_element
FEATURE [App::DocumentObjectGroupPython] G4_Am  # scripted group (container) (typed FeaturePython)
  Dunit = g/cm3
  Dvalue = 13.67
  Group = -> [Am_element001]
  conduct = 2
  density = 1
  expand = 3
  formula = Am
  name = G4_Am
  specific = 4
FEATURE [App::DocumentObjectGroupPython] Cm_element001  label="Cm_element : 1"  # scripted group (container) (typed FeaturePython)
  n = 1
  ref = Cm_element
FEATURE [App::DocumentObjectGroupPython] G4_Cm  # scripted group (container) (typed FeaturePython)
  Dunit = g/cm3
  Dvalue = 13.51
  Group = -> [Cm_element001]
  conduct = 2
  density = 1
  expand = 3
  formula = Cm
  name = G4_Cm
  specific = 4
FEATURE [App::DocumentObjectGroupPython] Bk_element001  label="Bk_element : 1"  # scripted group (container) (typed FeaturePython)
  n = 1
  ref = Bk_element
FEATURE [App::DocumentObjectGroupPython] G4_Bk  # scripted group (container) (typed FeaturePython)
  Dunit = g/cm3
  Dvalue = 14
  Group = -> [Bk_element001]
  conduct = 2
  density = 1
  expand = 3
  formula = Bk
  name = G4_Bk
  specific = 4
FEATURE [App::DocumentObjectGroupPython] Cf_element001  label="Cf_element : 1"  # scripted group (container) (typed FeaturePython)
  n = 1
  ref = Cf_element
FEATURE [App::DocumentObjectGroupPython] G4_Cf  # scripted group (container) (typed FeaturePython)
  Dunit = g/cm3
  Dvalue = 10
  Group = -> [Cf_element001]
  conduct = 2
  density = 1
  expand = 3
  formula = Cf
  name = G4_Cf
  specific = 4
FEATURE [App::DocumentObjectGroupPython] Element  # scripted group (container) (typed FeaturePython)
  Group = -> [G4_H,G4_He,G4_Li,G4_Be,G4_B,G4_C,G4_N,G4_O,G4_F,G4_Ne,G4_Na,G4_Mg,G4_Al,G4_Si,G4_P,G4_S,G4_Cl,G4_Ar,G4_K,G4_Ca,G4_Sc,G4_Ti,G4_V,G4_Cr,G4_Mn,G4_Fe,G4_Co,G4_Ni,G4_Cu,G4_Zn,G4_Ga,G4_Ge,G4_As,G4_Se,G4_Br,G4_Kr,G4_Rb,G4_Sr,G4_Y,G4_Zr,G4_Nb,G4_Mo,G4_Tc,G4_Ru,G4_Rh,G4_Pd,G4_Ag,G4_Cd,G4_In,G4_Sn,G4_Sb,G4_Te,G4_I,G4_Xe,G4_Cs,G4_Ba,G4_La,G4_Ce,G4_Pr,G4_Nd,G4_Pm,G4_Sm,G4_Eu,G4_Gd,G4_Tb,G4_Dy,G4_Ho,G4_Er,+30 more]
FEATURE [App::DocumentObjectGroupPython] H_element114  label="H_element : 063"  # scripted group (container) (typed FeaturePython)
  n = 2
  ref = H_element
FEATURE [App::DocumentObjectGroupPython] G4_lH2  # scripted group (container) (typed FeaturePython)
  Dunit = g/cm3
  Dvalue = 0.0708
  Group = -> [H_element114]
  conduct = 2
  density = 1
  expand = 3
  formula = G4_lH2
  name = G4_lH2
  specific = 4
FEATURE [App::DocumentObjectGroupPython] N_element049  label="N_element : 022"  # scripted group (container) (typed FeaturePython)
  n = 2
  ref = N_element
FEATURE [App::DocumentObjectGroupPython] G4_lN2  # scripted group (container) (typed FeaturePython)
  Dunit = g/cm3
  Dvalue = 0.807
  Group = -> [N_element049]
  conduct = 2
  density = 1
  expand = 3
  formula = G4_lN2
  name = G4_lN2
  specific = 4
FEATURE [App::DocumentObjectGroupPython] O_element106  label="O_element : 060"  # scripted group (container) (typed FeaturePython)
  n = 2
  ref = O_element
FEATURE [App::DocumentObjectGroupPython] G4_lO2  # scripted group (container) (typed FeaturePython)
  Dunit = g/cm3
  Dvalue = 1.141
  Group = -> [O_element106]
  conduct = 2
  density = 1
  expand = 3
  formula = G4_lO2
  name = G4_lO2
  specific = 4
FEATURE [App::DocumentObjectGroupPython] Ar  label="Ar : 1"  # scripted group (container) (typed FeaturePython)
  n = 1
  ref = Ar
FEATURE [App::DocumentObjectGroupPython] G4_lAr  # scripted group (container) (typed FeaturePython)
  Dunit = g/cm3
  Dvalue = 1.396
  Group = -> [Ar]
  conduct = 2
  density = 1
  expand = 3
  formula = G4_lAr
  name = G4_lAr
  specific = 4
FEATURE [App::DocumentObjectGroupPython] Br  label="Br : 1"  # scripted group (container) (typed FeaturePython)
  n = 1
  ref = Br
FEATURE [App::DocumentObjectGroupPython] G4_lBr  # scripted group (container) (typed FeaturePython)
  Dunit = g/cm3
  Dvalue = 3.1028
  Group = -> [Br]
  conduct = 2
  density = 1
  expand = 3
  formula = G4_lBr
  name = G4_lBr
  specific = 4
FEATURE [App::DocumentObjectGroupPython] Kr  label="Kr : 1"  # scripted group (container) (typed FeaturePython)
  n = 1
  ref = Kr
FEATURE [App::DocumentObjectGroupPython] G4_lKr  # scripted group (container) (typed FeaturePython)
  Dunit = g/cm3
  Dvalue = 2.418
  Group = -> [Kr]
  conduct = 2
  density = 1
  expand = 3
  formula = G4_lKr
  name = G4_lKr
  specific = 4
FEATURE [App::DocumentObjectGroupPython] Xe  label="Xe : 1"  # scripted group (container) (typed FeaturePython)
  n = 1
  ref = Xe
FEATURE [App::DocumentObjectGroupPython] G4_lXe  # scripted group (container) (typed FeaturePython)
  Dunit = g/cm3
  Dvalue = 2.953
  Group = -> [Xe]
  conduct = 2
  density = 1
  expand = 3
  formula = G4_lXe
  name = G4_lXe
  specific = 4
FEATURE [App::DocumentObjectGroupPython] O_element107  label="O_element : 061"  # scripted group (container) (typed FeaturePython)
  n = 4
  ref = O_element
FEATURE [App::DocumentObjectGroupPython] Pb_element004  label="Pb_element : 002"  # scripted group (container) (typed FeaturePython)
  n = 1
  ref = Pb_element
FEATURE [App::DocumentObjectGroupPython] W_element005  label="W_element : 005"  # scripted group (container) (typed FeaturePython)
  n = 1
  ref = W_element
FEATURE [App::DocumentObjectGroupPython] G4_PbWO4  # scripted group (container) (typed FeaturePython)
  Dunit = g/cm3
  Dvalue = 8.28
  Group = -> [O_element107,Pb_element004,W_element005]
  conduct = 2
  density = 1
  expand = 3
  formula = G4_PbWO4
  name = G4_PbWO4
  specific = 4
FEATURE [App::DocumentObjectGroupPython] alactic  label="alactic : 1"  # scripted group (container) (typed FeaturePython)
  n = 1
  ref = alactic
FEATURE [App::DocumentObjectGroupPython] G4_Galactic  # scripted group (container) (typed FeaturePython)
  Dunit = g/cm3
  Dvalue = 0
  Group = -> [alactic]
  conduct = 2
  density = 1
  expand = 3
  formula = G4_Galactic
  name = G4_Galactic
  specific = 4
FEATURE [App::DocumentObjectGroupPython] RAPHITE_POROUS  label="RAPHITE_POROUS : 1"  # scripted group (container) (typed FeaturePython)
  n = 1
  ref = RAPHITE_POROUS
FEATURE [App::DocumentObjectGroupPython] G4_GRAPHITE_POROUS  # scripted group (container) (typed FeaturePython)
  Dunit = g/cm3
  Dvalue = 1.7
  Group = -> [RAPHITE_POROUS]
  conduct = 2
  density = 1
  expand = 3
  formula = G4_GRAPHITE_POROUS
  name = G4_GRAPHITE_POROUS
  specific = 4
FEATURE [App::DocumentObjectGroupPython] H_element115  label="H_element : 0.150"  # scripted group (container) (typed FeaturePython)
  n = 0.080538
FEATURE [App::DocumentObjectGroupPython] C_element125  label="C_element : 0.600"  # scripted group (container) (typed FeaturePython)
  n = 0.599848
FEATURE [App::DocumentObjectGroupPython] O_element108  label="O_element : 0.320"  # scripted group (container) (typed FeaturePython)
  n = 0.319614
FEATURE [App::DocumentObjectGroupPython] G4_LUCITE  # scripted group (container) (typed FeaturePython)
  Dunit = g/cm3
  Dvalue = 1.19
  Group = -> [H_element115,C_element125,O_element108]
  conduct = 2
  density = 1
  expand = 3
  formula = G4_LUCITE
  name = G4_LUCITE
  specific = 4
FEATURE [App::DocumentObjectGroupPython] Cu_element002  label="Cu_element : 62"  # scripted group (container) (typed FeaturePython)
  n = 62
  ref = Cu_element
FEATURE [App::DocumentObjectGroupPython] Zn_element002  label="Zn_element : 35"  # scripted group (container) (typed FeaturePython)
  n = 35
  ref = Zn_element
FEATURE [App::DocumentObjectGroupPython] Pb_element005  label="Pb_element : 3"  # scripted group (container) (typed FeaturePython)
  n = 3
  ref = Pb_element
FEATURE [App::DocumentObjectGroupPython] G4_BRASS  # scripted group (container) (typed FeaturePython)
  Dunit = g/cm3
  Dvalue = 8.52
  Group = -> [Cu_element002,Zn_element002,Pb_element005]
  conduct = 2
  density = 1
  expand = 3
  formula = G4_BRASS
  name = G4_BRASS
  specific = 4
FEATURE [App::DocumentObjectGroupPython] Cu_element003  label="Cu_element : 89"  # scripted group (container) (typed FeaturePython)
  n = 89
  ref = Cu_element
FEATURE [App::DocumentObjectGroupPython] Zn_element003  label="Zn_element : 9"  # scripted group (container) (typed FeaturePython)
  n = 9
  ref = Zn_element
FEATURE [App::DocumentObjectGroupPython] Pb_element006  label="Pb_element : 2"  # scripted group (container) (typed FeaturePython)
  n = 2
  ref = Pb_element
FEATURE [App::DocumentObjectGroupPython] G4_BRONZE  # scripted group (container) (typed FeaturePython)
  Dunit = g/cm3
  Dvalue = 8.82
  Group = -> [Cu_element003,Zn_element003,Pb_element006]
  conduct = 2
  density = 1
  expand = 3
  formula = G4_BRONZE
  name = G4_BRONZE
  specific = 4
FEATURE [App::DocumentObjectGroupPython] Fe_element008  label="Fe_element : 74"  # scripted group (container) (typed FeaturePython)
  n = 74
  ref = Fe_element
FEATURE [App::DocumentObjectGroupPython] Cr_element002  label="Cr_element : 18"  # scripted group (container) (typed FeaturePython)
  n = 18
  ref = Cr_element
FEATURE [App::DocumentObjectGroupPython] Ni_element002  label="Ni_element : 8"  # scripted group (container) (typed FeaturePython)
  n = 8
  ref = Ni_element
FEATURE [App::DocumentObjectGroupPython] G4_STAINLESS_STEEL  label="G4_STAINLESS-STEEL"  # scripted group (container) (typed FeaturePython)
  Dunit = g/cm3
  Dvalue = 8
  Group = -> [Fe_element008,Cr_element002,Ni_element002]
  conduct = 2
  density = 1
  expand = 3
  formula = G4_STAINLESS-STEEL
  name = G4_STAINLESS-STEEL
  specific = 4
FEATURE [App::DocumentObjectGroupPython] H_element116  label="H_element : 064"  # scripted group (container) (typed FeaturePython)
  n = 18
  ref = H_element
FEATURE [App::DocumentObjectGroupPython] C_element126  label="C_element : 071"  # scripted group (container) (typed FeaturePython)
  n = 12
  ref = C_element
FEATURE [App::DocumentObjectGroupPython] O_element109  label="O_element : 062"  # scripted group (container) (typed FeaturePython)
  n = 7
  ref = O_element
FEATURE [App::DocumentObjectGroupPython] G4_CR39  # scripted group (container) (typed FeaturePython)
  Dunit = g/cm3
  Dvalue = 1.32
  Group = -> [H_element116,C_element126,O_element109]
  conduct = 2
  density = 1
  expand = 3
  formula = G4_CR39
  name = G4_CR39
  specific = 4
FEATURE [App::DocumentObjectGroupPython] H_element117  label="H_element : 38"  # scripted group (container) (typed FeaturePython)
  n = 38
  ref = H_element
FEATURE [App::DocumentObjectGroupPython] C_element127  label="C_element : 072"  # scripted group (container) (typed FeaturePython)
  n = 18
  ref = C_element
FEATURE [App::DocumentObjectGroupPython] O_element110  label="O_element : 063"  # scripted group (container) (typed FeaturePython)
  n = 1
  ref = O_element
FEATURE [App::DocumentObjectGroupPython] G4_OCTADECANOL  # scripted group (container) (typed FeaturePython)
  Dunit = g/cm3
  Dvalue = 0.812
  Group = -> [H_element117,C_element127,O_element110]
  conduct = 2
  density = 1
  expand = 3
  formula = G4_OCTADECANOL
  name = G4_OCTADECANOL
  specific = 4
FEATURE [App::DocumentObjectGroupPython] HEP  # scripted group (container) (typed FeaturePython)
  Group = -> [G4_lH2,G4_lN2,G4_lO2,G4_lAr,G4_lBr,G4_lKr,G4_lXe,G4_PbWO4,G4_Galactic,G4_GRAPHITE_POROUS,G4_LUCITE,G4_BRASS,G4_BRONZE,G4_STAINLESS_STEEL,G4_CR39,G4_OCTADECANOL]
FEATURE [App::DocumentObjectGroupPython] C_element128  label="C_element : 073"  # scripted group (container) (typed FeaturePython)
  n = 14
  ref = C_element
FEATURE [App::DocumentObjectGroupPython] H_element118  label="H_element : 065"  # scripted group (container) (typed FeaturePython)
  n = 10
  ref = H_element
FEATURE [App::DocumentObjectGroupPython] O_element111  label="O_element : 064"  # scripted group (container) (typed FeaturePython)
  n = 2
  ref = O_element
FEATURE [App::DocumentObjectGroupPython] N_element050  label="N_element : 023"  # scripted group (container) (typed FeaturePython)
  n = 2
  ref = N_element
FEATURE [App::DocumentObjectGroupPython] G4_KEVLAR  # scripted group (container) (typed FeaturePython)
  Dunit = g/cm3
  Dvalue = 1.44
  Group = -> [C_element128,H_element118,O_element111,N_element050]
  conduct = 2
  density = 1
  expand = 3
  formula = G4_KEVLAR
  name = G4_KEVLAR
  specific = 4
FEATURE [App::DocumentObjectGroupPython] C_element129  label="C_element : 074"  # scripted group (container) (typed FeaturePython)
  n = 10
  ref = C_element
FEATURE [App::DocumentObjectGroupPython] H_element119  label="H_element : 066"  # scripted group (container) (typed FeaturePython)
  n = 8
  ref = H_element
FEATURE [App::DocumentObjectGroupPython] O_element112  label="O_element : 065"  # scripted group (container) (typed FeaturePython)
  n = 4
  ref = O_element
FEATURE [App::DocumentObjectGroupPython] G4_DACRON  # scripted group (container) (typed FeaturePython)
  Dunit = g/cm3
  Dvalue = 1.4
  Group = -> [C_element129,H_element119,O_element112]
  conduct = 2
  density = 1
  expand = 3
  formula = G4_DACRON
  name = G4_DACRON
  specific = 4
FEATURE [App::DocumentObjectGroupPython] C_element130  label="C_element : 075"  # scripted group (container) (typed FeaturePython)
  n = 4
  ref = C_element
FEATURE [App::DocumentObjectGroupPython] H_element120  label="H_element : 067"  # scripted group (container) (typed FeaturePython)
  n = 5
  ref = H_element
FEATURE [App::DocumentObjectGroupPython] Cl_element030  label="Cl_element : 016"  # scripted group (container) (typed FeaturePython)
  n = 1
  ref = Cl_element
FEATURE [App::DocumentObjectGroupPython] G4_NEOPRENE  # scripted group (container) (typed FeaturePython)
  Dunit = g/cm3
  Dvalue = 1.23
  Group = -> [C_element130,H_element120,Cl_element030]
  conduct = 2
  density = 1
  expand = 3
  formula = G4_NEOPRENE
  name = G4_NEOPRENE
  specific = 4
FEATURE [App::DocumentObjectGroupPython] Space  # scripted group (container) (typed FeaturePython)
  Group = -> [G4_KEVLAR,G4_DACRON,G4_NEOPRENE]
FEATURE [App::DocumentObjectGroupPython] H_element121  label="H_element : 068"  # scripted group (container) (typed FeaturePython)
  n = 5
  ref = H_element
FEATURE [App::DocumentObjectGroupPython] C_element131  label="C_element : 076"  # scripted group (container) (typed FeaturePython)
  n = 4
  ref = C_element
FEATURE [App::DocumentObjectGroupPython] N_element051  label="N_element : 3"  # scripted group (container) (typed FeaturePython)
  n = 3
  ref = N_element
FEATURE [App::DocumentObjectGroupPython] O_element113  label="O_element : 066"  # scripted group (container) (typed FeaturePython)
  n = 1
  ref = O_element
FEATURE [App::DocumentObjectGroupPython] G4_CYTOSINE  # scripted group (container) (typed FeaturePython)
  Dunit = g/cm3
  Dvalue = 1.55
  Group = -> [H_element121,C_element131,N_element051,O_element113]
  conduct = 2
  density = 1
  expand = 3
  formula = G4_CYTOSINE
  name = G4_CYTOSINE
  specific = 4
FEATURE [App::DocumentObjectGroupPython] H_element122  label="H_element : 069"  # scripted group (container) (typed FeaturePython)
  n = 6
  ref = H_element
FEATURE [App::DocumentObjectGroupPython] C_element132  label="C_element : 077"  # scripted group (container) (typed FeaturePython)
  n = 5
  ref = C_element
FEATURE [App::DocumentObjectGroupPython] N_element052  label="N_element : 024"  # scripted group (container) (typed FeaturePython)
  n = 2
  ref = N_element
FEATURE [App::DocumentObjectGroupPython] O_element114  label="O_element : 067"  # scripted group (container) (typed FeaturePython)
  n = 2
  ref = O_element
FEATURE [App::DocumentObjectGroupPython] G4_THYMINE  # scripted group (container) (typed FeaturePython)
  Dunit = g/cm3
  Dvalue = 1.23
  Group = -> [H_element122,C_element132,N_element052,O_element114]
  conduct = 2
  density = 1
  expand = 3
  formula = G4_THYMINE
  name = G4_THYMINE
  specific = 4
FEATURE [App::DocumentObjectGroupPython] H_element123  label="H_element : 070"  # scripted group (container) (typed FeaturePython)
  n = 4
  ref = H_element
FEATURE [App::DocumentObjectGroupPython] C_element133  label="C_element : 078"  # scripted group (container) (typed FeaturePython)
  n = 4
  ref = C_element
FEATURE [App::DocumentObjectGroupPython] N_element053  label="N_element : 025"  # scripted group (container) (typed FeaturePython)
  n = 2
  ref = N_element
FEATURE [App::DocumentObjectGroupPython] O_element115  label="O_element : 068"  # scripted group (container) (typed FeaturePython)
  n = 2
  ref = O_element
FEATURE [App::DocumentObjectGroupPython] G4_URACIL  # scripted group (container) (typed FeaturePython)
  Dunit = g/cm3
  Dvalue = 1.32
  Group = -> [H_element123,C_element133,N_element053,O_element115]
  conduct = 2
  density = 1
  expand = 3
  formula = G4_URACIL
  name = G4_URACIL
  specific = 4
FEATURE [App::DocumentObjectGroupPython] H_element124  label="H_element : 071"  # scripted group (container) (typed FeaturePython)
  n = 4
  ref = H_element
FEATURE [App::DocumentObjectGroupPython] C_element134  label="C_element : 079"  # scripted group (container) (typed FeaturePython)
  n = 5
  ref = C_element
FEATURE [App::DocumentObjectGroupPython] N_element054  label="N_element : 026"  # scripted group (container) (typed FeaturePython)
  n = 5
  ref = N_element
FEATURE [App::DocumentObjectGroupPython] G4_DNA_ADENINE  # scripted group (container) (typed FeaturePython)
  Dunit = g/cm3
  Dvalue = 1
  Group = -> [H_element124,C_element134,N_element054]
  conduct = 2
  density = 1
  expand = 3
  formula = G4_DNA_ADENINE
  name = G4_DNA_ADENINE
  specific = 4
FEATURE [App::DocumentObjectGroupPython] H_element125  label="H_element : 072"  # scripted group (container) (typed FeaturePython)
  n = 4
  ref = H_element
FEATURE [App::DocumentObjectGroupPython] C_element135  label="C_element : 080"  # scripted group (container) (typed FeaturePython)
  n = 5
  ref = C_element
FEATURE [App::DocumentObjectGroupPython] N_element055  label="N_element : 027"  # scripted group (container) (typed FeaturePython)
  n = 5
  ref = N_element
FEATURE [App::DocumentObjectGroupPython] O_element116  label="O_element : 069"  # scripted group (container) (typed FeaturePython)
  n = 1
  ref = O_element
FEATURE [App::DocumentObjectGroupPython] G4_DNA_GUANINE  # scripted group (container) (typed FeaturePython)
  Dunit = g/cm3
  Dvalue = 1
  Group = -> [H_element125,C_element135,N_element055,O_element116]
  conduct = 2
  density = 1
  expand = 3
  formula = G4_DNA_GUANINE
  name = G4_DNA_GUANINE
  specific = 4
FEATURE [App::DocumentObjectGroupPython] H_element126  label="H_element : 073"  # scripted group (container) (typed FeaturePython)
  n = 4
  ref = H_element
FEATURE [App::DocumentObjectGroupPython] C_element136  label="C_element : 081"  # scripted group (container) (typed FeaturePython)
  n = 4
  ref = C_element
FEATURE [App::DocumentObjectGroupPython] N_element056  label="N_element : 028"  # scripted group (container) (typed FeaturePython)
  n = 3
  ref = N_element
FEATURE [App::DocumentObjectGroupPython] O_element117  label="O_element : 070"  # scripted group (container) (typed FeaturePython)
  n = 1
  ref = O_element
FEATURE [App::DocumentObjectGroupPython] G4_DNA_CYTOSINE  # scripted group (container) (typed FeaturePython)
  Dunit = g/cm3
  Dvalue = 1
  Group = -> [H_element126,C_element136,N_element056,O_element117]
  conduct = 2
  density = 1
  expand = 3
  formula = G4_DNA_CYTOSINE
  name = G4_DNA_CYTOSINE
  specific = 4
FEATURE [App::DocumentObjectGroupPython] H_element127  label="H_element : 074"  # scripted group (container) (typed FeaturePython)
  n = 5
  ref = H_element
FEATURE [App::DocumentObjectGroupPython] C_element137  label="C_element : 082"  # scripted group (container) (typed FeaturePython)
  n = 5
  ref = C_element
FEATURE [App::DocumentObjectGroupPython] N_element057  label="N_element : 029"  # scripted group (container) (typed FeaturePython)
  n = 2
  ref = N_element
FEATURE [App::DocumentObjectGroupPython] O_element118  label="O_element : 071"  # scripted group (container) (typed FeaturePython)
  n = 2
  ref = O_element
FEATURE [App::DocumentObjectGroupPython] G4_DNA_THYMINE  # scripted group (container) (typed FeaturePython)
  Dunit = g/cm3
  Dvalue = 1
  Group = -> [H_element127,C_element137,N_element057,O_element118]
  conduct = 2
  density = 1
  expand = 3
  formula = G4_DNA_THYMINE
  name = G4_DNA_THYMINE
  specific = 4
FEATURE [App::DocumentObjectGroupPython] H_element128  label="H_element : 075"  # scripted group (container) (typed FeaturePython)
  n = 3
  ref = H_element
FEATURE [App::DocumentObjectGroupPython] C_element138  label="C_element : 083"  # scripted group (container) (typed FeaturePython)
  n = 4
  ref = C_element
FEATURE [App::DocumentObjectGroupPython] N_element058  label="N_element : 030"  # scripted group (container) (typed FeaturePython)
  n = 2
  ref = N_element
FEATURE [App::DocumentObjectGroupPython] O_element119  label="O_element : 072"  # scripted group (container) (typed FeaturePython)
  n = 2
  ref = O_element
FEATURE [App::DocumentObjectGroupPython] G4_DNA_URACIL  # scripted group (container) (typed FeaturePython)
  Dunit = g/cm3
  Dvalue = 1
  Group = -> [H_element128,C_element138,N_element058,O_element119]
  conduct = 2
  density = 1
  expand = 3
  formula = G4_DNA_URACIL
  name = G4_DNA_URACIL
  specific = 4
FEATURE [App::DocumentObjectGroupPython] H_element129  label="H_element : 076"  # scripted group (container) (typed FeaturePython)
  n = 10
  ref = H_element
FEATURE [App::DocumentObjectGroupPython] C_element139  label="C_element : 084"  # scripted group (container) (typed FeaturePython)
  n = 10
  ref = C_element
FEATURE [App::DocumentObjectGroupPython] N_element059  label="N_element : 031"  # scripted group (container) (typed FeaturePython)
  n = 5
  ref = N_element
FEATURE [App::DocumentObjectGroupPython] O_element120  label="O_element : 073"  # scripted group (container) (typed FeaturePython)
  n = 4
  ref = O_element
FEATURE [App::DocumentObjectGroupPython] G4_DNA_ADENOSINE  # scripted group (container) (typed FeaturePython)
  Dunit = g/cm3
  Dvalue = 1
  Group = -> [H_element129,C_element139,N_element059,O_element120]
  conduct = 2
  density = 1
  expand = 3
  formula = G4_DNA_ADENOSINE
  name = G4_DNA_ADENOSINE
  specific = 4
FEATURE [App::DocumentObjectGroupPython] H_element130  label="H_element : 077"  # scripted group (container) (typed FeaturePython)
  n = 10
  ref = H_element
FEATURE [App::DocumentObjectGroupPython] C_element140  label="C_element : 085"  # scripted group (container) (typed FeaturePython)
  n = 10
  ref = C_element
FEATURE [App::DocumentObjectGroupPython] N_element060  label="N_element : 032"  # scripted group (container) (typed FeaturePython)
  n = 5
  ref = N_element
FEATURE [App::DocumentObjectGroupPython] O_element121  label="O_element : 074"  # scripted group (container) (typed FeaturePython)
  n = 5
  ref = O_element
FEATURE [App::DocumentObjectGroupPython] G4_DNA_GUANOSINE  # scripted group (container) (typed FeaturePython)
  Dunit = g/cm3
  Dvalue = 1
  Group = -> [H_element130,C_element140,N_element060,O_element121]
  conduct = 2
  density = 1
  expand = 3
  formula = G4_DNA_GUANOSINE
  name = G4_DNA_GUANOSINE
  specific = 4
FEATURE [App::DocumentObjectGroupPython] H_element131  label="H_element : 078"  # scripted group (container) (typed FeaturePython)
  n = 10
  ref = H_element
FEATURE [App::DocumentObjectGroupPython] C_element141  label="C_element : 086"  # scripted group (container) (typed FeaturePython)
  n = 9
  ref = C_element
FEATURE [App::DocumentObjectGroupPython] N_element061  label="N_element : 033"  # scripted group (container) (typed FeaturePython)
  n = 3
  ref = N_element
FEATURE [App::DocumentObjectGroupPython] O_element122  label="O_element : 075"  # scripted group (container) (typed FeaturePython)
  n = 5
  ref = O_element
FEATURE [App::DocumentObjectGroupPython] G4_DNA_CYTIDINE  # scripted group (container) (typed FeaturePython)
  Dunit = g/cm3
  Dvalue = 1
  Group = -> [H_element131,C_element141,N_element061,O_element122]
  conduct = 2
  density = 1
  expand = 3
  formula = G4_DNA_CYTIDINE
  name = G4_DNA_CYTIDINE
  specific = 4
FEATURE [App::DocumentObjectGroupPython] H_element132  label="H_element : 079"  # scripted group (container) (typed FeaturePython)
  n = 9
  ref = H_element
FEATURE [App::DocumentObjectGroupPython] C_element142  label="C_element : 087"  # scripted group (container) (typed FeaturePython)
  n = 9
  ref = C_element
FEATURE [App::DocumentObjectGroupPython] N_element062  label="N_element : 034"  # scripted group (container) (typed FeaturePython)
  n = 2
  ref = N_element
FEATURE [App::DocumentObjectGroupPython] O_element123  label="O_element : 076"  # scripted group (container) (typed FeaturePython)
  n = 6
  ref = O_element
FEATURE [App::DocumentObjectGroupPython] G4_DNA_URIDINE  # scripted group (container) (typed FeaturePython)
  Dunit = g/cm3
  Dvalue = 1
  Group = -> [H_element132,C_element142,N_element062,O_element123]
  conduct = 2
  density = 1
  expand = 3
  formula = G4_DNA_URIDINE
  name = G4_DNA_URIDINE
  specific = 4
FEATURE [App::DocumentObjectGroupPython] H_element133  label="H_element : 080"  # scripted group (container) (typed FeaturePython)
  n = 11
  ref = H_element
FEATURE [App::DocumentObjectGroupPython] C_element143  label="C_element : 088"  # scripted group (container) (typed FeaturePython)
  n = 10
  ref = C_element
FEATURE [App::DocumentObjectGroupPython] N_element063  label="N_element : 035"  # scripted group (container) (typed FeaturePython)
  n = 2
  ref = N_element
FEATURE [App::DocumentObjectGroupPython] O_element124  label="O_element : 077"  # scripted group (container) (typed FeaturePython)
  n = 6
  ref = O_element
FEATURE [App::DocumentObjectGroupPython] G4_DNA_METHYLURIDINE  # scripted group (container) (typed FeaturePython)
  Dunit = g/cm3
  Dvalue = 1
  Group = -> [H_element133,C_element143,N_element063,O_element124]
  conduct = 2
  density = 1
  expand = 3
  formula = G4_DNA_METHYLURIDINE
  name = G4_DNA_METHYLURIDINE
  specific = 4
FEATURE [App::DocumentObjectGroupPython] P_element014  label="P_element : 003"  # scripted group (container) (typed FeaturePython)
  n = 1
  ref = P_element
FEATURE [App::DocumentObjectGroupPython] O_element125  label="O_element : 078"  # scripted group (container) (typed FeaturePython)
  n = 3
  ref = O_element
FEATURE [App::DocumentObjectGroupPython] G4_DNA_MONOPHOSPHATE  # scripted group (container) (typed FeaturePython)
  Dunit = g/cm3
  Dvalue = 1
  Group = -> [P_element014,O_element125]
  conduct = 2
  density = 1
  expand = 3
  formula = G4_DNA_MONOPHOSPHATE
  name = G4_DNA_MONOPHOSPHATE
  specific = 4
FEATURE [App::DocumentObjectGroupPython] H_element134  label="H_element : 081"  # scripted group (container) (typed FeaturePython)
  n = 10
  ref = H_element
FEATURE [App::DocumentObjectGroupPython] C_element144  label="C_element : 089"  # scripted group (container) (typed FeaturePython)
  n = 10
  ref = C_element
FEATURE [App::DocumentObjectGroupPython] N_element064  label="N_element : 036"  # scripted group (container) (typed FeaturePython)
  n = 5
  ref = N_element
FEATURE [App::DocumentObjectGroupPython] O_element126  label="O_element : 079"  # scripted group (container) (typed FeaturePython)
  n = 7
  ref = O_element
FEATURE [App::DocumentObjectGroupPython] P_element015  label="P_element : 004"  # scripted group (container) (typed FeaturePython)
  n = 1
  ref = P_element
FEATURE [App::DocumentObjectGroupPython] G4_DNA_A  # scripted group (container) (typed FeaturePython)
  Dunit = g/cm3
  Dvalue = 1
  Group = -> [H_element134,C_element144,N_element064,O_element126,P_element015]
  conduct = 2
  density = 1
  expand = 3
  formula = G4_DNA_A
  name = G4_DNA_A
  specific = 4
FEATURE [App::DocumentObjectGroupPython] H_element135  label="H_element : 082"  # scripted group (container) (typed FeaturePython)
  n = 10
  ref = H_element
FEATURE [App::DocumentObjectGroupPython] C_element145  label="C_element : 090"  # scripted group (container) (typed FeaturePython)
  n = 10
  ref = C_element
FEATURE [App::DocumentObjectGroupPython] N_element065  label="N_element : 037"  # scripted group (container) (typed FeaturePython)
  n = 5
  ref = N_element
FEATURE [App::DocumentObjectGroupPython] O_element127  label="O_element : 8"  # scripted group (container) (typed FeaturePython)
  n = 8
  ref = O_element
FEATURE [App::DocumentObjectGroupPython] P_element016  label="P_element : 005"  # scripted group (container) (typed FeaturePython)
  n = 1
  ref = P_element
FEATURE [App::DocumentObjectGroupPython] G4_DNA_G  # scripted group (container) (typed FeaturePython)
  Dunit = g/cm3
  Dvalue = 1
  Group = -> [H_element135,C_element145,N_element065,O_element127,P_element016]
  conduct = 2
  density = 1
  expand = 3
  formula = G4_DNA_G
  name = G4_DNA_G
  specific = 4
FEATURE [App::DocumentObjectGroupPython] H_element136  label="H_element : 083"  # scripted group (container) (typed FeaturePython)
  n = 10
  ref = H_element
FEATURE [App::DocumentObjectGroupPython] C_element146  label="C_element : 091"  # scripted group (container) (typed FeaturePython)
  n = 9
  ref = C_element
FEATURE [App::DocumentObjectGroupPython] N_element066  label="N_element : 038"  # scripted group (container) (typed FeaturePython)
  n = 3
  ref = N_element
FEATURE [App::DocumentObjectGroupPython] O_element128  label="O_element : 080"  # scripted group (container) (typed FeaturePython)
  n = 8
  ref = O_element
FEATURE [App::DocumentObjectGroupPython] P_element017  label="P_element : 006"  # scripted group (container) (typed FeaturePython)
  n = 1
  ref = P_element
FEATURE [App::DocumentObjectGroupPython] G4_DNA_C  # scripted group (container) (typed FeaturePython)
  Dunit = g/cm3
  Dvalue = 1
  Group = -> [H_element136,C_element146,N_element066,O_element128,P_element017]
  conduct = 2
  density = 1
  expand = 3
  formula = G4_DNA_C
  name = G4_DNA_C
  specific = 4
FEATURE [App::DocumentObjectGroupPython] H_element137  label="H_element : 084"  # scripted group (container) (typed FeaturePython)
  n = 9
  ref = H_element
FEATURE [App::DocumentObjectGroupPython] C_element147  label="C_element : 092"  # scripted group (container) (typed FeaturePython)
  n = 9
  ref = C_element
FEATURE [App::DocumentObjectGroupPython] N_element067  label="N_element : 039"  # scripted group (container) (typed FeaturePython)
  n = 2
  ref = N_element
FEATURE [App::DocumentObjectGroupPython] O_element129  label="O_element : 9"  # scripted group (container) (typed FeaturePython)
  n = 9
  ref = O_element
FEATURE [App::DocumentObjectGroupPython] P_element018  label="P_element : 007"  # scripted group (container) (typed FeaturePython)
  n = 1
  ref = P_element
FEATURE [App::DocumentObjectGroupPython] G4_DNA_U  # scripted group (container) (typed FeaturePython)
  Dunit = g/cm3
  Dvalue = 1
  Group = -> [H_element137,C_element147,N_element067,O_element129,P_element018]
  conduct = 2
  density = 1
  expand = 3
  formula = G4_DNA_U
  name = G4_DNA_U
  specific = 4
FEATURE [App::DocumentObjectGroupPython] H_element138  label="H_element : 085"  # scripted group (container) (typed FeaturePython)
  n = 11
  ref = H_element
FEATURE [App::DocumentObjectGroupPython] C_element148  label="C_element : 093"  # scripted group (container) (typed FeaturePython)
  n = 10
  ref = C_element
FEATURE [App::DocumentObjectGroupPython] N_element068  label="N_element : 040"  # scripted group (container) (typed FeaturePython)
  n = 2
  ref = N_element
FEATURE [App::DocumentObjectGroupPython] O_element130  label="O_element : 081"  # scripted group (container) (typed FeaturePython)
  n = 9
  ref = O_element
FEATURE [App::DocumentObjectGroupPython] P_element019  label="P_element : 008"  # scripted group (container) (typed FeaturePython)
  n = 1
  ref = P_element
FEATURE [App::DocumentObjectGroupPython] G4_DNA_MU  # scripted group (container) (typed FeaturePython)
  Dunit = g/cm3
  Dvalue = 1
  Group = -> [H_element138,C_element148,N_element068,O_element130,P_element019]
  conduct = 2
  density = 1
  expand = 3
  formula = G4_DNA_MU
  name = G4_DNA_MU
  specific = 4
FEATURE [App::DocumentObjectGroupPython] BioChemical  # scripted group (container) (typed FeaturePython)
  Group = -> [G4_CYTOSINE,G4_THYMINE,G4_URACIL,G4_DNA_ADENINE,G4_DNA_GUANINE,G4_DNA_CYTOSINE,G4_DNA_THYMINE,G4_DNA_URACIL,G4_DNA_ADENOSINE,G4_DNA_GUANOSINE,G4_DNA_CYTIDINE,G4_DNA_URIDINE,G4_DNA_METHYLURIDINE,G4_DNA_MONOPHOSPHATE,G4_DNA_A,G4_DNA_G,G4_DNA_C,G4_DNA_U,G4_DNA_MU]
FEATURE [App::DocumentObjectGroupPython] G4Materials  # scripted group (container) (typed FeaturePython)
  Group = -> [NIST,Element,HEP,Space,BioChemical]
  version = 1
FEATURE [App::DocumentObjectGroupPython] Geant4  # scripted group (container) (typed FeaturePython)
  Group = -> [G4Isotopes,G4Elements,G4Materials]
FEATURE [App::DocumentObjectGroupPython] Materials  # scripted group (container) (typed FeaturePython)
  Group = -> [Geant4]
FEATURE [Part::FeaturePython] GDMLBox_WorldBox  # WARN: FeaturePython — macro-defined, semantics opaque (R4)
  lunit = 2
  material = 5
  x = 100
  y = 100
  z = 100
FEATURE [Sketcher::SketchObject] Sketch
  ArcFitTolerance = 0
  FullyConstrained = false
  MakeInternals = false
  sketch-geometry (15):
    g0-g5: Circle [constr] x6 (B-spline internal-alignment scaffolding for g6; pole/knot coordinates omitted)
    g6: BSplineCurve PolesCount=7 KnotsCount=5 Degree=3 IsPeriodic=0
    g7-g10: GeomPoint [constr] x4 (B-spline internal-alignment scaffolding for g6; pole/knot coordinates omitted)
    g11: LineSegment StartX=-4.39557 StartY=8.39124 StartZ=0 EndX=-5.2662 EndY=10.5884 EndZ=0
    g12: LineSegment StartX=-5.2662 StartY=10.5884 StartZ=0 EndX=-7.82152 EndY=9.89481 EndZ=0
    g13: LineSegment StartX=-7.82152 StartY=9.89481 StartZ=0 EndX=-9.50073 EndY=7.63152 EndZ=0
    g14: ArcOfCircle CenterX=-7.8377 CenterY=5.34547 CenterZ=0 NormalX=0 NormalY=0 NormalZ=1 AngleXU=0 Radius=2.82696 StartAngle=4.84147 EndAngle=8.48291
  constraints (9):
    c: Weight(g0) = 1
    c: Equal(g0, g1-g5) x5
    c: InternalAlignment(g0-g5 -> g6) x6
    c: InternalAlignment(g7-g10 -> g6) x4
    c: Coincident(g11,g6)
    c: Coincident(g11,g12)
    c: Coincident(g12,g13)
    c: Coincident(g14,g13)
    c: Coincident(g14,g6)
FEATURE [Part::Extrusion] Extrude
  Base = -> Sketch
  Dir = (0,0,1)
  DirMode = 2
  FaceMakerClass = Part::FaceMakerBullseye
  FaceMakerMode = 3
  LengthFwd = 10
  LengthRev = 0
  Placement = pos=(13,12,0) rot=(0,0,1;0rad)
  Solid = true
  Symmetric = false
  material = 1
FEATURE [Part::Mirroring] Part__Mirroring  label="mirror1"
  Base = (0,0,0)
  Normal = (1,0,0)
  Placement = pos=(0,21,0) rot=(0,0,1;0rad)
  Source = -> Extrude
  material = 261
FEATURE [Part::Mirroring] Part__Mirroring002  label="mirror2"
  Base = (0,0,0)
  Normal = (0,1,0)
  Placement = pos=(0,0,0) rot=(0,0,1;0.523599rad)
  Source = -> Part__Mirroring
FEATURE [App::Part] Part
  Group = -> [Sketch,Extrude,Part__Mirroring,Part__Mirroring002]
  Origin = -> Origin001
FEATURE [App::Part] worldVOL
  Group = -> [GDMLBox_WorldBox,Part]
  Origin = -> Origin
